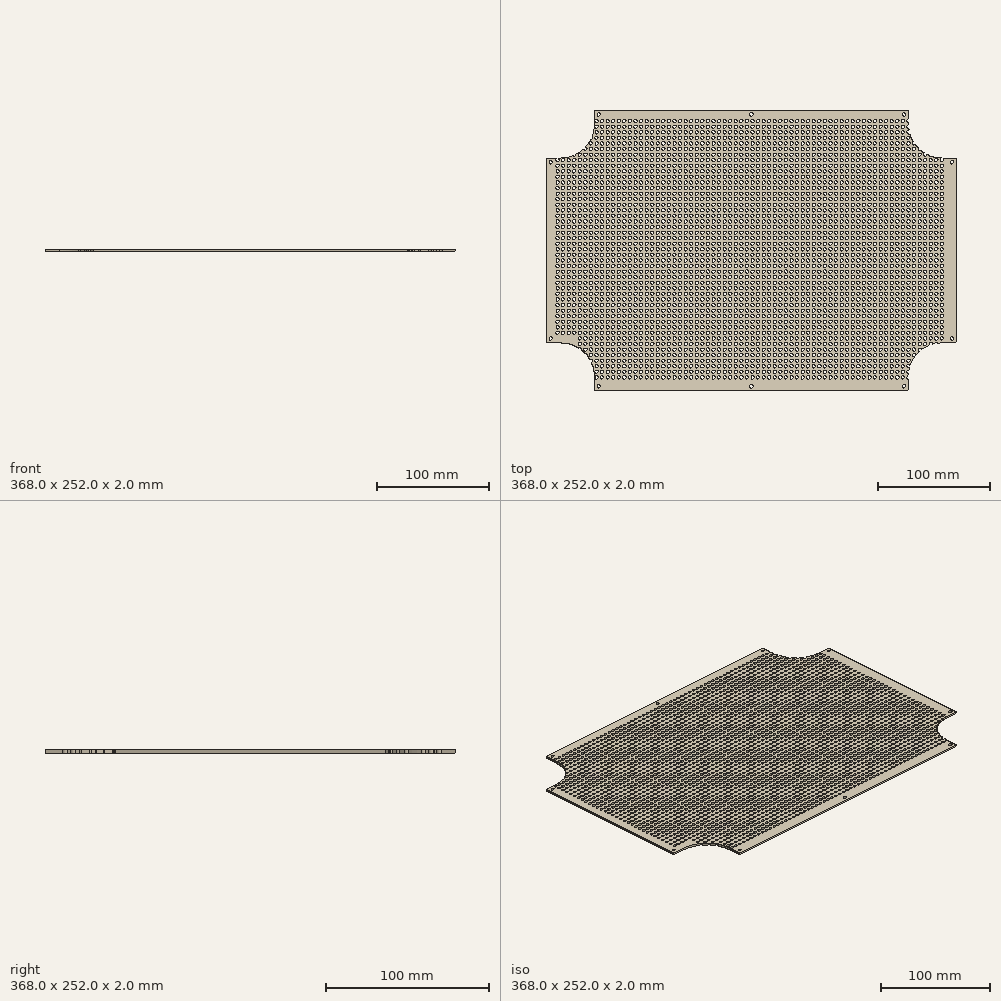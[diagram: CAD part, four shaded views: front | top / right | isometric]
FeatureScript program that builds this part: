
annotation { "Feature Type Name" : "Feature", "Feature Type Description" : "" }
export const myFeature = defineFeature(function(context is Context, id is Id, definition is map)
    precondition{}
    {
        {
            var Q0;
            Q0=qCreatedBy(makeId("Top.planeOp"),FACE);
            var sketch = newSketch(context, id + "F0", { "sketchPlane" : qUnion([Q0])});
            skLineSegment(sketch, "E0", {"start": v(-141, 126) * mm, "end": v(141, 126) * mm});
            skLineSegment(sketch, "E1", {"start": v(141, 126) * mm, "end": v(141, 113) * mm});
            skLineSegment(sketch, "E2", {"start": v(171, 83) * mm, "end": v(184, 83) * mm});
            skLineSegment(sketch, "E3", {"start": v(184, 83) * mm, "end": v(184, -83) * mm});
            skLineSegment(sketch, "E4", {"start": v(184, -83) * mm, "end": v(171, -83) * mm});
            skLineSegment(sketch, "E5", {"start": v(141, -113) * mm, "end": v(141, -126) * mm});
            skLineSegment(sketch, "E6", {"start": v(141, -126) * mm, "end": v(-141, -126) * mm});
            skLineSegment(sketch, "E7", {"start": v(-141, -126) * mm, "end": v(-141, -113) * mm});
            skLineSegment(sketch, "E8", {"start": v(-171, -83) * mm, "end": v(-184, -83) * mm});
            skLineSegment(sketch, "E9", {"start": v(-184, -83) * mm, "end": v(-184, 83) * mm});
            skLineSegment(sketch, "E10", {"start": v(-184, 83) * mm, "end": v(-171, 83) * mm});
            skLineSegment(sketch, "E11", {"start": v(-141, 113) * mm, "end": v(-141, 126) * mm});
            skPoint(sketch, "E12.visualSharp", {"position": v(-141, 83) * mm});
            skArc(sketch, "E12.filletArc", {"start": v(-171, 83) * mm, "mid": v(-149.79, 91.79) * mm, "end": v(-141, 113) * mm});
            skPoint(sketch, "E13.visualSharp", {"position": v(141, 83) * mm});
            skArc(sketch, "E13.filletArc", {"start": v(141, 113) * mm, "mid": v(149.79, 91.79) * mm, "end": v(171, 83) * mm});
            skPoint(sketch, "E14.visualSharp", {"position": v(141, -83) * mm});
            skArc(sketch, "E14.filletArc", {"start": v(171, -83) * mm, "mid": v(149.79, -91.79) * mm, "end": v(141, -113) * mm});
            skPoint(sketch, "E15.visualSharp", {"position": v(-141, -83) * mm});
            skArc(sketch, "E15.filletArc", {"start": v(-141, -113) * mm, "mid": v(-149.79, -91.79) * mm, "end": v(-171, -83) * mm});
            skPoint(sketch, "E16", {"position": v(0, 126) * mm});
            skPoint(sketch, "E17", {"position": v(0, -126) * mm});
            skPoint(sketch, "E18", {"position": v(-184, 0) * mm});
            skPoint(sketch, "E19", {"position": v(184, 0) * mm});
            skLineSegment(sketch, "E20", {"start": v(-137, 139.15) * mm, "end": v(-137, -174.05) * mm, "construction": true});
            skLineSegment(sketch, "E21", {"start": v(-207.28, 122) * mm, "end": v(169.12, 122) * mm, "construction": true});
            skLineSegment(sketch, "E22", {"start": v(-202.37, 79) * mm, "end": v(209.85, 79) * mm, "construction": true});
            skLineSegment(sketch, "E23.MirrorCS", {"start": v(-202.37, -79) * mm, "end": v(209.85, -79) * mm, "construction": true});
            skLineSegment(sketch, "E24.MirrorCS", {"start": v(-207.28, -122) * mm, "end": v(169.12, -122) * mm, "construction": true});
            skLineSegment(sketch, "E25.MirrorCS", {"start": v(137, 139.15) * mm, "end": v(137, -174.05) * mm, "construction": true});
            skLineSegment(sketch, "E26", {"start": v(-180, 93.5) * mm, "end": v(-180, -106.64) * mm, "construction": true});
            skLineSegment(sketch, "E27.MirrorCS", {"start": v(180, 93.5) * mm, "end": v(180, -106.64) * mm, "construction": true});
            skLineSegment(sketch, "E28", {"start": v(0, 134.08) * mm, "end": v(0, -140) * mm, "construction": true});
            skCircle(sketch, "E29", {"center": v(0, 122) * mm, "radius": 1.6 * mm});
            skCircle(sketch, "E30", {"center": v(-137, 122) * mm, "radius": 1.6 * mm});
            skCircle(sketch, "E31", {"center": v(137, 122) * mm, "radius": 1.6 * mm});
            skCircle(sketch, "E32", {"center": v(-180, 79) * mm, "radius": 1.6 * mm});
            skCircle(sketch, "E33", {"center": v(-180, -79) * mm, "radius": 1.6 * mm});
            skCircle(sketch, "E34", {"center": v(-137, -122) * mm, "radius": 1.6 * mm});
            skCircle(sketch, "E35", {"center": v(0, -122) * mm, "radius": 1.6 * mm});
            skCircle(sketch, "E36", {"center": v(137, -122) * mm, "radius": 1.6 * mm});
            skCircle(sketch, "E37", {"center": v(180, -79) * mm, "radius": 1.6 * mm});
            skCircle(sketch, "E38", {"center": v(180, 79) * mm, "radius": 1.6 * mm});
            skLineSegment(sketch, "E39", {"start": v(-174, 129.65) * mm, "end": v(-174, 62.5) * mm, "construction": true});
            skLineSegment(sketch, "E40", {"start": v(-188.78, 116) * mm, "end": v(-116.91, 116) * mm, "construction": true});
            skCircle(sketch, "E41", {"center": v(-174, 116) * mm, "radius": 1.5 * mm});
            skCircle(sketch, "E42.1.0.0", {"center": v(-169, 116) * mm, "radius": 1.5 * mm});
            skCircle(sketch, "E42.2.0.0", {"center": v(-164, 116) * mm, "radius": 1.5 * mm});
            skCircle(sketch, "E42.3.0.0", {"center": v(-159, 116) * mm, "radius": 1.5 * mm});
            skCircle(sketch, "E42.4.0.0", {"center": v(-154, 116) * mm, "radius": 1.5 * mm});
            skCircle(sketch, "E42.5.0.0", {"center": v(-149, 116) * mm, "radius": 1.5 * mm});
            skCircle(sketch, "E42.6.0.0", {"center": v(-144, 116) * mm, "radius": 1.5 * mm});
            skCircle(sketch, "E42.7.0.0", {"center": v(-139, 116) * mm, "radius": 1.5 * mm});
            skCircle(sketch, "E42.8.0.0", {"center": v(-134, 116) * mm, "radius": 1.5 * mm});
            skCircle(sketch, "E42.9.0.0", {"center": v(-129, 116) * mm, "radius": 1.5 * mm});
            skCircle(sketch, "E42.10.0.0", {"center": v(-124, 116) * mm, "radius": 1.5 * mm});
            skCircle(sketch, "E42.11.0.0", {"center": v(-119, 116) * mm, "radius": 1.5 * mm});
            skCircle(sketch, "E42.12.0.0", {"center": v(-114, 116) * mm, "radius": 1.5 * mm});
            skCircle(sketch, "E42.13.0.0", {"center": v(-109, 116) * mm, "radius": 1.5 * mm});
            skCircle(sketch, "E42.14.0.0", {"center": v(-104, 116) * mm, "radius": 1.5 * mm});
            skCircle(sketch, "E42.15.0.0", {"center": v(-99, 116) * mm, "radius": 1.5 * mm});
            skCircle(sketch, "E42.16.0.0", {"center": v(-94, 116) * mm, "radius": 1.5 * mm});
            skCircle(sketch, "E42.17.0.0", {"center": v(-89, 116) * mm, "radius": 1.5 * mm});
            skCircle(sketch, "E42.18.0.0", {"center": v(-84, 116) * mm, "radius": 1.5 * mm});
            skCircle(sketch, "E42.19.0.0", {"center": v(-79, 116) * mm, "radius": 1.5 * mm});
            skCircle(sketch, "E42.20.0.0", {"center": v(-74, 116) * mm, "radius": 1.5 * mm});
            skCircle(sketch, "E42.21.0.0", {"center": v(-69, 116) * mm, "radius": 1.5 * mm});
            skCircle(sketch, "E42.22.0.0", {"center": v(-64, 116) * mm, "radius": 1.5 * mm});
            skCircle(sketch, "E42.23.0.0", {"center": v(-59, 116) * mm, "radius": 1.5 * mm});
            skCircle(sketch, "E42.24.0.0", {"center": v(-54, 116) * mm, "radius": 1.5 * mm});
            skCircle(sketch, "E42.25.0.0", {"center": v(-49, 116) * mm, "radius": 1.5 * mm});
            skCircle(sketch, "E42.26.0.0", {"center": v(-44, 116) * mm, "radius": 1.5 * mm});
            skCircle(sketch, "E42.27.0.0", {"center": v(-39, 116) * mm, "radius": 1.5 * mm});
            skCircle(sketch, "E42.28.0.0", {"center": v(-34, 116) * mm, "radius": 1.5 * mm});
            skCircle(sketch, "E42.29.0.0", {"center": v(-29, 116) * mm, "radius": 1.5 * mm});
            skLineSegment(sketch, "E42.direction1", {"start": v(-174, 116) * mm, "end": v(-169, 116) * mm, "construction": true});
            skCircle(sketch, "E43.0.30.0", {"center": v(-24, 116) * mm, "radius": 1.5 * mm});
            skCircle(sketch, "E43.0.31.0", {"center": v(-19, 116) * mm, "radius": 1.5 * mm});
            skCircle(sketch, "E43.0.32.0", {"center": v(-14, 116) * mm, "radius": 1.5 * mm});
            skCircle(sketch, "E43.0.33.0", {"center": v(-9, 116) * mm, "radius": 1.5 * mm});
            skCircle(sketch, "E43.0.34.0", {"center": v(-4, 116) * mm, "radius": 1.5 * mm});
            skCircle(sketch, "E43.0.35.0", {"center": v(1, 116) * mm, "radius": 1.5 * mm});
            skCircle(sketch, "E43.0.36.0", {"center": v(6, 116) * mm, "radius": 1.5 * mm});
            skCircle(sketch, "E43.0.37.0", {"center": v(11, 116) * mm, "radius": 1.5 * mm});
            skCircle(sketch, "E43.0.38.0", {"center": v(16, 116) * mm, "radius": 1.5 * mm});
            skCircle(sketch, "E43.0.39.0", {"center": v(21, 116) * mm, "radius": 1.5 * mm});
            skCircle(sketch, "E43.0.40.0", {"center": v(26, 116) * mm, "radius": 1.5 * mm});
            skCircle(sketch, "E43.0.41.0", {"center": v(31, 116) * mm, "radius": 1.5 * mm});
            skCircle(sketch, "E43.0.42.0", {"center": v(36, 116) * mm, "radius": 1.5 * mm});
            skCircle(sketch, "E43.0.43.0", {"center": v(41, 116) * mm, "radius": 1.5 * mm});
            skCircle(sketch, "E43.0.44.0", {"center": v(46, 116) * mm, "radius": 1.5 * mm});
            skCircle(sketch, "E43.0.45.0", {"center": v(51, 116) * mm, "radius": 1.5 * mm});
            skCircle(sketch, "E43.0.46.0", {"center": v(56, 116) * mm, "radius": 1.5 * mm});
            skCircle(sketch, "E43.0.47.0", {"center": v(61, 116) * mm, "radius": 1.5 * mm});
            skCircle(sketch, "E43.0.48.0", {"center": v(66, 116) * mm, "radius": 1.5 * mm});
            skCircle(sketch, "E43.0.49.0", {"center": v(71, 116) * mm, "radius": 1.5 * mm});
            skCircle(sketch, "E43.0.50.0", {"center": v(76, 116) * mm, "radius": 1.5 * mm});
            skCircle(sketch, "E43.0.51.0", {"center": v(81, 116) * mm, "radius": 1.5 * mm});
            skCircle(sketch, "E43.0.52.0", {"center": v(86, 116) * mm, "radius": 1.5 * mm});
            skCircle(sketch, "E43.0.53.0", {"center": v(91, 116) * mm, "radius": 1.5 * mm});
            skCircle(sketch, "E43.0.54.0", {"center": v(96, 116) * mm, "radius": 1.5 * mm});
            skCircle(sketch, "E43.0.55.0", {"center": v(101, 116) * mm, "radius": 1.5 * mm});
            skCircle(sketch, "E43.0.56.0", {"center": v(106, 116) * mm, "radius": 1.5 * mm});
            skCircle(sketch, "E43.0.57.0", {"center": v(111, 116) * mm, "radius": 1.5 * mm});
            skCircle(sketch, "E43.0.58.0", {"center": v(116, 116) * mm, "radius": 1.5 * mm});
            skCircle(sketch, "E43.0.59.0", {"center": v(121, 116) * mm, "radius": 1.5 * mm});
            skCircle(sketch, "E43.0.60.0", {"center": v(126, 116) * mm, "radius": 1.5 * mm});
            skCircle(sketch, "E43.0.61.0", {"center": v(131, 116) * mm, "radius": 1.5 * mm});
            skCircle(sketch, "E43.0.62.0", {"center": v(136, 116) * mm, "radius": 1.5 * mm});
            skCircle(sketch, "E43.0.63.0", {"center": v(141, 116) * mm, "radius": 1.5 * mm});
            skCircle(sketch, "E43.0.64.0", {"center": v(146, 116) * mm, "radius": 1.5 * mm});
            skCircle(sketch, "E43.0.65.0", {"center": v(151, 116) * mm, "radius": 1.5 * mm});
            skCircle(sketch, "E43.0.66.0", {"center": v(156, 116) * mm, "radius": 1.5 * mm});
            skCircle(sketch, "E43.0.67.0", {"center": v(161, 116) * mm, "radius": 1.5 * mm});
            skCircle(sketch, "E43.0.68.0", {"center": v(166, 116) * mm, "radius": 1.5 * mm});
            skCircle(sketch, "E43.0.69.0", {"center": v(171, 116) * mm, "radius": 1.5 * mm});
            skCircle(sketch, "E44.1.0.0", {"center": v(166, 111) * mm, "radius": 1.5 * mm});
            skCircle(sketch, "E44.1.0.1", {"center": v(21, 111) * mm, "radius": 1.5 * mm});
            skCircle(sketch, "E44.1.0.2", {"center": v(-99, 111) * mm, "radius": 1.5 * mm});
            skCircle(sketch, "E44.1.0.3", {"center": v(6, 111) * mm, "radius": 1.5 * mm});
            skCircle(sketch, "E44.1.0.4", {"center": v(-54, 111) * mm, "radius": 1.5 * mm});
            skCircle(sketch, "E44.1.0.5", {"center": v(171, 111) * mm, "radius": 1.5 * mm});
            skCircle(sketch, "E44.1.0.6", {"center": v(-104, 111) * mm, "radius": 1.5 * mm});
            skCircle(sketch, "E44.1.0.7", {"center": v(11, 111) * mm, "radius": 1.5 * mm});
            skCircle(sketch, "E44.1.0.8", {"center": v(56, 111) * mm, "radius": 1.5 * mm});
            skCircle(sketch, "E44.1.0.9", {"center": v(-134, 111) * mm, "radius": 1.5 * mm});
            skCircle(sketch, "E44.1.0.10", {"center": v(51, 111) * mm, "radius": 1.5 * mm});
            skCircle(sketch, "E44.1.0.11", {"center": v(131, 111) * mm, "radius": 1.5 * mm});
            skCircle(sketch, "E44.1.0.12", {"center": v(151, 111) * mm, "radius": 1.5 * mm});
            skCircle(sketch, "E44.1.0.13", {"center": v(-24, 111) * mm, "radius": 1.5 * mm});
            skCircle(sketch, "E44.1.0.14", {"center": v(-64, 111) * mm, "radius": 1.5 * mm});
            skCircle(sketch, "E44.1.0.15", {"center": v(-9, 111) * mm, "radius": 1.5 * mm});
            skCircle(sketch, "E44.1.0.16", {"center": v(136, 111) * mm, "radius": 1.5 * mm});
            skCircle(sketch, "E44.1.0.17", {"center": v(91, 111) * mm, "radius": 1.5 * mm});
            skCircle(sketch, "E44.1.0.18", {"center": v(101, 111) * mm, "radius": 1.5 * mm});
            skCircle(sketch, "E44.1.0.19", {"center": v(-144, 111) * mm, "radius": 1.5 * mm});
            skCircle(sketch, "E44.1.0.20", {"center": v(71, 111) * mm, "radius": 1.5 * mm});
            skCircle(sketch, "E44.1.0.21", {"center": v(-69, 111) * mm, "radius": 1.5 * mm});
            skCircle(sketch, "E44.1.0.22", {"center": v(-84, 111) * mm, "radius": 1.5 * mm});
            skCircle(sketch, "E44.1.0.23", {"center": v(116, 111) * mm, "radius": 1.5 * mm});
            skCircle(sketch, "E44.1.0.24", {"center": v(-164, 111) * mm, "radius": 1.5 * mm});
            skCircle(sketch, "E44.1.0.25", {"center": v(86, 111) * mm, "radius": 1.5 * mm});
            skCircle(sketch, "E44.1.0.26", {"center": v(-149, 111) * mm, "radius": 1.5 * mm});
            skCircle(sketch, "E44.1.0.27", {"center": v(106, 111) * mm, "radius": 1.5 * mm});
            skCircle(sketch, "E44.1.0.28", {"center": v(-94, 111) * mm, "radius": 1.5 * mm});
            skCircle(sketch, "E44.1.0.29", {"center": v(-129, 111) * mm, "radius": 1.5 * mm});
            skCircle(sketch, "E44.1.0.30", {"center": v(-19, 111) * mm, "radius": 1.5 * mm});
            skCircle(sketch, "E44.1.0.31", {"center": v(-49, 111) * mm, "radius": 1.5 * mm});
            skCircle(sketch, "E44.1.0.32", {"center": v(26, 111) * mm, "radius": 1.5 * mm});
            skCircle(sketch, "E44.1.0.33", {"center": v(61, 111) * mm, "radius": 1.5 * mm});
            skCircle(sketch, "E44.1.0.34", {"center": v(16, 111) * mm, "radius": 1.5 * mm});
            skCircle(sketch, "E44.1.0.35", {"center": v(96, 111) * mm, "radius": 1.5 * mm});
            skCircle(sketch, "E44.1.0.36", {"center": v(-139, 111) * mm, "radius": 1.5 * mm});
            skCircle(sketch, "E44.1.0.37", {"center": v(-59, 111) * mm, "radius": 1.5 * mm});
            skCircle(sketch, "E44.1.0.38", {"center": v(111, 111) * mm, "radius": 1.5 * mm});
            skCircle(sketch, "E44.1.0.39", {"center": v(146, 111) * mm, "radius": 1.5 * mm});
            skCircle(sketch, "E44.1.0.40", {"center": v(-89, 111) * mm, "radius": 1.5 * mm});
            skCircle(sketch, "E44.1.0.41", {"center": v(-44, 111) * mm, "radius": 1.5 * mm});
            skCircle(sketch, "E44.1.0.42", {"center": v(-124, 111) * mm, "radius": 1.5 * mm});
            skCircle(sketch, "E44.1.0.43", {"center": v(-14, 111) * mm, "radius": 1.5 * mm});
            skCircle(sketch, "E44.1.0.44", {"center": v(31, 111) * mm, "radius": 1.5 * mm});
            skCircle(sketch, "E44.1.0.45", {"center": v(66, 111) * mm, "radius": 1.5 * mm});
            skCircle(sketch, "E44.1.0.46", {"center": v(141, 111) * mm, "radius": 1.5 * mm});
            skCircle(sketch, "E44.1.0.47", {"center": v(36, 111) * mm, "radius": 1.5 * mm});
            skCircle(sketch, "E44.1.0.48", {"center": v(-39, 111) * mm, "radius": 1.5 * mm});
            skCircle(sketch, "E44.1.0.49", {"center": v(-119, 111) * mm, "radius": 1.5 * mm});
            skCircle(sketch, "E44.1.0.50", {"center": v(-79, 111) * mm, "radius": 1.5 * mm});
            skCircle(sketch, "E44.1.0.51", {"center": v(-159, 111) * mm, "radius": 1.5 * mm});
            skCircle(sketch, "E44.1.0.52", {"center": v(156, 111) * mm, "radius": 1.5 * mm});
            skCircle(sketch, "E44.1.0.53", {"center": v(76, 111) * mm, "radius": 1.5 * mm});
            skCircle(sketch, "E44.1.0.54", {"center": v(-4, 111) * mm, "radius": 1.5 * mm});
            skCircle(sketch, "E44.1.0.55", {"center": v(41, 111) * mm, "radius": 1.5 * mm});
            skCircle(sketch, "E44.1.0.56", {"center": v(-34, 111) * mm, "radius": 1.5 * mm});
            skCircle(sketch, "E44.1.0.57", {"center": v(-114, 111) * mm, "radius": 1.5 * mm});
            skCircle(sketch, "E44.1.0.58", {"center": v(121, 111) * mm, "radius": 1.5 * mm});
            skCircle(sketch, "E44.1.0.59", {"center": v(-74, 111) * mm, "radius": 1.5 * mm});
            skCircle(sketch, "E44.1.0.60", {"center": v(-154, 111) * mm, "radius": 1.5 * mm});
            skCircle(sketch, "E44.1.0.61", {"center": v(161, 111) * mm, "radius": 1.5 * mm});
            skCircle(sketch, "E44.1.0.62", {"center": v(81, 111) * mm, "radius": 1.5 * mm});
            skCircle(sketch, "E44.1.0.63", {"center": v(1, 111) * mm, "radius": 1.5 * mm});
            skCircle(sketch, "E44.1.0.64", {"center": v(46, 111) * mm, "radius": 1.5 * mm});
            skCircle(sketch, "E44.1.0.65", {"center": v(-29, 111) * mm, "radius": 1.5 * mm});
            skCircle(sketch, "E44.1.0.66", {"center": v(-109, 111) * mm, "radius": 1.5 * mm});
            skCircle(sketch, "E44.1.0.67", {"center": v(126, 111) * mm, "radius": 1.5 * mm});
            skLineSegment(sketch, "E44.1.0.68", {"start": v(-174, 111) * mm, "end": v(-169, 111) * mm, "construction": true});
            skCircle(sketch, "E44.1.0.69", {"center": v(-174, 111) * mm, "radius": 1.5 * mm});
            skCircle(sketch, "E44.1.0.70", {"center": v(-169, 111) * mm, "radius": 1.5 * mm});
            skCircle(sketch, "E44.2.0.0", {"center": v(166, 106) * mm, "radius": 1.5 * mm});
            skCircle(sketch, "E44.2.0.1", {"center": v(21, 106) * mm, "radius": 1.5 * mm});
            skCircle(sketch, "E44.2.0.2", {"center": v(-99, 106) * mm, "radius": 1.5 * mm});
            skCircle(sketch, "E44.2.0.3", {"center": v(6, 106) * mm, "radius": 1.5 * mm});
            skCircle(sketch, "E44.2.0.4", {"center": v(-54, 106) * mm, "radius": 1.5 * mm});
            skCircle(sketch, "E44.2.0.5", {"center": v(171, 106) * mm, "radius": 1.5 * mm});
            skCircle(sketch, "E44.2.0.6", {"center": v(-104, 106) * mm, "radius": 1.5 * mm});
            skCircle(sketch, "E44.2.0.7", {"center": v(11, 106) * mm, "radius": 1.5 * mm});
            skCircle(sketch, "E44.2.0.8", {"center": v(56, 106) * mm, "radius": 1.5 * mm});
            skCircle(sketch, "E44.2.0.9", {"center": v(-134, 106) * mm, "radius": 1.5 * mm});
            skCircle(sketch, "E44.2.0.10", {"center": v(51, 106) * mm, "radius": 1.5 * mm});
            skCircle(sketch, "E44.2.0.11", {"center": v(131, 106) * mm, "radius": 1.5 * mm});
            skCircle(sketch, "E44.2.0.12", {"center": v(151, 106) * mm, "radius": 1.5 * mm});
            skCircle(sketch, "E44.2.0.13", {"center": v(-24, 106) * mm, "radius": 1.5 * mm});
            skCircle(sketch, "E44.2.0.14", {"center": v(-64, 106) * mm, "radius": 1.5 * mm});
            skCircle(sketch, "E44.2.0.15", {"center": v(-9, 106) * mm, "radius": 1.5 * mm});
            skCircle(sketch, "E44.2.0.16", {"center": v(136, 106) * mm, "radius": 1.5 * mm});
            skCircle(sketch, "E44.2.0.17", {"center": v(91, 106) * mm, "radius": 1.5 * mm});
            skCircle(sketch, "E44.2.0.18", {"center": v(101, 106) * mm, "radius": 1.5 * mm});
            skCircle(sketch, "E44.2.0.19", {"center": v(-144, 106) * mm, "radius": 1.5 * mm});
            skCircle(sketch, "E44.2.0.20", {"center": v(71, 106) * mm, "radius": 1.5 * mm});
            skCircle(sketch, "E44.2.0.21", {"center": v(-69, 106) * mm, "radius": 1.5 * mm});
            skCircle(sketch, "E44.2.0.22", {"center": v(-84, 106) * mm, "radius": 1.5 * mm});
            skCircle(sketch, "E44.2.0.23", {"center": v(116, 106) * mm, "radius": 1.5 * mm});
            skCircle(sketch, "E44.2.0.24", {"center": v(-164, 106) * mm, "radius": 1.5 * mm});
            skCircle(sketch, "E44.2.0.25", {"center": v(86, 106) * mm, "radius": 1.5 * mm});
            skCircle(sketch, "E44.2.0.26", {"center": v(-149, 106) * mm, "radius": 1.5 * mm});
            skCircle(sketch, "E44.2.0.27", {"center": v(106, 106) * mm, "radius": 1.5 * mm});
            skCircle(sketch, "E44.2.0.28", {"center": v(-94, 106) * mm, "radius": 1.5 * mm});
            skCircle(sketch, "E44.2.0.29", {"center": v(-129, 106) * mm, "radius": 1.5 * mm});
            skCircle(sketch, "E44.2.0.30", {"center": v(-19, 106) * mm, "radius": 1.5 * mm});
            skCircle(sketch, "E44.2.0.31", {"center": v(-49, 106) * mm, "radius": 1.5 * mm});
            skCircle(sketch, "E44.2.0.32", {"center": v(26, 106) * mm, "radius": 1.5 * mm});
            skCircle(sketch, "E44.2.0.33", {"center": v(61, 106) * mm, "radius": 1.5 * mm});
            skCircle(sketch, "E44.2.0.34", {"center": v(16, 106) * mm, "radius": 1.5 * mm});
            skCircle(sketch, "E44.2.0.35", {"center": v(96, 106) * mm, "radius": 1.5 * mm});
            skCircle(sketch, "E44.2.0.36", {"center": v(-139, 106) * mm, "radius": 1.5 * mm});
            skCircle(sketch, "E44.2.0.37", {"center": v(-59, 106) * mm, "radius": 1.5 * mm});
            skCircle(sketch, "E44.2.0.38", {"center": v(111, 106) * mm, "radius": 1.5 * mm});
            skCircle(sketch, "E44.2.0.39", {"center": v(146, 106) * mm, "radius": 1.5 * mm});
            skCircle(sketch, "E44.2.0.40", {"center": v(-89, 106) * mm, "radius": 1.5 * mm});
            skCircle(sketch, "E44.2.0.41", {"center": v(-44, 106) * mm, "radius": 1.5 * mm});
            skCircle(sketch, "E44.2.0.42", {"center": v(-124, 106) * mm, "radius": 1.5 * mm});
            skCircle(sketch, "E44.2.0.43", {"center": v(-14, 106) * mm, "radius": 1.5 * mm});
            skCircle(sketch, "E44.2.0.44", {"center": v(31, 106) * mm, "radius": 1.5 * mm});
            skCircle(sketch, "E44.2.0.45", {"center": v(66, 106) * mm, "radius": 1.5 * mm});
            skCircle(sketch, "E44.2.0.46", {"center": v(141, 106) * mm, "radius": 1.5 * mm});
            skCircle(sketch, "E44.2.0.47", {"center": v(36, 106) * mm, "radius": 1.5 * mm});
            skCircle(sketch, "E44.2.0.48", {"center": v(-39, 106) * mm, "radius": 1.5 * mm});
            skCircle(sketch, "E44.2.0.49", {"center": v(-119, 106) * mm, "radius": 1.5 * mm});
            skCircle(sketch, "E44.2.0.50", {"center": v(-79, 106) * mm, "radius": 1.5 * mm});
            skCircle(sketch, "E44.2.0.51", {"center": v(-159, 106) * mm, "radius": 1.5 * mm});
            skCircle(sketch, "E44.2.0.52", {"center": v(156, 106) * mm, "radius": 1.5 * mm});
            skCircle(sketch, "E44.2.0.53", {"center": v(76, 106) * mm, "radius": 1.5 * mm});
            skCircle(sketch, "E44.2.0.54", {"center": v(-4, 106) * mm, "radius": 1.5 * mm});
            skCircle(sketch, "E44.2.0.55", {"center": v(41, 106) * mm, "radius": 1.5 * mm});
            skCircle(sketch, "E44.2.0.56", {"center": v(-34, 106) * mm, "radius": 1.5 * mm});
            skCircle(sketch, "E44.2.0.57", {"center": v(-114, 106) * mm, "radius": 1.5 * mm});
            skCircle(sketch, "E44.2.0.58", {"center": v(121, 106) * mm, "radius": 1.5 * mm});
            skCircle(sketch, "E44.2.0.59", {"center": v(-74, 106) * mm, "radius": 1.5 * mm});
            skCircle(sketch, "E44.2.0.60", {"center": v(-154, 106) * mm, "radius": 1.5 * mm});
            skCircle(sketch, "E44.2.0.61", {"center": v(161, 106) * mm, "radius": 1.5 * mm});
            skCircle(sketch, "E44.2.0.62", {"center": v(81, 106) * mm, "radius": 1.5 * mm});
            skCircle(sketch, "E44.2.0.63", {"center": v(1, 106) * mm, "radius": 1.5 * mm});
            skCircle(sketch, "E44.2.0.64", {"center": v(46, 106) * mm, "radius": 1.5 * mm});
            skCircle(sketch, "E44.2.0.65", {"center": v(-29, 106) * mm, "radius": 1.5 * mm});
            skCircle(sketch, "E44.2.0.66", {"center": v(-109, 106) * mm, "radius": 1.5 * mm});
            skCircle(sketch, "E44.2.0.67", {"center": v(126, 106) * mm, "radius": 1.5 * mm});
            skLineSegment(sketch, "E44.2.0.68", {"start": v(-174, 106) * mm, "end": v(-169, 106) * mm, "construction": true});
            skCircle(sketch, "E44.2.0.69", {"center": v(-174, 106) * mm, "radius": 1.5 * mm});
            skCircle(sketch, "E44.2.0.70", {"center": v(-169, 106) * mm, "radius": 1.5 * mm});
            skCircle(sketch, "E44.3.0.0", {"center": v(166, 101) * mm, "radius": 1.5 * mm});
            skCircle(sketch, "E44.3.0.1", {"center": v(21, 101) * mm, "radius": 1.5 * mm});
            skCircle(sketch, "E44.3.0.2", {"center": v(-99, 101) * mm, "radius": 1.5 * mm});
            skCircle(sketch, "E44.3.0.3", {"center": v(6, 101) * mm, "radius": 1.5 * mm});
            skCircle(sketch, "E44.3.0.4", {"center": v(-54, 101) * mm, "radius": 1.5 * mm});
            skCircle(sketch, "E44.3.0.5", {"center": v(171, 101) * mm, "radius": 1.5 * mm});
            skCircle(sketch, "E44.3.0.6", {"center": v(-104, 101) * mm, "radius": 1.5 * mm});
            skCircle(sketch, "E44.3.0.7", {"center": v(11, 101) * mm, "radius": 1.5 * mm});
            skCircle(sketch, "E44.3.0.8", {"center": v(56, 101) * mm, "radius": 1.5 * mm});
            skCircle(sketch, "E44.3.0.9", {"center": v(-134, 101) * mm, "radius": 1.5 * mm});
            skCircle(sketch, "E44.3.0.10", {"center": v(51, 101) * mm, "radius": 1.5 * mm});
            skCircle(sketch, "E44.3.0.11", {"center": v(131, 101) * mm, "radius": 1.5 * mm});
            skCircle(sketch, "E44.3.0.12", {"center": v(151, 101) * mm, "radius": 1.5 * mm});
            skCircle(sketch, "E44.3.0.13", {"center": v(-24, 101) * mm, "radius": 1.5 * mm});
            skCircle(sketch, "E44.3.0.14", {"center": v(-64, 101) * mm, "radius": 1.5 * mm});
            skCircle(sketch, "E44.3.0.15", {"center": v(-9, 101) * mm, "radius": 1.5 * mm});
            skCircle(sketch, "E44.3.0.16", {"center": v(136, 101) * mm, "radius": 1.5 * mm});
            skCircle(sketch, "E44.3.0.17", {"center": v(91, 101) * mm, "radius": 1.5 * mm});
            skCircle(sketch, "E44.3.0.18", {"center": v(101, 101) * mm, "radius": 1.5 * mm});
            skCircle(sketch, "E44.3.0.19", {"center": v(-144, 101) * mm, "radius": 1.5 * mm});
            skCircle(sketch, "E44.3.0.20", {"center": v(71, 101) * mm, "radius": 1.5 * mm});
            skCircle(sketch, "E44.3.0.21", {"center": v(-69, 101) * mm, "radius": 1.5 * mm});
            skCircle(sketch, "E44.3.0.22", {"center": v(-84, 101) * mm, "radius": 1.5 * mm});
            skCircle(sketch, "E44.3.0.23", {"center": v(116, 101) * mm, "radius": 1.5 * mm});
            skCircle(sketch, "E44.3.0.24", {"center": v(-164, 101) * mm, "radius": 1.5 * mm});
            skCircle(sketch, "E44.3.0.25", {"center": v(86, 101) * mm, "radius": 1.5 * mm});
            skCircle(sketch, "E44.3.0.26", {"center": v(-149, 101) * mm, "radius": 1.5 * mm});
            skCircle(sketch, "E44.3.0.27", {"center": v(106, 101) * mm, "radius": 1.5 * mm});
            skCircle(sketch, "E44.3.0.28", {"center": v(-94, 101) * mm, "radius": 1.5 * mm});
            skCircle(sketch, "E44.3.0.29", {"center": v(-129, 101) * mm, "radius": 1.5 * mm});
            skCircle(sketch, "E44.3.0.30", {"center": v(-19, 101) * mm, "radius": 1.5 * mm});
            skCircle(sketch, "E44.3.0.31", {"center": v(-49, 101) * mm, "radius": 1.5 * mm});
            skCircle(sketch, "E44.3.0.32", {"center": v(26, 101) * mm, "radius": 1.5 * mm});
            skCircle(sketch, "E44.3.0.33", {"center": v(61, 101) * mm, "radius": 1.5 * mm});
            skCircle(sketch, "E44.3.0.34", {"center": v(16, 101) * mm, "radius": 1.5 * mm});
            skCircle(sketch, "E44.3.0.35", {"center": v(96, 101) * mm, "radius": 1.5 * mm});
            skCircle(sketch, "E44.3.0.36", {"center": v(-139, 101) * mm, "radius": 1.5 * mm});
            skCircle(sketch, "E44.3.0.37", {"center": v(-59, 101) * mm, "radius": 1.5 * mm});
            skCircle(sketch, "E44.3.0.38", {"center": v(111, 101) * mm, "radius": 1.5 * mm});
            skCircle(sketch, "E44.3.0.39", {"center": v(146, 101) * mm, "radius": 1.5 * mm});
            skCircle(sketch, "E44.3.0.40", {"center": v(-89, 101) * mm, "radius": 1.5 * mm});
            skCircle(sketch, "E44.3.0.41", {"center": v(-44, 101) * mm, "radius": 1.5 * mm});
            skCircle(sketch, "E44.3.0.42", {"center": v(-124, 101) * mm, "radius": 1.5 * mm});
            skCircle(sketch, "E44.3.0.43", {"center": v(-14, 101) * mm, "radius": 1.5 * mm});
            skCircle(sketch, "E44.3.0.44", {"center": v(31, 101) * mm, "radius": 1.5 * mm});
            skCircle(sketch, "E44.3.0.45", {"center": v(66, 101) * mm, "radius": 1.5 * mm});
            skCircle(sketch, "E44.3.0.46", {"center": v(141, 101) * mm, "radius": 1.5 * mm});
            skCircle(sketch, "E44.3.0.47", {"center": v(36, 101) * mm, "radius": 1.5 * mm});
            skCircle(sketch, "E44.3.0.48", {"center": v(-39, 101) * mm, "radius": 1.5 * mm});
            skCircle(sketch, "E44.3.0.49", {"center": v(-119, 101) * mm, "radius": 1.5 * mm});
            skCircle(sketch, "E44.3.0.50", {"center": v(-79, 101) * mm, "radius": 1.5 * mm});
            skCircle(sketch, "E44.3.0.51", {"center": v(-159, 101) * mm, "radius": 1.5 * mm});
            skCircle(sketch, "E44.3.0.52", {"center": v(156, 101) * mm, "radius": 1.5 * mm});
            skCircle(sketch, "E44.3.0.53", {"center": v(76, 101) * mm, "radius": 1.5 * mm});
            skCircle(sketch, "E44.3.0.54", {"center": v(-4, 101) * mm, "radius": 1.5 * mm});
            skCircle(sketch, "E44.3.0.55", {"center": v(41, 101) * mm, "radius": 1.5 * mm});
            skCircle(sketch, "E44.3.0.56", {"center": v(-34, 101) * mm, "radius": 1.5 * mm});
            skCircle(sketch, "E44.3.0.57", {"center": v(-114, 101) * mm, "radius": 1.5 * mm});
            skCircle(sketch, "E44.3.0.58", {"center": v(121, 101) * mm, "radius": 1.5 * mm});
            skCircle(sketch, "E44.3.0.59", {"center": v(-74, 101) * mm, "radius": 1.5 * mm});
            skCircle(sketch, "E44.3.0.60", {"center": v(-154, 101) * mm, "radius": 1.5 * mm});
            skCircle(sketch, "E44.3.0.61", {"center": v(161, 101) * mm, "radius": 1.5 * mm});
            skCircle(sketch, "E44.3.0.62", {"center": v(81, 101) * mm, "radius": 1.5 * mm});
            skCircle(sketch, "E44.3.0.63", {"center": v(1, 101) * mm, "radius": 1.5 * mm});
            skCircle(sketch, "E44.3.0.64", {"center": v(46, 101) * mm, "radius": 1.5 * mm});
            skCircle(sketch, "E44.3.0.65", {"center": v(-29, 101) * mm, "radius": 1.5 * mm});
            skCircle(sketch, "E44.3.0.66", {"center": v(-109, 101) * mm, "radius": 1.5 * mm});
            skCircle(sketch, "E44.3.0.67", {"center": v(126, 101) * mm, "radius": 1.5 * mm});
            skLineSegment(sketch, "E44.3.0.68", {"start": v(-174, 101) * mm, "end": v(-169, 101) * mm, "construction": true});
            skCircle(sketch, "E44.3.0.69", {"center": v(-174, 101) * mm, "radius": 1.5 * mm});
            skCircle(sketch, "E44.3.0.70", {"center": v(-169, 101) * mm, "radius": 1.5 * mm});
            skCircle(sketch, "E44.4.0.0", {"center": v(166, 96) * mm, "radius": 1.5 * mm});
            skCircle(sketch, "E44.4.0.1", {"center": v(21, 96) * mm, "radius": 1.5 * mm});
            skCircle(sketch, "E44.4.0.2", {"center": v(-99, 96) * mm, "radius": 1.5 * mm});
            skCircle(sketch, "E44.4.0.3", {"center": v(6, 96) * mm, "radius": 1.5 * mm});
            skCircle(sketch, "E44.4.0.4", {"center": v(-54, 96) * mm, "radius": 1.5 * mm});
            skCircle(sketch, "E44.4.0.5", {"center": v(171, 96) * mm, "radius": 1.5 * mm});
            skCircle(sketch, "E44.4.0.6", {"center": v(-104, 96) * mm, "radius": 1.5 * mm});
            skCircle(sketch, "E44.4.0.7", {"center": v(11, 96) * mm, "radius": 1.5 * mm});
            skCircle(sketch, "E44.4.0.8", {"center": v(56, 96) * mm, "radius": 1.5 * mm});
            skCircle(sketch, "E44.4.0.9", {"center": v(-134, 96) * mm, "radius": 1.5 * mm});
            skCircle(sketch, "E44.4.0.10", {"center": v(51, 96) * mm, "radius": 1.5 * mm});
            skCircle(sketch, "E44.4.0.11", {"center": v(131, 96) * mm, "radius": 1.5 * mm});
            skCircle(sketch, "E44.4.0.12", {"center": v(151, 96) * mm, "radius": 1.5 * mm});
            skCircle(sketch, "E44.4.0.13", {"center": v(-24, 96) * mm, "radius": 1.5 * mm});
            skCircle(sketch, "E44.4.0.14", {"center": v(-64, 96) * mm, "radius": 1.5 * mm});
            skCircle(sketch, "E44.4.0.15", {"center": v(-9, 96) * mm, "radius": 1.5 * mm});
            skCircle(sketch, "E44.4.0.16", {"center": v(136, 96) * mm, "radius": 1.5 * mm});
            skCircle(sketch, "E44.4.0.17", {"center": v(91, 96) * mm, "radius": 1.5 * mm});
            skCircle(sketch, "E44.4.0.18", {"center": v(101, 96) * mm, "radius": 1.5 * mm});
            skCircle(sketch, "E44.4.0.19", {"center": v(-144, 96) * mm, "radius": 1.5 * mm});
            skCircle(sketch, "E44.4.0.20", {"center": v(71, 96) * mm, "radius": 1.5 * mm});
            skCircle(sketch, "E44.4.0.21", {"center": v(-69, 96) * mm, "radius": 1.5 * mm});
            skCircle(sketch, "E44.4.0.22", {"center": v(-84, 96) * mm, "radius": 1.5 * mm});
            skCircle(sketch, "E44.4.0.23", {"center": v(116, 96) * mm, "radius": 1.5 * mm});
            skCircle(sketch, "E44.4.0.24", {"center": v(-164, 96) * mm, "radius": 1.5 * mm});
            skCircle(sketch, "E44.4.0.25", {"center": v(86, 96) * mm, "radius": 1.5 * mm});
            skCircle(sketch, "E44.4.0.26", {"center": v(-149, 96) * mm, "radius": 1.5 * mm});
            skCircle(sketch, "E44.4.0.27", {"center": v(106, 96) * mm, "radius": 1.5 * mm});
            skCircle(sketch, "E44.4.0.28", {"center": v(-94, 96) * mm, "radius": 1.5 * mm});
            skCircle(sketch, "E44.4.0.29", {"center": v(-129, 96) * mm, "radius": 1.5 * mm});
            skCircle(sketch, "E44.4.0.30", {"center": v(-19, 96) * mm, "radius": 1.5 * mm});
            skCircle(sketch, "E44.4.0.31", {"center": v(-49, 96) * mm, "radius": 1.5 * mm});
            skCircle(sketch, "E44.4.0.32", {"center": v(26, 96) * mm, "radius": 1.5 * mm});
            skCircle(sketch, "E44.4.0.33", {"center": v(61, 96) * mm, "radius": 1.5 * mm});
            skCircle(sketch, "E44.4.0.34", {"center": v(16, 96) * mm, "radius": 1.5 * mm});
            skCircle(sketch, "E44.4.0.35", {"center": v(96, 96) * mm, "radius": 1.5 * mm});
            skCircle(sketch, "E44.4.0.36", {"center": v(-139, 96) * mm, "radius": 1.5 * mm});
            skCircle(sketch, "E44.4.0.37", {"center": v(-59, 96) * mm, "radius": 1.5 * mm});
            skCircle(sketch, "E44.4.0.38", {"center": v(111, 96) * mm, "radius": 1.5 * mm});
            skCircle(sketch, "E44.4.0.39", {"center": v(146, 96) * mm, "radius": 1.5 * mm});
            skCircle(sketch, "E44.4.0.40", {"center": v(-89, 96) * mm, "radius": 1.5 * mm});
            skCircle(sketch, "E44.4.0.41", {"center": v(-44, 96) * mm, "radius": 1.5 * mm});
            skCircle(sketch, "E44.4.0.42", {"center": v(-124, 96) * mm, "radius": 1.5 * mm});
            skCircle(sketch, "E44.4.0.43", {"center": v(-14, 96) * mm, "radius": 1.5 * mm});
            skCircle(sketch, "E44.4.0.44", {"center": v(31, 96) * mm, "radius": 1.5 * mm});
            skCircle(sketch, "E44.4.0.45", {"center": v(66, 96) * mm, "radius": 1.5 * mm});
            skCircle(sketch, "E44.4.0.46", {"center": v(141, 96) * mm, "radius": 1.5 * mm});
            skCircle(sketch, "E44.4.0.47", {"center": v(36, 96) * mm, "radius": 1.5 * mm});
            skCircle(sketch, "E44.4.0.48", {"center": v(-39, 96) * mm, "radius": 1.5 * mm});
            skCircle(sketch, "E44.4.0.49", {"center": v(-119, 96) * mm, "radius": 1.5 * mm});
            skCircle(sketch, "E44.4.0.50", {"center": v(-79, 96) * mm, "radius": 1.5 * mm});
            skCircle(sketch, "E44.4.0.51", {"center": v(-159, 96) * mm, "radius": 1.5 * mm});
            skCircle(sketch, "E44.4.0.52", {"center": v(156, 96) * mm, "radius": 1.5 * mm});
            skCircle(sketch, "E44.4.0.53", {"center": v(76, 96) * mm, "radius": 1.5 * mm});
            skCircle(sketch, "E44.4.0.54", {"center": v(-4, 96) * mm, "radius": 1.5 * mm});
            skCircle(sketch, "E44.4.0.55", {"center": v(41, 96) * mm, "radius": 1.5 * mm});
            skCircle(sketch, "E44.4.0.56", {"center": v(-34, 96) * mm, "radius": 1.5 * mm});
            skCircle(sketch, "E44.4.0.57", {"center": v(-114, 96) * mm, "radius": 1.5 * mm});
            skCircle(sketch, "E44.4.0.58", {"center": v(121, 96) * mm, "radius": 1.5 * mm});
            skCircle(sketch, "E44.4.0.59", {"center": v(-74, 96) * mm, "radius": 1.5 * mm});
            skCircle(sketch, "E44.4.0.60", {"center": v(-154, 96) * mm, "radius": 1.5 * mm});
            skCircle(sketch, "E44.4.0.61", {"center": v(161, 96) * mm, "radius": 1.5 * mm});
            skCircle(sketch, "E44.4.0.62", {"center": v(81, 96) * mm, "radius": 1.5 * mm});
            skCircle(sketch, "E44.4.0.63", {"center": v(1, 96) * mm, "radius": 1.5 * mm});
            skCircle(sketch, "E44.4.0.64", {"center": v(46, 96) * mm, "radius": 1.5 * mm});
            skCircle(sketch, "E44.4.0.65", {"center": v(-29, 96) * mm, "radius": 1.5 * mm});
            skCircle(sketch, "E44.4.0.66", {"center": v(-109, 96) * mm, "radius": 1.5 * mm});
            skCircle(sketch, "E44.4.0.67", {"center": v(126, 96) * mm, "radius": 1.5 * mm});
            skLineSegment(sketch, "E44.4.0.68", {"start": v(-174, 96) * mm, "end": v(-169, 96) * mm, "construction": true});
            skCircle(sketch, "E44.4.0.69", {"center": v(-174, 96) * mm, "radius": 1.5 * mm});
            skCircle(sketch, "E44.4.0.70", {"center": v(-169, 96) * mm, "radius": 1.5 * mm});
            skCircle(sketch, "E44.5.0.0", {"center": v(166, 91) * mm, "radius": 1.5 * mm});
            skCircle(sketch, "E44.5.0.1", {"center": v(21, 91) * mm, "radius": 1.5 * mm});
            skCircle(sketch, "E44.5.0.2", {"center": v(-99, 91) * mm, "radius": 1.5 * mm});
            skCircle(sketch, "E44.5.0.3", {"center": v(6, 91) * mm, "radius": 1.5 * mm});
            skCircle(sketch, "E44.5.0.4", {"center": v(-54, 91) * mm, "radius": 1.5 * mm});
            skCircle(sketch, "E44.5.0.5", {"center": v(171, 91) * mm, "radius": 1.5 * mm});
            skCircle(sketch, "E44.5.0.6", {"center": v(-104, 91) * mm, "radius": 1.5 * mm});
            skCircle(sketch, "E44.5.0.7", {"center": v(11, 91) * mm, "radius": 1.5 * mm});
            skCircle(sketch, "E44.5.0.8", {"center": v(56, 91) * mm, "radius": 1.5 * mm});
            skCircle(sketch, "E44.5.0.9", {"center": v(-134, 91) * mm, "radius": 1.5 * mm});
            skCircle(sketch, "E44.5.0.10", {"center": v(51, 91) * mm, "radius": 1.5 * mm});
            skCircle(sketch, "E44.5.0.11", {"center": v(131, 91) * mm, "radius": 1.5 * mm});
            skCircle(sketch, "E44.5.0.12", {"center": v(151, 91) * mm, "radius": 1.5 * mm});
            skCircle(sketch, "E44.5.0.13", {"center": v(-24, 91) * mm, "radius": 1.5 * mm});
            skCircle(sketch, "E44.5.0.14", {"center": v(-64, 91) * mm, "radius": 1.5 * mm});
            skCircle(sketch, "E44.5.0.15", {"center": v(-9, 91) * mm, "radius": 1.5 * mm});
            skCircle(sketch, "E44.5.0.16", {"center": v(136, 91) * mm, "radius": 1.5 * mm});
            skCircle(sketch, "E44.5.0.17", {"center": v(91, 91) * mm, "radius": 1.5 * mm});
            skCircle(sketch, "E44.5.0.18", {"center": v(101, 91) * mm, "radius": 1.5 * mm});
            skCircle(sketch, "E44.5.0.19", {"center": v(-144, 91) * mm, "radius": 1.5 * mm});
            skCircle(sketch, "E44.5.0.20", {"center": v(71, 91) * mm, "radius": 1.5 * mm});
            skCircle(sketch, "E44.5.0.21", {"center": v(-69, 91) * mm, "radius": 1.5 * mm});
            skCircle(sketch, "E44.5.0.22", {"center": v(-84, 91) * mm, "radius": 1.5 * mm});
            skCircle(sketch, "E44.5.0.23", {"center": v(116, 91) * mm, "radius": 1.5 * mm});
            skCircle(sketch, "E44.5.0.24", {"center": v(-164, 91) * mm, "radius": 1.5 * mm});
            skCircle(sketch, "E44.5.0.25", {"center": v(86, 91) * mm, "radius": 1.5 * mm});
            skCircle(sketch, "E44.5.0.26", {"center": v(-149, 91) * mm, "radius": 1.5 * mm});
            skCircle(sketch, "E44.5.0.27", {"center": v(106, 91) * mm, "radius": 1.5 * mm});
            skCircle(sketch, "E44.5.0.28", {"center": v(-94, 91) * mm, "radius": 1.5 * mm});
            skCircle(sketch, "E44.5.0.29", {"center": v(-129, 91) * mm, "radius": 1.5 * mm});
            skCircle(sketch, "E44.5.0.30", {"center": v(-19, 91) * mm, "radius": 1.5 * mm});
            skCircle(sketch, "E44.5.0.31", {"center": v(-49, 91) * mm, "radius": 1.5 * mm});
            skCircle(sketch, "E44.5.0.32", {"center": v(26, 91) * mm, "radius": 1.5 * mm});
            skCircle(sketch, "E44.5.0.33", {"center": v(61, 91) * mm, "radius": 1.5 * mm});
            skCircle(sketch, "E44.5.0.34", {"center": v(16, 91) * mm, "radius": 1.5 * mm});
            skCircle(sketch, "E44.5.0.35", {"center": v(96, 91) * mm, "radius": 1.5 * mm});
            skCircle(sketch, "E44.5.0.36", {"center": v(-139, 91) * mm, "radius": 1.5 * mm});
            skCircle(sketch, "E44.5.0.37", {"center": v(-59, 91) * mm, "radius": 1.5 * mm});
            skCircle(sketch, "E44.5.0.38", {"center": v(111, 91) * mm, "radius": 1.5 * mm});
            skCircle(sketch, "E44.5.0.39", {"center": v(146, 91) * mm, "radius": 1.5 * mm});
            skCircle(sketch, "E44.5.0.40", {"center": v(-89, 91) * mm, "radius": 1.5 * mm});
            skCircle(sketch, "E44.5.0.41", {"center": v(-44, 91) * mm, "radius": 1.5 * mm});
            skCircle(sketch, "E44.5.0.42", {"center": v(-124, 91) * mm, "radius": 1.5 * mm});
            skCircle(sketch, "E44.5.0.43", {"center": v(-14, 91) * mm, "radius": 1.5 * mm});
            skCircle(sketch, "E44.5.0.44", {"center": v(31, 91) * mm, "radius": 1.5 * mm});
            skCircle(sketch, "E44.5.0.45", {"center": v(66, 91) * mm, "radius": 1.5 * mm});
            skCircle(sketch, "E44.5.0.46", {"center": v(141, 91) * mm, "radius": 1.5 * mm});
            skCircle(sketch, "E44.5.0.47", {"center": v(36, 91) * mm, "radius": 1.5 * mm});
            skCircle(sketch, "E44.5.0.48", {"center": v(-39, 91) * mm, "radius": 1.5 * mm});
            skCircle(sketch, "E44.5.0.49", {"center": v(-119, 91) * mm, "radius": 1.5 * mm});
            skCircle(sketch, "E44.5.0.50", {"center": v(-79, 91) * mm, "radius": 1.5 * mm});
            skCircle(sketch, "E44.5.0.51", {"center": v(-159, 91) * mm, "radius": 1.5 * mm});
            skCircle(sketch, "E44.5.0.52", {"center": v(156, 91) * mm, "radius": 1.5 * mm});
            skCircle(sketch, "E44.5.0.53", {"center": v(76, 91) * mm, "radius": 1.5 * mm});
            skCircle(sketch, "E44.5.0.54", {"center": v(-4, 91) * mm, "radius": 1.5 * mm});
            skCircle(sketch, "E44.5.0.55", {"center": v(41, 91) * mm, "radius": 1.5 * mm});
            skCircle(sketch, "E44.5.0.56", {"center": v(-34, 91) * mm, "radius": 1.5 * mm});
            skCircle(sketch, "E44.5.0.57", {"center": v(-114, 91) * mm, "radius": 1.5 * mm});
            skCircle(sketch, "E44.5.0.58", {"center": v(121, 91) * mm, "radius": 1.5 * mm});
            skCircle(sketch, "E44.5.0.59", {"center": v(-74, 91) * mm, "radius": 1.5 * mm});
            skCircle(sketch, "E44.5.0.60", {"center": v(-154, 91) * mm, "radius": 1.5 * mm});
            skCircle(sketch, "E44.5.0.61", {"center": v(161, 91) * mm, "radius": 1.5 * mm});
            skCircle(sketch, "E44.5.0.62", {"center": v(81, 91) * mm, "radius": 1.5 * mm});
            skCircle(sketch, "E44.5.0.63", {"center": v(1, 91) * mm, "radius": 1.5 * mm});
            skCircle(sketch, "E44.5.0.64", {"center": v(46, 91) * mm, "radius": 1.5 * mm});
            skCircle(sketch, "E44.5.0.65", {"center": v(-29, 91) * mm, "radius": 1.5 * mm});
            skCircle(sketch, "E44.5.0.66", {"center": v(-109, 91) * mm, "radius": 1.5 * mm});
            skCircle(sketch, "E44.5.0.67", {"center": v(126, 91) * mm, "radius": 1.5 * mm});
            skLineSegment(sketch, "E44.5.0.68", {"start": v(-174, 91) * mm, "end": v(-169, 91) * mm, "construction": true});
            skCircle(sketch, "E44.5.0.69", {"center": v(-174, 91) * mm, "radius": 1.5 * mm});
            skCircle(sketch, "E44.5.0.70", {"center": v(-169, 91) * mm, "radius": 1.5 * mm});
            skCircle(sketch, "E44.6.0.0", {"center": v(166, 86) * mm, "radius": 1.5 * mm});
            skCircle(sketch, "E44.6.0.1", {"center": v(21, 86) * mm, "radius": 1.5 * mm});
            skCircle(sketch, "E44.6.0.2", {"center": v(-99, 86) * mm, "radius": 1.5 * mm});
            skCircle(sketch, "E44.6.0.3", {"center": v(6, 86) * mm, "radius": 1.5 * mm});
            skCircle(sketch, "E44.6.0.4", {"center": v(-54, 86) * mm, "radius": 1.5 * mm});
            skCircle(sketch, "E44.6.0.5", {"center": v(171, 86) * mm, "radius": 1.5 * mm});
            skCircle(sketch, "E44.6.0.6", {"center": v(-104, 86) * mm, "radius": 1.5 * mm});
            skCircle(sketch, "E44.6.0.7", {"center": v(11, 86) * mm, "radius": 1.5 * mm});
            skCircle(sketch, "E44.6.0.8", {"center": v(56, 86) * mm, "radius": 1.5 * mm});
            skCircle(sketch, "E44.6.0.9", {"center": v(-134, 86) * mm, "radius": 1.5 * mm});
            skCircle(sketch, "E44.6.0.10", {"center": v(51, 86) * mm, "radius": 1.5 * mm});
            skCircle(sketch, "E44.6.0.11", {"center": v(131, 86) * mm, "radius": 1.5 * mm});
            skCircle(sketch, "E44.6.0.12", {"center": v(151, 86) * mm, "radius": 1.5 * mm});
            skCircle(sketch, "E44.6.0.13", {"center": v(-24, 86) * mm, "radius": 1.5 * mm});
            skCircle(sketch, "E44.6.0.14", {"center": v(-64, 86) * mm, "radius": 1.5 * mm});
            skCircle(sketch, "E44.6.0.15", {"center": v(-9, 86) * mm, "radius": 1.5 * mm});
            skCircle(sketch, "E44.6.0.16", {"center": v(136, 86) * mm, "radius": 1.5 * mm});
            skCircle(sketch, "E44.6.0.17", {"center": v(91, 86) * mm, "radius": 1.5 * mm});
            skCircle(sketch, "E44.6.0.18", {"center": v(101, 86) * mm, "radius": 1.5 * mm});
            skCircle(sketch, "E44.6.0.19", {"center": v(-144, 86) * mm, "radius": 1.5 * mm});
            skCircle(sketch, "E44.6.0.20", {"center": v(71, 86) * mm, "radius": 1.5 * mm});
            skCircle(sketch, "E44.6.0.21", {"center": v(-69, 86) * mm, "radius": 1.5 * mm});
            skCircle(sketch, "E44.6.0.22", {"center": v(-84, 86) * mm, "radius": 1.5 * mm});
            skCircle(sketch, "E44.6.0.23", {"center": v(116, 86) * mm, "radius": 1.5 * mm});
            skCircle(sketch, "E44.6.0.24", {"center": v(-164, 86) * mm, "radius": 1.5 * mm});
            skCircle(sketch, "E44.6.0.25", {"center": v(86, 86) * mm, "radius": 1.5 * mm});
            skCircle(sketch, "E44.6.0.26", {"center": v(-149, 86) * mm, "radius": 1.5 * mm});
            skCircle(sketch, "E44.6.0.27", {"center": v(106, 86) * mm, "radius": 1.5 * mm});
            skCircle(sketch, "E44.6.0.28", {"center": v(-94, 86) * mm, "radius": 1.5 * mm});
            skCircle(sketch, "E44.6.0.29", {"center": v(-129, 86) * mm, "radius": 1.5 * mm});
            skCircle(sketch, "E44.6.0.30", {"center": v(-19, 86) * mm, "radius": 1.5 * mm});
            skCircle(sketch, "E44.6.0.31", {"center": v(-49, 86) * mm, "radius": 1.5 * mm});
            skCircle(sketch, "E44.6.0.32", {"center": v(26, 86) * mm, "radius": 1.5 * mm});
            skCircle(sketch, "E44.6.0.33", {"center": v(61, 86) * mm, "radius": 1.5 * mm});
            skCircle(sketch, "E44.6.0.34", {"center": v(16, 86) * mm, "radius": 1.5 * mm});
            skCircle(sketch, "E44.6.0.35", {"center": v(96, 86) * mm, "radius": 1.5 * mm});
            skCircle(sketch, "E44.6.0.36", {"center": v(-139, 86) * mm, "radius": 1.5 * mm});
            skCircle(sketch, "E44.6.0.37", {"center": v(-59, 86) * mm, "radius": 1.5 * mm});
            skCircle(sketch, "E44.6.0.38", {"center": v(111, 86) * mm, "radius": 1.5 * mm});
            skCircle(sketch, "E44.6.0.39", {"center": v(146, 86) * mm, "radius": 1.5 * mm});
            skCircle(sketch, "E44.6.0.40", {"center": v(-89, 86) * mm, "radius": 1.5 * mm});
            skCircle(sketch, "E44.6.0.41", {"center": v(-44, 86) * mm, "radius": 1.5 * mm});
            skCircle(sketch, "E44.6.0.42", {"center": v(-124, 86) * mm, "radius": 1.5 * mm});
            skCircle(sketch, "E44.6.0.43", {"center": v(-14, 86) * mm, "radius": 1.5 * mm});
            skCircle(sketch, "E44.6.0.44", {"center": v(31, 86) * mm, "radius": 1.5 * mm});
            skCircle(sketch, "E44.6.0.45", {"center": v(66, 86) * mm, "radius": 1.5 * mm});
            skCircle(sketch, "E44.6.0.46", {"center": v(141, 86) * mm, "radius": 1.5 * mm});
            skCircle(sketch, "E44.6.0.47", {"center": v(36, 86) * mm, "radius": 1.5 * mm});
            skCircle(sketch, "E44.6.0.48", {"center": v(-39, 86) * mm, "radius": 1.5 * mm});
            skCircle(sketch, "E44.6.0.49", {"center": v(-119, 86) * mm, "radius": 1.5 * mm});
            skCircle(sketch, "E44.6.0.50", {"center": v(-79, 86) * mm, "radius": 1.5 * mm});
            skCircle(sketch, "E44.6.0.51", {"center": v(-159, 86) * mm, "radius": 1.5 * mm});
            skCircle(sketch, "E44.6.0.52", {"center": v(156, 86) * mm, "radius": 1.5 * mm});
            skCircle(sketch, "E44.6.0.53", {"center": v(76, 86) * mm, "radius": 1.5 * mm});
            skCircle(sketch, "E44.6.0.54", {"center": v(-4, 86) * mm, "radius": 1.5 * mm});
            skCircle(sketch, "E44.6.0.55", {"center": v(41, 86) * mm, "radius": 1.5 * mm});
            skCircle(sketch, "E44.6.0.56", {"center": v(-34, 86) * mm, "radius": 1.5 * mm});
            skCircle(sketch, "E44.6.0.57", {"center": v(-114, 86) * mm, "radius": 1.5 * mm});
            skCircle(sketch, "E44.6.0.58", {"center": v(121, 86) * mm, "radius": 1.5 * mm});
            skCircle(sketch, "E44.6.0.59", {"center": v(-74, 86) * mm, "radius": 1.5 * mm});
            skCircle(sketch, "E44.6.0.60", {"center": v(-154, 86) * mm, "radius": 1.5 * mm});
            skCircle(sketch, "E44.6.0.61", {"center": v(161, 86) * mm, "radius": 1.5 * mm});
            skCircle(sketch, "E44.6.0.62", {"center": v(81, 86) * mm, "radius": 1.5 * mm});
            skCircle(sketch, "E44.6.0.63", {"center": v(1, 86) * mm, "radius": 1.5 * mm});
            skCircle(sketch, "E44.6.0.64", {"center": v(46, 86) * mm, "radius": 1.5 * mm});
            skCircle(sketch, "E44.6.0.65", {"center": v(-29, 86) * mm, "radius": 1.5 * mm});
            skCircle(sketch, "E44.6.0.66", {"center": v(-109, 86) * mm, "radius": 1.5 * mm});
            skCircle(sketch, "E44.6.0.67", {"center": v(126, 86) * mm, "radius": 1.5 * mm});
            skLineSegment(sketch, "E44.6.0.68", {"start": v(-174, 86) * mm, "end": v(-169, 86) * mm, "construction": true});
            skCircle(sketch, "E44.6.0.69", {"center": v(-174, 86) * mm, "radius": 1.5 * mm});
            skCircle(sketch, "E44.6.0.70", {"center": v(-169, 86) * mm, "radius": 1.5 * mm});
            skCircle(sketch, "E44.7.0.0", {"center": v(166, 81) * mm, "radius": 1.5 * mm});
            skCircle(sketch, "E44.7.0.1", {"center": v(21, 81) * mm, "radius": 1.5 * mm});
            skCircle(sketch, "E44.7.0.2", {"center": v(-99, 81) * mm, "radius": 1.5 * mm});
            skCircle(sketch, "E44.7.0.3", {"center": v(6, 81) * mm, "radius": 1.5 * mm});
            skCircle(sketch, "E44.7.0.4", {"center": v(-54, 81) * mm, "radius": 1.5 * mm});
            skCircle(sketch, "E44.7.0.5", {"center": v(171, 81) * mm, "radius": 1.5 * mm});
            skCircle(sketch, "E44.7.0.6", {"center": v(-104, 81) * mm, "radius": 1.5 * mm});
            skCircle(sketch, "E44.7.0.7", {"center": v(11, 81) * mm, "radius": 1.5 * mm});
            skCircle(sketch, "E44.7.0.8", {"center": v(56, 81) * mm, "radius": 1.5 * mm});
            skCircle(sketch, "E44.7.0.9", {"center": v(-134, 81) * mm, "radius": 1.5 * mm});
            skCircle(sketch, "E44.7.0.10", {"center": v(51, 81) * mm, "radius": 1.5 * mm});
            skCircle(sketch, "E44.7.0.11", {"center": v(131, 81) * mm, "radius": 1.5 * mm});
            skCircle(sketch, "E44.7.0.12", {"center": v(151, 81) * mm, "radius": 1.5 * mm});
            skCircle(sketch, "E44.7.0.13", {"center": v(-24, 81) * mm, "radius": 1.5 * mm});
            skCircle(sketch, "E44.7.0.14", {"center": v(-64, 81) * mm, "radius": 1.5 * mm});
            skCircle(sketch, "E44.7.0.15", {"center": v(-9, 81) * mm, "radius": 1.5 * mm});
            skCircle(sketch, "E44.7.0.16", {"center": v(136, 81) * mm, "radius": 1.5 * mm});
            skCircle(sketch, "E44.7.0.17", {"center": v(91, 81) * mm, "radius": 1.5 * mm});
            skCircle(sketch, "E44.7.0.18", {"center": v(101, 81) * mm, "radius": 1.5 * mm});
            skCircle(sketch, "E44.7.0.19", {"center": v(-144, 81) * mm, "radius": 1.5 * mm});
            skCircle(sketch, "E44.7.0.20", {"center": v(71, 81) * mm, "radius": 1.5 * mm});
            skCircle(sketch, "E44.7.0.21", {"center": v(-69, 81) * mm, "radius": 1.5 * mm});
            skCircle(sketch, "E44.7.0.22", {"center": v(-84, 81) * mm, "radius": 1.5 * mm});
            skCircle(sketch, "E44.7.0.23", {"center": v(116, 81) * mm, "radius": 1.5 * mm});
            skCircle(sketch, "E44.7.0.24", {"center": v(-164, 81) * mm, "radius": 1.5 * mm});
            skCircle(sketch, "E44.7.0.25", {"center": v(86, 81) * mm, "radius": 1.5 * mm});
            skCircle(sketch, "E44.7.0.26", {"center": v(-149, 81) * mm, "radius": 1.5 * mm});
            skCircle(sketch, "E44.7.0.27", {"center": v(106, 81) * mm, "radius": 1.5 * mm});
            skCircle(sketch, "E44.7.0.28", {"center": v(-94, 81) * mm, "radius": 1.5 * mm});
            skCircle(sketch, "E44.7.0.29", {"center": v(-129, 81) * mm, "radius": 1.5 * mm});
            skCircle(sketch, "E44.7.0.30", {"center": v(-19, 81) * mm, "radius": 1.5 * mm});
            skCircle(sketch, "E44.7.0.31", {"center": v(-49, 81) * mm, "radius": 1.5 * mm});
            skCircle(sketch, "E44.7.0.32", {"center": v(26, 81) * mm, "radius": 1.5 * mm});
            skCircle(sketch, "E44.7.0.33", {"center": v(61, 81) * mm, "radius": 1.5 * mm});
            skCircle(sketch, "E44.7.0.34", {"center": v(16, 81) * mm, "radius": 1.5 * mm});
            skCircle(sketch, "E44.7.0.35", {"center": v(96, 81) * mm, "radius": 1.5 * mm});
            skCircle(sketch, "E44.7.0.36", {"center": v(-139, 81) * mm, "radius": 1.5 * mm});
            skCircle(sketch, "E44.7.0.37", {"center": v(-59, 81) * mm, "radius": 1.5 * mm});
            skCircle(sketch, "E44.7.0.38", {"center": v(111, 81) * mm, "radius": 1.5 * mm});
            skCircle(sketch, "E44.7.0.39", {"center": v(146, 81) * mm, "radius": 1.5 * mm});
            skCircle(sketch, "E44.7.0.40", {"center": v(-89, 81) * mm, "radius": 1.5 * mm});
            skCircle(sketch, "E44.7.0.41", {"center": v(-44, 81) * mm, "radius": 1.5 * mm});
            skCircle(sketch, "E44.7.0.42", {"center": v(-124, 81) * mm, "radius": 1.5 * mm});
            skCircle(sketch, "E44.7.0.43", {"center": v(-14, 81) * mm, "radius": 1.5 * mm});
            skCircle(sketch, "E44.7.0.44", {"center": v(31, 81) * mm, "radius": 1.5 * mm});
            skCircle(sketch, "E44.7.0.45", {"center": v(66, 81) * mm, "radius": 1.5 * mm});
            skCircle(sketch, "E44.7.0.46", {"center": v(141, 81) * mm, "radius": 1.5 * mm});
            skCircle(sketch, "E44.7.0.47", {"center": v(36, 81) * mm, "radius": 1.5 * mm});
            skCircle(sketch, "E44.7.0.48", {"center": v(-39, 81) * mm, "radius": 1.5 * mm});
            skCircle(sketch, "E44.7.0.49", {"center": v(-119, 81) * mm, "radius": 1.5 * mm});
            skCircle(sketch, "E44.7.0.50", {"center": v(-79, 81) * mm, "radius": 1.5 * mm});
            skCircle(sketch, "E44.7.0.51", {"center": v(-159, 81) * mm, "radius": 1.5 * mm});
            skCircle(sketch, "E44.7.0.52", {"center": v(156, 81) * mm, "radius": 1.5 * mm});
            skCircle(sketch, "E44.7.0.53", {"center": v(76, 81) * mm, "radius": 1.5 * mm});
            skCircle(sketch, "E44.7.0.54", {"center": v(-4, 81) * mm, "radius": 1.5 * mm});
            skCircle(sketch, "E44.7.0.55", {"center": v(41, 81) * mm, "radius": 1.5 * mm});
            skCircle(sketch, "E44.7.0.56", {"center": v(-34, 81) * mm, "radius": 1.5 * mm});
            skCircle(sketch, "E44.7.0.57", {"center": v(-114, 81) * mm, "radius": 1.5 * mm});
            skCircle(sketch, "E44.7.0.58", {"center": v(121, 81) * mm, "radius": 1.5 * mm});
            skCircle(sketch, "E44.7.0.59", {"center": v(-74, 81) * mm, "radius": 1.5 * mm});
            skCircle(sketch, "E44.7.0.60", {"center": v(-154, 81) * mm, "radius": 1.5 * mm});
            skCircle(sketch, "E44.7.0.61", {"center": v(161, 81) * mm, "radius": 1.5 * mm});
            skCircle(sketch, "E44.7.0.62", {"center": v(81, 81) * mm, "radius": 1.5 * mm});
            skCircle(sketch, "E44.7.0.63", {"center": v(1, 81) * mm, "radius": 1.5 * mm});
            skCircle(sketch, "E44.7.0.64", {"center": v(46, 81) * mm, "radius": 1.5 * mm});
            skCircle(sketch, "E44.7.0.65", {"center": v(-29, 81) * mm, "radius": 1.5 * mm});
            skCircle(sketch, "E44.7.0.66", {"center": v(-109, 81) * mm, "radius": 1.5 * mm});
            skCircle(sketch, "E44.7.0.67", {"center": v(126, 81) * mm, "radius": 1.5 * mm});
            skLineSegment(sketch, "E44.7.0.68", {"start": v(-174, 81) * mm, "end": v(-169, 81) * mm, "construction": true});
            skCircle(sketch, "E44.7.0.69", {"center": v(-174, 81) * mm, "radius": 1.5 * mm});
            skCircle(sketch, "E44.7.0.70", {"center": v(-169, 81) * mm, "radius": 1.5 * mm});
            skCircle(sketch, "E44.8.0.0", {"center": v(166, 76) * mm, "radius": 1.5 * mm});
            skCircle(sketch, "E44.8.0.1", {"center": v(21, 76) * mm, "radius": 1.5 * mm});
            skCircle(sketch, "E44.8.0.2", {"center": v(-99, 76) * mm, "radius": 1.5 * mm});
            skCircle(sketch, "E44.8.0.3", {"center": v(6, 76) * mm, "radius": 1.5 * mm});
            skCircle(sketch, "E44.8.0.4", {"center": v(-54, 76) * mm, "radius": 1.5 * mm});
            skCircle(sketch, "E44.8.0.5", {"center": v(171, 76) * mm, "radius": 1.5 * mm});
            skCircle(sketch, "E44.8.0.6", {"center": v(-104, 76) * mm, "radius": 1.5 * mm});
            skCircle(sketch, "E44.8.0.7", {"center": v(11, 76) * mm, "radius": 1.5 * mm});
            skCircle(sketch, "E44.8.0.8", {"center": v(56, 76) * mm, "radius": 1.5 * mm});
            skCircle(sketch, "E44.8.0.9", {"center": v(-134, 76) * mm, "radius": 1.5 * mm});
            skCircle(sketch, "E44.8.0.10", {"center": v(51, 76) * mm, "radius": 1.5 * mm});
            skCircle(sketch, "E44.8.0.11", {"center": v(131, 76) * mm, "radius": 1.5 * mm});
            skCircle(sketch, "E44.8.0.12", {"center": v(151, 76) * mm, "radius": 1.5 * mm});
            skCircle(sketch, "E44.8.0.13", {"center": v(-24, 76) * mm, "radius": 1.5 * mm});
            skCircle(sketch, "E44.8.0.14", {"center": v(-64, 76) * mm, "radius": 1.5 * mm});
            skCircle(sketch, "E44.8.0.15", {"center": v(-9, 76) * mm, "radius": 1.5 * mm});
            skCircle(sketch, "E44.8.0.16", {"center": v(136, 76) * mm, "radius": 1.5 * mm});
            skCircle(sketch, "E44.8.0.17", {"center": v(91, 76) * mm, "radius": 1.5 * mm});
            skCircle(sketch, "E44.8.0.18", {"center": v(101, 76) * mm, "radius": 1.5 * mm});
            skCircle(sketch, "E44.8.0.19", {"center": v(-144, 76) * mm, "radius": 1.5 * mm});
            skCircle(sketch, "E44.8.0.20", {"center": v(71, 76) * mm, "radius": 1.5 * mm});
            skCircle(sketch, "E44.8.0.21", {"center": v(-69, 76) * mm, "radius": 1.5 * mm});
            skCircle(sketch, "E44.8.0.22", {"center": v(-84, 76) * mm, "radius": 1.5 * mm});
            skCircle(sketch, "E44.8.0.23", {"center": v(116, 76) * mm, "radius": 1.5 * mm});
            skCircle(sketch, "E44.8.0.24", {"center": v(-164, 76) * mm, "radius": 1.5 * mm});
            skCircle(sketch, "E44.8.0.25", {"center": v(86, 76) * mm, "radius": 1.5 * mm});
            skCircle(sketch, "E44.8.0.26", {"center": v(-149, 76) * mm, "radius": 1.5 * mm});
            skCircle(sketch, "E44.8.0.27", {"center": v(106, 76) * mm, "radius": 1.5 * mm});
            skCircle(sketch, "E44.8.0.28", {"center": v(-94, 76) * mm, "radius": 1.5 * mm});
            skCircle(sketch, "E44.8.0.29", {"center": v(-129, 76) * mm, "radius": 1.5 * mm});
            skCircle(sketch, "E44.8.0.30", {"center": v(-19, 76) * mm, "radius": 1.5 * mm});
            skCircle(sketch, "E44.8.0.31", {"center": v(-49, 76) * mm, "radius": 1.5 * mm});
            skCircle(sketch, "E44.8.0.32", {"center": v(26, 76) * mm, "radius": 1.5 * mm});
            skCircle(sketch, "E44.8.0.33", {"center": v(61, 76) * mm, "radius": 1.5 * mm});
            skCircle(sketch, "E44.8.0.34", {"center": v(16, 76) * mm, "radius": 1.5 * mm});
            skCircle(sketch, "E44.8.0.35", {"center": v(96, 76) * mm, "radius": 1.5 * mm});
            skCircle(sketch, "E44.8.0.36", {"center": v(-139, 76) * mm, "radius": 1.5 * mm});
            skCircle(sketch, "E44.8.0.37", {"center": v(-59, 76) * mm, "radius": 1.5 * mm});
            skCircle(sketch, "E44.8.0.38", {"center": v(111, 76) * mm, "radius": 1.5 * mm});
            skCircle(sketch, "E44.8.0.39", {"center": v(146, 76) * mm, "radius": 1.5 * mm});
            skCircle(sketch, "E44.8.0.40", {"center": v(-89, 76) * mm, "radius": 1.5 * mm});
            skCircle(sketch, "E44.8.0.41", {"center": v(-44, 76) * mm, "radius": 1.5 * mm});
            skCircle(sketch, "E44.8.0.42", {"center": v(-124, 76) * mm, "radius": 1.5 * mm});
            skCircle(sketch, "E44.8.0.43", {"center": v(-14, 76) * mm, "radius": 1.5 * mm});
            skCircle(sketch, "E44.8.0.44", {"center": v(31, 76) * mm, "radius": 1.5 * mm});
            skCircle(sketch, "E44.8.0.45", {"center": v(66, 76) * mm, "radius": 1.5 * mm});
            skCircle(sketch, "E44.8.0.46", {"center": v(141, 76) * mm, "radius": 1.5 * mm});
            skCircle(sketch, "E44.8.0.47", {"center": v(36, 76) * mm, "radius": 1.5 * mm});
            skCircle(sketch, "E44.8.0.48", {"center": v(-39, 76) * mm, "radius": 1.5 * mm});
            skCircle(sketch, "E44.8.0.49", {"center": v(-119, 76) * mm, "radius": 1.5 * mm});
            skCircle(sketch, "E44.8.0.50", {"center": v(-79, 76) * mm, "radius": 1.5 * mm});
            skCircle(sketch, "E44.8.0.51", {"center": v(-159, 76) * mm, "radius": 1.5 * mm});
            skCircle(sketch, "E44.8.0.52", {"center": v(156, 76) * mm, "radius": 1.5 * mm});
            skCircle(sketch, "E44.8.0.53", {"center": v(76, 76) * mm, "radius": 1.5 * mm});
            skCircle(sketch, "E44.8.0.54", {"center": v(-4, 76) * mm, "radius": 1.5 * mm});
            skCircle(sketch, "E44.8.0.55", {"center": v(41, 76) * mm, "radius": 1.5 * mm});
            skCircle(sketch, "E44.8.0.56", {"center": v(-34, 76) * mm, "radius": 1.5 * mm});
            skCircle(sketch, "E44.8.0.57", {"center": v(-114, 76) * mm, "radius": 1.5 * mm});
            skCircle(sketch, "E44.8.0.58", {"center": v(121, 76) * mm, "radius": 1.5 * mm});
            skCircle(sketch, "E44.8.0.59", {"center": v(-74, 76) * mm, "radius": 1.5 * mm});
            skCircle(sketch, "E44.8.0.60", {"center": v(-154, 76) * mm, "radius": 1.5 * mm});
            skCircle(sketch, "E44.8.0.61", {"center": v(161, 76) * mm, "radius": 1.5 * mm});
            skCircle(sketch, "E44.8.0.62", {"center": v(81, 76) * mm, "radius": 1.5 * mm});
            skCircle(sketch, "E44.8.0.63", {"center": v(1, 76) * mm, "radius": 1.5 * mm});
            skCircle(sketch, "E44.8.0.64", {"center": v(46, 76) * mm, "radius": 1.5 * mm});
            skCircle(sketch, "E44.8.0.65", {"center": v(-29, 76) * mm, "radius": 1.5 * mm});
            skCircle(sketch, "E44.8.0.66", {"center": v(-109, 76) * mm, "radius": 1.5 * mm});
            skCircle(sketch, "E44.8.0.67", {"center": v(126, 76) * mm, "radius": 1.5 * mm});
            skLineSegment(sketch, "E44.8.0.68", {"start": v(-174, 76) * mm, "end": v(-169, 76) * mm, "construction": true});
            skCircle(sketch, "E44.8.0.69", {"center": v(-174, 76) * mm, "radius": 1.5 * mm});
            skCircle(sketch, "E44.8.0.70", {"center": v(-169, 76) * mm, "radius": 1.5 * mm});
            skCircle(sketch, "E44.9.0.0", {"center": v(166, 71) * mm, "radius": 1.5 * mm});
            skCircle(sketch, "E44.9.0.1", {"center": v(21, 71) * mm, "radius": 1.5 * mm});
            skCircle(sketch, "E44.9.0.2", {"center": v(-99, 71) * mm, "radius": 1.5 * mm});
            skCircle(sketch, "E44.9.0.3", {"center": v(6, 71) * mm, "radius": 1.5 * mm});
            skCircle(sketch, "E44.9.0.4", {"center": v(-54, 71) * mm, "radius": 1.5 * mm});
            skCircle(sketch, "E44.9.0.5", {"center": v(171, 71) * mm, "radius": 1.5 * mm});
            skCircle(sketch, "E44.9.0.6", {"center": v(-104, 71) * mm, "radius": 1.5 * mm});
            skCircle(sketch, "E44.9.0.7", {"center": v(11, 71) * mm, "radius": 1.5 * mm});
            skCircle(sketch, "E44.9.0.8", {"center": v(56, 71) * mm, "radius": 1.5 * mm});
            skCircle(sketch, "E44.9.0.9", {"center": v(-134, 71) * mm, "radius": 1.5 * mm});
            skCircle(sketch, "E44.9.0.10", {"center": v(51, 71) * mm, "radius": 1.5 * mm});
            skCircle(sketch, "E44.9.0.11", {"center": v(131, 71) * mm, "radius": 1.5 * mm});
            skCircle(sketch, "E44.9.0.12", {"center": v(151, 71) * mm, "radius": 1.5 * mm});
            skCircle(sketch, "E44.9.0.13", {"center": v(-24, 71) * mm, "radius": 1.5 * mm});
            skCircle(sketch, "E44.9.0.14", {"center": v(-64, 71) * mm, "radius": 1.5 * mm});
            skCircle(sketch, "E44.9.0.15", {"center": v(-9, 71) * mm, "radius": 1.5 * mm});
            skCircle(sketch, "E44.9.0.16", {"center": v(136, 71) * mm, "radius": 1.5 * mm});
            skCircle(sketch, "E44.9.0.17", {"center": v(91, 71) * mm, "radius": 1.5 * mm});
            skCircle(sketch, "E44.9.0.18", {"center": v(101, 71) * mm, "radius": 1.5 * mm});
            skCircle(sketch, "E44.9.0.19", {"center": v(-144, 71) * mm, "radius": 1.5 * mm});
            skCircle(sketch, "E44.9.0.20", {"center": v(71, 71) * mm, "radius": 1.5 * mm});
            skCircle(sketch, "E44.9.0.21", {"center": v(-69, 71) * mm, "radius": 1.5 * mm});
            skCircle(sketch, "E44.9.0.22", {"center": v(-84, 71) * mm, "radius": 1.5 * mm});
            skCircle(sketch, "E44.9.0.23", {"center": v(116, 71) * mm, "radius": 1.5 * mm});
            skCircle(sketch, "E44.9.0.24", {"center": v(-164, 71) * mm, "radius": 1.5 * mm});
            skCircle(sketch, "E44.9.0.25", {"center": v(86, 71) * mm, "radius": 1.5 * mm});
            skCircle(sketch, "E44.9.0.26", {"center": v(-149, 71) * mm, "radius": 1.5 * mm});
            skCircle(sketch, "E44.9.0.27", {"center": v(106, 71) * mm, "radius": 1.5 * mm});
            skCircle(sketch, "E44.9.0.28", {"center": v(-94, 71) * mm, "radius": 1.5 * mm});
            skCircle(sketch, "E44.9.0.29", {"center": v(-129, 71) * mm, "radius": 1.5 * mm});
            skCircle(sketch, "E44.9.0.30", {"center": v(-19, 71) * mm, "radius": 1.5 * mm});
            skCircle(sketch, "E44.9.0.31", {"center": v(-49, 71) * mm, "radius": 1.5 * mm});
            skCircle(sketch, "E44.9.0.32", {"center": v(26, 71) * mm, "radius": 1.5 * mm});
            skCircle(sketch, "E44.9.0.33", {"center": v(61, 71) * mm, "radius": 1.5 * mm});
            skCircle(sketch, "E44.9.0.34", {"center": v(16, 71) * mm, "radius": 1.5 * mm});
            skCircle(sketch, "E44.9.0.35", {"center": v(96, 71) * mm, "radius": 1.5 * mm});
            skCircle(sketch, "E44.9.0.36", {"center": v(-139, 71) * mm, "radius": 1.5 * mm});
            skCircle(sketch, "E44.9.0.37", {"center": v(-59, 71) * mm, "radius": 1.5 * mm});
            skCircle(sketch, "E44.9.0.38", {"center": v(111, 71) * mm, "radius": 1.5 * mm});
            skCircle(sketch, "E44.9.0.39", {"center": v(146, 71) * mm, "radius": 1.5 * mm});
            skCircle(sketch, "E44.9.0.40", {"center": v(-89, 71) * mm, "radius": 1.5 * mm});
            skCircle(sketch, "E44.9.0.41", {"center": v(-44, 71) * mm, "radius": 1.5 * mm});
            skCircle(sketch, "E44.9.0.42", {"center": v(-124, 71) * mm, "radius": 1.5 * mm});
            skCircle(sketch, "E44.9.0.43", {"center": v(-14, 71) * mm, "radius": 1.5 * mm});
            skCircle(sketch, "E44.9.0.44", {"center": v(31, 71) * mm, "radius": 1.5 * mm});
            skCircle(sketch, "E44.9.0.45", {"center": v(66, 71) * mm, "radius": 1.5 * mm});
            skCircle(sketch, "E44.9.0.46", {"center": v(141, 71) * mm, "radius": 1.5 * mm});
            skCircle(sketch, "E44.9.0.47", {"center": v(36, 71) * mm, "radius": 1.5 * mm});
            skCircle(sketch, "E44.9.0.48", {"center": v(-39, 71) * mm, "radius": 1.5 * mm});
            skCircle(sketch, "E44.9.0.49", {"center": v(-119, 71) * mm, "radius": 1.5 * mm});
            skCircle(sketch, "E44.9.0.50", {"center": v(-79, 71) * mm, "radius": 1.5 * mm});
            skCircle(sketch, "E44.9.0.51", {"center": v(-159, 71) * mm, "radius": 1.5 * mm});
            skCircle(sketch, "E44.9.0.52", {"center": v(156, 71) * mm, "radius": 1.5 * mm});
            skCircle(sketch, "E44.9.0.53", {"center": v(76, 71) * mm, "radius": 1.5 * mm});
            skCircle(sketch, "E44.9.0.54", {"center": v(-4, 71) * mm, "radius": 1.5 * mm});
            skCircle(sketch, "E44.9.0.55", {"center": v(41, 71) * mm, "radius": 1.5 * mm});
            skCircle(sketch, "E44.9.0.56", {"center": v(-34, 71) * mm, "radius": 1.5 * mm});
            skCircle(sketch, "E44.9.0.57", {"center": v(-114, 71) * mm, "radius": 1.5 * mm});
            skCircle(sketch, "E44.9.0.58", {"center": v(121, 71) * mm, "radius": 1.5 * mm});
            skCircle(sketch, "E44.9.0.59", {"center": v(-74, 71) * mm, "radius": 1.5 * mm});
            skCircle(sketch, "E44.9.0.60", {"center": v(-154, 71) * mm, "radius": 1.5 * mm});
            skCircle(sketch, "E44.9.0.61", {"center": v(161, 71) * mm, "radius": 1.5 * mm});
            skCircle(sketch, "E44.9.0.62", {"center": v(81, 71) * mm, "radius": 1.5 * mm});
            skCircle(sketch, "E44.9.0.63", {"center": v(1, 71) * mm, "radius": 1.5 * mm});
            skCircle(sketch, "E44.9.0.64", {"center": v(46, 71) * mm, "radius": 1.5 * mm});
            skCircle(sketch, "E44.9.0.65", {"center": v(-29, 71) * mm, "radius": 1.5 * mm});
            skCircle(sketch, "E44.9.0.66", {"center": v(-109, 71) * mm, "radius": 1.5 * mm});
            skCircle(sketch, "E44.9.0.67", {"center": v(126, 71) * mm, "radius": 1.5 * mm});
            skLineSegment(sketch, "E44.9.0.68", {"start": v(-174, 71) * mm, "end": v(-169, 71) * mm, "construction": true});
            skCircle(sketch, "E44.9.0.69", {"center": v(-174, 71) * mm, "radius": 1.5 * mm});
            skCircle(sketch, "E44.9.0.70", {"center": v(-169, 71) * mm, "radius": 1.5 * mm});
            skCircle(sketch, "E44.10.0.0", {"center": v(166, 66) * mm, "radius": 1.5 * mm});
            skCircle(sketch, "E44.10.0.1", {"center": v(21, 66) * mm, "radius": 1.5 * mm});
            skCircle(sketch, "E44.10.0.2", {"center": v(-99, 66) * mm, "radius": 1.5 * mm});
            skCircle(sketch, "E44.10.0.3", {"center": v(6, 66) * mm, "radius": 1.5 * mm});
            skCircle(sketch, "E44.10.0.4", {"center": v(-54, 66) * mm, "radius": 1.5 * mm});
            skCircle(sketch, "E44.10.0.5", {"center": v(171, 66) * mm, "radius": 1.5 * mm});
            skCircle(sketch, "E44.10.0.6", {"center": v(-104, 66) * mm, "radius": 1.5 * mm});
            skCircle(sketch, "E44.10.0.7", {"center": v(11, 66) * mm, "radius": 1.5 * mm});
            skCircle(sketch, "E44.10.0.8", {"center": v(56, 66) * mm, "radius": 1.5 * mm});
            skCircle(sketch, "E44.10.0.9", {"center": v(-134, 66) * mm, "radius": 1.5 * mm});
            skCircle(sketch, "E44.10.0.10", {"center": v(51, 66) * mm, "radius": 1.5 * mm});
            skCircle(sketch, "E44.10.0.11", {"center": v(131, 66) * mm, "radius": 1.5 * mm});
            skCircle(sketch, "E44.10.0.12", {"center": v(151, 66) * mm, "radius": 1.5 * mm});
            skCircle(sketch, "E44.10.0.13", {"center": v(-24, 66) * mm, "radius": 1.5 * mm});
            skCircle(sketch, "E44.10.0.14", {"center": v(-64, 66) * mm, "radius": 1.5 * mm});
            skCircle(sketch, "E44.10.0.15", {"center": v(-9, 66) * mm, "radius": 1.5 * mm});
            skCircle(sketch, "E44.10.0.16", {"center": v(136, 66) * mm, "radius": 1.5 * mm});
            skCircle(sketch, "E44.10.0.17", {"center": v(91, 66) * mm, "radius": 1.5 * mm});
            skCircle(sketch, "E44.10.0.18", {"center": v(101, 66) * mm, "radius": 1.5 * mm});
            skCircle(sketch, "E44.10.0.19", {"center": v(-144, 66) * mm, "radius": 1.5 * mm});
            skCircle(sketch, "E44.10.0.20", {"center": v(71, 66) * mm, "radius": 1.5 * mm});
            skCircle(sketch, "E44.10.0.21", {"center": v(-69, 66) * mm, "radius": 1.5 * mm});
            skCircle(sketch, "E44.10.0.22", {"center": v(-84, 66) * mm, "radius": 1.5 * mm});
            skCircle(sketch, "E44.10.0.23", {"center": v(116, 66) * mm, "radius": 1.5 * mm});
            skCircle(sketch, "E44.10.0.24", {"center": v(-164, 66) * mm, "radius": 1.5 * mm});
            skCircle(sketch, "E44.10.0.25", {"center": v(86, 66) * mm, "radius": 1.5 * mm});
            skCircle(sketch, "E44.10.0.26", {"center": v(-149, 66) * mm, "radius": 1.5 * mm});
            skCircle(sketch, "E44.10.0.27", {"center": v(106, 66) * mm, "radius": 1.5 * mm});
            skCircle(sketch, "E44.10.0.28", {"center": v(-94, 66) * mm, "radius": 1.5 * mm});
            skCircle(sketch, "E44.10.0.29", {"center": v(-129, 66) * mm, "radius": 1.5 * mm});
            skCircle(sketch, "E44.10.0.30", {"center": v(-19, 66) * mm, "radius": 1.5 * mm});
            skCircle(sketch, "E44.10.0.31", {"center": v(-49, 66) * mm, "radius": 1.5 * mm});
            skCircle(sketch, "E44.10.0.32", {"center": v(26, 66) * mm, "radius": 1.5 * mm});
            skCircle(sketch, "E44.10.0.33", {"center": v(61, 66) * mm, "radius": 1.5 * mm});
            skCircle(sketch, "E44.10.0.34", {"center": v(16, 66) * mm, "radius": 1.5 * mm});
            skCircle(sketch, "E44.10.0.35", {"center": v(96, 66) * mm, "radius": 1.5 * mm});
            skCircle(sketch, "E44.10.0.36", {"center": v(-139, 66) * mm, "radius": 1.5 * mm});
            skCircle(sketch, "E44.10.0.37", {"center": v(-59, 66) * mm, "radius": 1.5 * mm});
            skCircle(sketch, "E44.10.0.38", {"center": v(111, 66) * mm, "radius": 1.5 * mm});
            skCircle(sketch, "E44.10.0.39", {"center": v(146, 66) * mm, "radius": 1.5 * mm});
            skCircle(sketch, "E44.10.0.40", {"center": v(-89, 66) * mm, "radius": 1.5 * mm});
            skCircle(sketch, "E44.10.0.41", {"center": v(-44, 66) * mm, "radius": 1.5 * mm});
            skCircle(sketch, "E44.10.0.42", {"center": v(-124, 66) * mm, "radius": 1.5 * mm});
            skCircle(sketch, "E44.10.0.43", {"center": v(-14, 66) * mm, "radius": 1.5 * mm});
            skCircle(sketch, "E44.10.0.44", {"center": v(31, 66) * mm, "radius": 1.5 * mm});
            skCircle(sketch, "E44.10.0.45", {"center": v(66, 66) * mm, "radius": 1.5 * mm});
            skCircle(sketch, "E44.10.0.46", {"center": v(141, 66) * mm, "radius": 1.5 * mm});
            skCircle(sketch, "E44.10.0.47", {"center": v(36, 66) * mm, "radius": 1.5 * mm});
            skCircle(sketch, "E44.10.0.48", {"center": v(-39, 66) * mm, "radius": 1.5 * mm});
            skCircle(sketch, "E44.10.0.49", {"center": v(-119, 66) * mm, "radius": 1.5 * mm});
            skCircle(sketch, "E44.10.0.50", {"center": v(-79, 66) * mm, "radius": 1.5 * mm});
            skCircle(sketch, "E44.10.0.51", {"center": v(-159, 66) * mm, "radius": 1.5 * mm});
            skCircle(sketch, "E44.10.0.52", {"center": v(156, 66) * mm, "radius": 1.5 * mm});
            skCircle(sketch, "E44.10.0.53", {"center": v(76, 66) * mm, "radius": 1.5 * mm});
            skCircle(sketch, "E44.10.0.54", {"center": v(-4, 66) * mm, "radius": 1.5 * mm});
            skCircle(sketch, "E44.10.0.55", {"center": v(41, 66) * mm, "radius": 1.5 * mm});
            skCircle(sketch, "E44.10.0.56", {"center": v(-34, 66) * mm, "radius": 1.5 * mm});
            skCircle(sketch, "E44.10.0.57", {"center": v(-114, 66) * mm, "radius": 1.5 * mm});
            skCircle(sketch, "E44.10.0.58", {"center": v(121, 66) * mm, "radius": 1.5 * mm});
            skCircle(sketch, "E44.10.0.59", {"center": v(-74, 66) * mm, "radius": 1.5 * mm});
            skCircle(sketch, "E44.10.0.60", {"center": v(-154, 66) * mm, "radius": 1.5 * mm});
            skCircle(sketch, "E44.10.0.61", {"center": v(161, 66) * mm, "radius": 1.5 * mm});
            skCircle(sketch, "E44.10.0.62", {"center": v(81, 66) * mm, "radius": 1.5 * mm});
            skCircle(sketch, "E44.10.0.63", {"center": v(1, 66) * mm, "radius": 1.5 * mm});
            skCircle(sketch, "E44.10.0.64", {"center": v(46, 66) * mm, "radius": 1.5 * mm});
            skCircle(sketch, "E44.10.0.65", {"center": v(-29, 66) * mm, "radius": 1.5 * mm});
            skCircle(sketch, "E44.10.0.66", {"center": v(-109, 66) * mm, "radius": 1.5 * mm});
            skCircle(sketch, "E44.10.0.67", {"center": v(126, 66) * mm, "radius": 1.5 * mm});
            skLineSegment(sketch, "E44.10.0.68", {"start": v(-174, 66) * mm, "end": v(-169, 66) * mm, "construction": true});
            skCircle(sketch, "E44.10.0.69", {"center": v(-174, 66) * mm, "radius": 1.5 * mm});
            skCircle(sketch, "E44.10.0.70", {"center": v(-169, 66) * mm, "radius": 1.5 * mm});
            skCircle(sketch, "E44.11.0.0", {"center": v(166, 61) * mm, "radius": 1.5 * mm});
            skCircle(sketch, "E44.11.0.1", {"center": v(21, 61) * mm, "radius": 1.5 * mm});
            skCircle(sketch, "E44.11.0.2", {"center": v(-99, 61) * mm, "radius": 1.5 * mm});
            skCircle(sketch, "E44.11.0.3", {"center": v(6, 61) * mm, "radius": 1.5 * mm});
            skCircle(sketch, "E44.11.0.4", {"center": v(-54, 61) * mm, "radius": 1.5 * mm});
            skCircle(sketch, "E44.11.0.5", {"center": v(171, 61) * mm, "radius": 1.5 * mm});
            skCircle(sketch, "E44.11.0.6", {"center": v(-104, 61) * mm, "radius": 1.5 * mm});
            skCircle(sketch, "E44.11.0.7", {"center": v(11, 61) * mm, "radius": 1.5 * mm});
            skCircle(sketch, "E44.11.0.8", {"center": v(56, 61) * mm, "radius": 1.5 * mm});
            skCircle(sketch, "E44.11.0.9", {"center": v(-134, 61) * mm, "radius": 1.5 * mm});
            skCircle(sketch, "E44.11.0.10", {"center": v(51, 61) * mm, "radius": 1.5 * mm});
            skCircle(sketch, "E44.11.0.11", {"center": v(131, 61) * mm, "radius": 1.5 * mm});
            skCircle(sketch, "E44.11.0.12", {"center": v(151, 61) * mm, "radius": 1.5 * mm});
            skCircle(sketch, "E44.11.0.13", {"center": v(-24, 61) * mm, "radius": 1.5 * mm});
            skCircle(sketch, "E44.11.0.14", {"center": v(-64, 61) * mm, "radius": 1.5 * mm});
            skCircle(sketch, "E44.11.0.15", {"center": v(-9, 61) * mm, "radius": 1.5 * mm});
            skCircle(sketch, "E44.11.0.16", {"center": v(136, 61) * mm, "radius": 1.5 * mm});
            skCircle(sketch, "E44.11.0.17", {"center": v(91, 61) * mm, "radius": 1.5 * mm});
            skCircle(sketch, "E44.11.0.18", {"center": v(101, 61) * mm, "radius": 1.5 * mm});
            skCircle(sketch, "E44.11.0.19", {"center": v(-144, 61) * mm, "radius": 1.5 * mm});
            skCircle(sketch, "E44.11.0.20", {"center": v(71, 61) * mm, "radius": 1.5 * mm});
            skCircle(sketch, "E44.11.0.21", {"center": v(-69, 61) * mm, "radius": 1.5 * mm});
            skCircle(sketch, "E44.11.0.22", {"center": v(-84, 61) * mm, "radius": 1.5 * mm});
            skCircle(sketch, "E44.11.0.23", {"center": v(116, 61) * mm, "radius": 1.5 * mm});
            skCircle(sketch, "E44.11.0.24", {"center": v(-164, 61) * mm, "radius": 1.5 * mm});
            skCircle(sketch, "E44.11.0.25", {"center": v(86, 61) * mm, "radius": 1.5 * mm});
            skCircle(sketch, "E44.11.0.26", {"center": v(-149, 61) * mm, "radius": 1.5 * mm});
            skCircle(sketch, "E44.11.0.27", {"center": v(106, 61) * mm, "radius": 1.5 * mm});
            skCircle(sketch, "E44.11.0.28", {"center": v(-94, 61) * mm, "radius": 1.5 * mm});
            skCircle(sketch, "E44.11.0.29", {"center": v(-129, 61) * mm, "radius": 1.5 * mm});
            skCircle(sketch, "E44.11.0.30", {"center": v(-19, 61) * mm, "radius": 1.5 * mm});
            skCircle(sketch, "E44.11.0.31", {"center": v(-49, 61) * mm, "radius": 1.5 * mm});
            skCircle(sketch, "E44.11.0.32", {"center": v(26, 61) * mm, "radius": 1.5 * mm});
            skCircle(sketch, "E44.11.0.33", {"center": v(61, 61) * mm, "radius": 1.5 * mm});
            skCircle(sketch, "E44.11.0.34", {"center": v(16, 61) * mm, "radius": 1.5 * mm});
            skCircle(sketch, "E44.11.0.35", {"center": v(96, 61) * mm, "radius": 1.5 * mm});
            skCircle(sketch, "E44.11.0.36", {"center": v(-139, 61) * mm, "radius": 1.5 * mm});
            skCircle(sketch, "E44.11.0.37", {"center": v(-59, 61) * mm, "radius": 1.5 * mm});
            skCircle(sketch, "E44.11.0.38", {"center": v(111, 61) * mm, "radius": 1.5 * mm});
            skCircle(sketch, "E44.11.0.39", {"center": v(146, 61) * mm, "radius": 1.5 * mm});
            skCircle(sketch, "E44.11.0.40", {"center": v(-89, 61) * mm, "radius": 1.5 * mm});
            skCircle(sketch, "E44.11.0.41", {"center": v(-44, 61) * mm, "radius": 1.5 * mm});
            skCircle(sketch, "E44.11.0.42", {"center": v(-124, 61) * mm, "radius": 1.5 * mm});
            skCircle(sketch, "E44.11.0.43", {"center": v(-14, 61) * mm, "radius": 1.5 * mm});
            skCircle(sketch, "E44.11.0.44", {"center": v(31, 61) * mm, "radius": 1.5 * mm});
            skCircle(sketch, "E44.11.0.45", {"center": v(66, 61) * mm, "radius": 1.5 * mm});
            skCircle(sketch, "E44.11.0.46", {"center": v(141, 61) * mm, "radius": 1.5 * mm});
            skCircle(sketch, "E44.11.0.47", {"center": v(36, 61) * mm, "radius": 1.5 * mm});
            skCircle(sketch, "E44.11.0.48", {"center": v(-39, 61) * mm, "radius": 1.5 * mm});
            skCircle(sketch, "E44.11.0.49", {"center": v(-119, 61) * mm, "radius": 1.5 * mm});
            skCircle(sketch, "E44.11.0.50", {"center": v(-79, 61) * mm, "radius": 1.5 * mm});
            skCircle(sketch, "E44.11.0.51", {"center": v(-159, 61) * mm, "radius": 1.5 * mm});
            skCircle(sketch, "E44.11.0.52", {"center": v(156, 61) * mm, "radius": 1.5 * mm});
            skCircle(sketch, "E44.11.0.53", {"center": v(76, 61) * mm, "radius": 1.5 * mm});
            skCircle(sketch, "E44.11.0.54", {"center": v(-4, 61) * mm, "radius": 1.5 * mm});
            skCircle(sketch, "E44.11.0.55", {"center": v(41, 61) * mm, "radius": 1.5 * mm});
            skCircle(sketch, "E44.11.0.56", {"center": v(-34, 61) * mm, "radius": 1.5 * mm});
            skCircle(sketch, "E44.11.0.57", {"center": v(-114, 61) * mm, "radius": 1.5 * mm});
            skCircle(sketch, "E44.11.0.58", {"center": v(121, 61) * mm, "radius": 1.5 * mm});
            skCircle(sketch, "E44.11.0.59", {"center": v(-74, 61) * mm, "radius": 1.5 * mm});
            skCircle(sketch, "E44.11.0.60", {"center": v(-154, 61) * mm, "radius": 1.5 * mm});
            skCircle(sketch, "E44.11.0.61", {"center": v(161, 61) * mm, "radius": 1.5 * mm});
            skCircle(sketch, "E44.11.0.62", {"center": v(81, 61) * mm, "radius": 1.5 * mm});
            skCircle(sketch, "E44.11.0.63", {"center": v(1, 61) * mm, "radius": 1.5 * mm});
            skCircle(sketch, "E44.11.0.64", {"center": v(46, 61) * mm, "radius": 1.5 * mm});
            skCircle(sketch, "E44.11.0.65", {"center": v(-29, 61) * mm, "radius": 1.5 * mm});
            skCircle(sketch, "E44.11.0.66", {"center": v(-109, 61) * mm, "radius": 1.5 * mm});
            skCircle(sketch, "E44.11.0.67", {"center": v(126, 61) * mm, "radius": 1.5 * mm});
            skLineSegment(sketch, "E44.11.0.68", {"start": v(-174, 61) * mm, "end": v(-169, 61) * mm, "construction": true});
            skCircle(sketch, "E44.11.0.69", {"center": v(-174, 61) * mm, "radius": 1.5 * mm});
            skCircle(sketch, "E44.11.0.70", {"center": v(-169, 61) * mm, "radius": 1.5 * mm});
            skCircle(sketch, "E44.12.0.0", {"center": v(166, 56) * mm, "radius": 1.5 * mm});
            skCircle(sketch, "E44.12.0.1", {"center": v(21, 56) * mm, "radius": 1.5 * mm});
            skCircle(sketch, "E44.12.0.2", {"center": v(-99, 56) * mm, "radius": 1.5 * mm});
            skCircle(sketch, "E44.12.0.3", {"center": v(6, 56) * mm, "radius": 1.5 * mm});
            skCircle(sketch, "E44.12.0.4", {"center": v(-54, 56) * mm, "radius": 1.5 * mm});
            skCircle(sketch, "E44.12.0.5", {"center": v(171, 56) * mm, "radius": 1.5 * mm});
            skCircle(sketch, "E44.12.0.6", {"center": v(-104, 56) * mm, "radius": 1.5 * mm});
            skCircle(sketch, "E44.12.0.7", {"center": v(11, 56) * mm, "radius": 1.5 * mm});
            skCircle(sketch, "E44.12.0.8", {"center": v(56, 56) * mm, "radius": 1.5 * mm});
            skCircle(sketch, "E44.12.0.9", {"center": v(-134, 56) * mm, "radius": 1.5 * mm});
            skCircle(sketch, "E44.12.0.10", {"center": v(51, 56) * mm, "radius": 1.5 * mm});
            skCircle(sketch, "E44.12.0.11", {"center": v(131, 56) * mm, "radius": 1.5 * mm});
            skCircle(sketch, "E44.12.0.12", {"center": v(151, 56) * mm, "radius": 1.5 * mm});
            skCircle(sketch, "E44.12.0.13", {"center": v(-24, 56) * mm, "radius": 1.5 * mm});
            skCircle(sketch, "E44.12.0.14", {"center": v(-64, 56) * mm, "radius": 1.5 * mm});
            skCircle(sketch, "E44.12.0.15", {"center": v(-9, 56) * mm, "radius": 1.5 * mm});
            skCircle(sketch, "E44.12.0.16", {"center": v(136, 56) * mm, "radius": 1.5 * mm});
            skCircle(sketch, "E44.12.0.17", {"center": v(91, 56) * mm, "radius": 1.5 * mm});
            skCircle(sketch, "E44.12.0.18", {"center": v(101, 56) * mm, "radius": 1.5 * mm});
            skCircle(sketch, "E44.12.0.19", {"center": v(-144, 56) * mm, "radius": 1.5 * mm});
            skCircle(sketch, "E44.12.0.20", {"center": v(71, 56) * mm, "radius": 1.5 * mm});
            skCircle(sketch, "E44.12.0.21", {"center": v(-69, 56) * mm, "radius": 1.5 * mm});
            skCircle(sketch, "E44.12.0.22", {"center": v(-84, 56) * mm, "radius": 1.5 * mm});
            skCircle(sketch, "E44.12.0.23", {"center": v(116, 56) * mm, "radius": 1.5 * mm});
            skCircle(sketch, "E44.12.0.24", {"center": v(-164, 56) * mm, "radius": 1.5 * mm});
            skCircle(sketch, "E44.12.0.25", {"center": v(86, 56) * mm, "radius": 1.5 * mm});
            skCircle(sketch, "E44.12.0.26", {"center": v(-149, 56) * mm, "radius": 1.5 * mm});
            skCircle(sketch, "E44.12.0.27", {"center": v(106, 56) * mm, "radius": 1.5 * mm});
            skCircle(sketch, "E44.12.0.28", {"center": v(-94, 56) * mm, "radius": 1.5 * mm});
            skCircle(sketch, "E44.12.0.29", {"center": v(-129, 56) * mm, "radius": 1.5 * mm});
            skCircle(sketch, "E44.12.0.30", {"center": v(-19, 56) * mm, "radius": 1.5 * mm});
            skCircle(sketch, "E44.12.0.31", {"center": v(-49, 56) * mm, "radius": 1.5 * mm});
            skCircle(sketch, "E44.12.0.32", {"center": v(26, 56) * mm, "radius": 1.5 * mm});
            skCircle(sketch, "E44.12.0.33", {"center": v(61, 56) * mm, "radius": 1.5 * mm});
            skCircle(sketch, "E44.12.0.34", {"center": v(16, 56) * mm, "radius": 1.5 * mm});
            skCircle(sketch, "E44.12.0.35", {"center": v(96, 56) * mm, "radius": 1.5 * mm});
            skCircle(sketch, "E44.12.0.36", {"center": v(-139, 56) * mm, "radius": 1.5 * mm});
            skCircle(sketch, "E44.12.0.37", {"center": v(-59, 56) * mm, "radius": 1.5 * mm});
            skCircle(sketch, "E44.12.0.38", {"center": v(111, 56) * mm, "radius": 1.5 * mm});
            skCircle(sketch, "E44.12.0.39", {"center": v(146, 56) * mm, "radius": 1.5 * mm});
            skCircle(sketch, "E44.12.0.40", {"center": v(-89, 56) * mm, "radius": 1.5 * mm});
            skCircle(sketch, "E44.12.0.41", {"center": v(-44, 56) * mm, "radius": 1.5 * mm});
            skCircle(sketch, "E44.12.0.42", {"center": v(-124, 56) * mm, "radius": 1.5 * mm});
            skCircle(sketch, "E44.12.0.43", {"center": v(-14, 56) * mm, "radius": 1.5 * mm});
            skCircle(sketch, "E44.12.0.44", {"center": v(31, 56) * mm, "radius": 1.5 * mm});
            skCircle(sketch, "E44.12.0.45", {"center": v(66, 56) * mm, "radius": 1.5 * mm});
            skCircle(sketch, "E44.12.0.46", {"center": v(141, 56) * mm, "radius": 1.5 * mm});
            skCircle(sketch, "E44.12.0.47", {"center": v(36, 56) * mm, "radius": 1.5 * mm});
            skCircle(sketch, "E44.12.0.48", {"center": v(-39, 56) * mm, "radius": 1.5 * mm});
            skCircle(sketch, "E44.12.0.49", {"center": v(-119, 56) * mm, "radius": 1.5 * mm});
            skCircle(sketch, "E44.12.0.50", {"center": v(-79, 56) * mm, "radius": 1.5 * mm});
            skCircle(sketch, "E44.12.0.51", {"center": v(-159, 56) * mm, "radius": 1.5 * mm});
            skCircle(sketch, "E44.12.0.52", {"center": v(156, 56) * mm, "radius": 1.5 * mm});
            skCircle(sketch, "E44.12.0.53", {"center": v(76, 56) * mm, "radius": 1.5 * mm});
            skCircle(sketch, "E44.12.0.54", {"center": v(-4, 56) * mm, "radius": 1.5 * mm});
            skCircle(sketch, "E44.12.0.55", {"center": v(41, 56) * mm, "radius": 1.5 * mm});
            skCircle(sketch, "E44.12.0.56", {"center": v(-34, 56) * mm, "radius": 1.5 * mm});
            skCircle(sketch, "E44.12.0.57", {"center": v(-114, 56) * mm, "radius": 1.5 * mm});
            skCircle(sketch, "E44.12.0.58", {"center": v(121, 56) * mm, "radius": 1.5 * mm});
            skCircle(sketch, "E44.12.0.59", {"center": v(-74, 56) * mm, "radius": 1.5 * mm});
            skCircle(sketch, "E44.12.0.60", {"center": v(-154, 56) * mm, "radius": 1.5 * mm});
            skCircle(sketch, "E44.12.0.61", {"center": v(161, 56) * mm, "radius": 1.5 * mm});
            skCircle(sketch, "E44.12.0.62", {"center": v(81, 56) * mm, "radius": 1.5 * mm});
            skCircle(sketch, "E44.12.0.63", {"center": v(1, 56) * mm, "radius": 1.5 * mm});
            skCircle(sketch, "E44.12.0.64", {"center": v(46, 56) * mm, "radius": 1.5 * mm});
            skCircle(sketch, "E44.12.0.65", {"center": v(-29, 56) * mm, "radius": 1.5 * mm});
            skCircle(sketch, "E44.12.0.66", {"center": v(-109, 56) * mm, "radius": 1.5 * mm});
            skCircle(sketch, "E44.12.0.67", {"center": v(126, 56) * mm, "radius": 1.5 * mm});
            skLineSegment(sketch, "E44.12.0.68", {"start": v(-174, 56) * mm, "end": v(-169, 56) * mm, "construction": true});
            skCircle(sketch, "E44.12.0.69", {"center": v(-174, 56) * mm, "radius": 1.5 * mm});
            skCircle(sketch, "E44.12.0.70", {"center": v(-169, 56) * mm, "radius": 1.5 * mm});
            skCircle(sketch, "E44.13.0.0", {"center": v(166, 51) * mm, "radius": 1.5 * mm});
            skCircle(sketch, "E44.13.0.1", {"center": v(21, 51) * mm, "radius": 1.5 * mm});
            skCircle(sketch, "E44.13.0.2", {"center": v(-99, 51) * mm, "radius": 1.5 * mm});
            skCircle(sketch, "E44.13.0.3", {"center": v(6, 51) * mm, "radius": 1.5 * mm});
            skCircle(sketch, "E44.13.0.4", {"center": v(-54, 51) * mm, "radius": 1.5 * mm});
            skCircle(sketch, "E44.13.0.5", {"center": v(171, 51) * mm, "radius": 1.5 * mm});
            skCircle(sketch, "E44.13.0.6", {"center": v(-104, 51) * mm, "radius": 1.5 * mm});
            skCircle(sketch, "E44.13.0.7", {"center": v(11, 51) * mm, "radius": 1.5 * mm});
            skCircle(sketch, "E44.13.0.8", {"center": v(56, 51) * mm, "radius": 1.5 * mm});
            skCircle(sketch, "E44.13.0.9", {"center": v(-134, 51) * mm, "radius": 1.5 * mm});
            skCircle(sketch, "E44.13.0.10", {"center": v(51, 51) * mm, "radius": 1.5 * mm});
            skCircle(sketch, "E44.13.0.11", {"center": v(131, 51) * mm, "radius": 1.5 * mm});
            skCircle(sketch, "E44.13.0.12", {"center": v(151, 51) * mm, "radius": 1.5 * mm});
            skCircle(sketch, "E44.13.0.13", {"center": v(-24, 51) * mm, "radius": 1.5 * mm});
            skCircle(sketch, "E44.13.0.14", {"center": v(-64, 51) * mm, "radius": 1.5 * mm});
            skCircle(sketch, "E44.13.0.15", {"center": v(-9, 51) * mm, "radius": 1.5 * mm});
            skCircle(sketch, "E44.13.0.16", {"center": v(136, 51) * mm, "radius": 1.5 * mm});
            skCircle(sketch, "E44.13.0.17", {"center": v(91, 51) * mm, "radius": 1.5 * mm});
            skCircle(sketch, "E44.13.0.18", {"center": v(101, 51) * mm, "radius": 1.5 * mm});
            skCircle(sketch, "E44.13.0.19", {"center": v(-144, 51) * mm, "radius": 1.5 * mm});
            skCircle(sketch, "E44.13.0.20", {"center": v(71, 51) * mm, "radius": 1.5 * mm});
            skCircle(sketch, "E44.13.0.21", {"center": v(-69, 51) * mm, "radius": 1.5 * mm});
            skCircle(sketch, "E44.13.0.22", {"center": v(-84, 51) * mm, "radius": 1.5 * mm});
            skCircle(sketch, "E44.13.0.23", {"center": v(116, 51) * mm, "radius": 1.5 * mm});
            skCircle(sketch, "E44.13.0.24", {"center": v(-164, 51) * mm, "radius": 1.5 * mm});
            skCircle(sketch, "E44.13.0.25", {"center": v(86, 51) * mm, "radius": 1.5 * mm});
            skCircle(sketch, "E44.13.0.26", {"center": v(-149, 51) * mm, "radius": 1.5 * mm});
            skCircle(sketch, "E44.13.0.27", {"center": v(106, 51) * mm, "radius": 1.5 * mm});
            skCircle(sketch, "E44.13.0.28", {"center": v(-94, 51) * mm, "radius": 1.5 * mm});
            skCircle(sketch, "E44.13.0.29", {"center": v(-129, 51) * mm, "radius": 1.5 * mm});
            skCircle(sketch, "E44.13.0.30", {"center": v(-19, 51) * mm, "radius": 1.5 * mm});
            skCircle(sketch, "E44.13.0.31", {"center": v(-49, 51) * mm, "radius": 1.5 * mm});
            skCircle(sketch, "E44.13.0.32", {"center": v(26, 51) * mm, "radius": 1.5 * mm});
            skCircle(sketch, "E44.13.0.33", {"center": v(61, 51) * mm, "radius": 1.5 * mm});
            skCircle(sketch, "E44.13.0.34", {"center": v(16, 51) * mm, "radius": 1.5 * mm});
            skCircle(sketch, "E44.13.0.35", {"center": v(96, 51) * mm, "radius": 1.5 * mm});
            skCircle(sketch, "E44.13.0.36", {"center": v(-139, 51) * mm, "radius": 1.5 * mm});
            skCircle(sketch, "E44.13.0.37", {"center": v(-59, 51) * mm, "radius": 1.5 * mm});
            skCircle(sketch, "E44.13.0.38", {"center": v(111, 51) * mm, "radius": 1.5 * mm});
            skCircle(sketch, "E44.13.0.39", {"center": v(146, 51) * mm, "radius": 1.5 * mm});
            skCircle(sketch, "E44.13.0.40", {"center": v(-89, 51) * mm, "radius": 1.5 * mm});
            skCircle(sketch, "E44.13.0.41", {"center": v(-44, 51) * mm, "radius": 1.5 * mm});
            skCircle(sketch, "E44.13.0.42", {"center": v(-124, 51) * mm, "radius": 1.5 * mm});
            skCircle(sketch, "E44.13.0.43", {"center": v(-14, 51) * mm, "radius": 1.5 * mm});
            skCircle(sketch, "E44.13.0.44", {"center": v(31, 51) * mm, "radius": 1.5 * mm});
            skCircle(sketch, "E44.13.0.45", {"center": v(66, 51) * mm, "radius": 1.5 * mm});
            skCircle(sketch, "E44.13.0.46", {"center": v(141, 51) * mm, "radius": 1.5 * mm});
            skCircle(sketch, "E44.13.0.47", {"center": v(36, 51) * mm, "radius": 1.5 * mm});
            skCircle(sketch, "E44.13.0.48", {"center": v(-39, 51) * mm, "radius": 1.5 * mm});
            skCircle(sketch, "E44.13.0.49", {"center": v(-119, 51) * mm, "radius": 1.5 * mm});
            skCircle(sketch, "E44.13.0.50", {"center": v(-79, 51) * mm, "radius": 1.5 * mm});
            skCircle(sketch, "E44.13.0.51", {"center": v(-159, 51) * mm, "radius": 1.5 * mm});
            skCircle(sketch, "E44.13.0.52", {"center": v(156, 51) * mm, "radius": 1.5 * mm});
            skCircle(sketch, "E44.13.0.53", {"center": v(76, 51) * mm, "radius": 1.5 * mm});
            skCircle(sketch, "E44.13.0.54", {"center": v(-4, 51) * mm, "radius": 1.5 * mm});
            skCircle(sketch, "E44.13.0.55", {"center": v(41, 51) * mm, "radius": 1.5 * mm});
            skCircle(sketch, "E44.13.0.56", {"center": v(-34, 51) * mm, "radius": 1.5 * mm});
            skCircle(sketch, "E44.13.0.57", {"center": v(-114, 51) * mm, "radius": 1.5 * mm});
            skCircle(sketch, "E44.13.0.58", {"center": v(121, 51) * mm, "radius": 1.5 * mm});
            skCircle(sketch, "E44.13.0.59", {"center": v(-74, 51) * mm, "radius": 1.5 * mm});
            skCircle(sketch, "E44.13.0.60", {"center": v(-154, 51) * mm, "radius": 1.5 * mm});
            skCircle(sketch, "E44.13.0.61", {"center": v(161, 51) * mm, "radius": 1.5 * mm});
            skCircle(sketch, "E44.13.0.62", {"center": v(81, 51) * mm, "radius": 1.5 * mm});
            skCircle(sketch, "E44.13.0.63", {"center": v(1, 51) * mm, "radius": 1.5 * mm});
            skCircle(sketch, "E44.13.0.64", {"center": v(46, 51) * mm, "radius": 1.5 * mm});
            skCircle(sketch, "E44.13.0.65", {"center": v(-29, 51) * mm, "radius": 1.5 * mm});
            skCircle(sketch, "E44.13.0.66", {"center": v(-109, 51) * mm, "radius": 1.5 * mm});
            skCircle(sketch, "E44.13.0.67", {"center": v(126, 51) * mm, "radius": 1.5 * mm});
            skLineSegment(sketch, "E44.13.0.68", {"start": v(-174, 51) * mm, "end": v(-169, 51) * mm, "construction": true});
            skCircle(sketch, "E44.13.0.69", {"center": v(-174, 51) * mm, "radius": 1.5 * mm});
            skCircle(sketch, "E44.13.0.70", {"center": v(-169, 51) * mm, "radius": 1.5 * mm});
            skCircle(sketch, "E44.14.0.0", {"center": v(166, 46) * mm, "radius": 1.5 * mm});
            skCircle(sketch, "E44.14.0.1", {"center": v(21, 46) * mm, "radius": 1.5 * mm});
            skCircle(sketch, "E44.14.0.2", {"center": v(-99, 46) * mm, "radius": 1.5 * mm});
            skCircle(sketch, "E44.14.0.3", {"center": v(6, 46) * mm, "radius": 1.5 * mm});
            skCircle(sketch, "E44.14.0.4", {"center": v(-54, 46) * mm, "radius": 1.5 * mm});
            skCircle(sketch, "E44.14.0.5", {"center": v(171, 46) * mm, "radius": 1.5 * mm});
            skCircle(sketch, "E44.14.0.6", {"center": v(-104, 46) * mm, "radius": 1.5 * mm});
            skCircle(sketch, "E44.14.0.7", {"center": v(11, 46) * mm, "radius": 1.5 * mm});
            skCircle(sketch, "E44.14.0.8", {"center": v(56, 46) * mm, "radius": 1.5 * mm});
            skCircle(sketch, "E44.14.0.9", {"center": v(-134, 46) * mm, "radius": 1.5 * mm});
            skCircle(sketch, "E44.14.0.10", {"center": v(51, 46) * mm, "radius": 1.5 * mm});
            skCircle(sketch, "E44.14.0.11", {"center": v(131, 46) * mm, "radius": 1.5 * mm});
            skCircle(sketch, "E44.14.0.12", {"center": v(151, 46) * mm, "radius": 1.5 * mm});
            skCircle(sketch, "E44.14.0.13", {"center": v(-24, 46) * mm, "radius": 1.5 * mm});
            skCircle(sketch, "E44.14.0.14", {"center": v(-64, 46) * mm, "radius": 1.5 * mm});
            skCircle(sketch, "E44.14.0.15", {"center": v(-9, 46) * mm, "radius": 1.5 * mm});
            skCircle(sketch, "E44.14.0.16", {"center": v(136, 46) * mm, "radius": 1.5 * mm});
            skCircle(sketch, "E44.14.0.17", {"center": v(91, 46) * mm, "radius": 1.5 * mm});
            skCircle(sketch, "E44.14.0.18", {"center": v(101, 46) * mm, "radius": 1.5 * mm});
            skCircle(sketch, "E44.14.0.19", {"center": v(-144, 46) * mm, "radius": 1.5 * mm});
            skCircle(sketch, "E44.14.0.20", {"center": v(71, 46) * mm, "radius": 1.5 * mm});
            skCircle(sketch, "E44.14.0.21", {"center": v(-69, 46) * mm, "radius": 1.5 * mm});
            skCircle(sketch, "E44.14.0.22", {"center": v(-84, 46) * mm, "radius": 1.5 * mm});
            skCircle(sketch, "E44.14.0.23", {"center": v(116, 46) * mm, "radius": 1.5 * mm});
            skCircle(sketch, "E44.14.0.24", {"center": v(-164, 46) * mm, "radius": 1.5 * mm});
            skCircle(sketch, "E44.14.0.25", {"center": v(86, 46) * mm, "radius": 1.5 * mm});
            skCircle(sketch, "E44.14.0.26", {"center": v(-149, 46) * mm, "radius": 1.5 * mm});
            skCircle(sketch, "E44.14.0.27", {"center": v(106, 46) * mm, "radius": 1.5 * mm});
            skCircle(sketch, "E44.14.0.28", {"center": v(-94, 46) * mm, "radius": 1.5 * mm});
            skCircle(sketch, "E44.14.0.29", {"center": v(-129, 46) * mm, "radius": 1.5 * mm});
            skCircle(sketch, "E44.14.0.30", {"center": v(-19, 46) * mm, "radius": 1.5 * mm});
            skCircle(sketch, "E44.14.0.31", {"center": v(-49, 46) * mm, "radius": 1.5 * mm});
            skCircle(sketch, "E44.14.0.32", {"center": v(26, 46) * mm, "radius": 1.5 * mm});
            skCircle(sketch, "E44.14.0.33", {"center": v(61, 46) * mm, "radius": 1.5 * mm});
            skCircle(sketch, "E44.14.0.34", {"center": v(16, 46) * mm, "radius": 1.5 * mm});
            skCircle(sketch, "E44.14.0.35", {"center": v(96, 46) * mm, "radius": 1.5 * mm});
            skCircle(sketch, "E44.14.0.36", {"center": v(-139, 46) * mm, "radius": 1.5 * mm});
            skCircle(sketch, "E44.14.0.37", {"center": v(-59, 46) * mm, "radius": 1.5 * mm});
            skCircle(sketch, "E44.14.0.38", {"center": v(111, 46) * mm, "radius": 1.5 * mm});
            skCircle(sketch, "E44.14.0.39", {"center": v(146, 46) * mm, "radius": 1.5 * mm});
            skCircle(sketch, "E44.14.0.40", {"center": v(-89, 46) * mm, "radius": 1.5 * mm});
            skCircle(sketch, "E44.14.0.41", {"center": v(-44, 46) * mm, "radius": 1.5 * mm});
            skCircle(sketch, "E44.14.0.42", {"center": v(-124, 46) * mm, "radius": 1.5 * mm});
            skCircle(sketch, "E44.14.0.43", {"center": v(-14, 46) * mm, "radius": 1.5 * mm});
            skCircle(sketch, "E44.14.0.44", {"center": v(31, 46) * mm, "radius": 1.5 * mm});
            skCircle(sketch, "E44.14.0.45", {"center": v(66, 46) * mm, "radius": 1.5 * mm});
            skCircle(sketch, "E44.14.0.46", {"center": v(141, 46) * mm, "radius": 1.5 * mm});
            skCircle(sketch, "E44.14.0.47", {"center": v(36, 46) * mm, "radius": 1.5 * mm});
            skCircle(sketch, "E44.14.0.48", {"center": v(-39, 46) * mm, "radius": 1.5 * mm});
            skCircle(sketch, "E44.14.0.49", {"center": v(-119, 46) * mm, "radius": 1.5 * mm});
            skCircle(sketch, "E44.14.0.50", {"center": v(-79, 46) * mm, "radius": 1.5 * mm});
            skCircle(sketch, "E44.14.0.51", {"center": v(-159, 46) * mm, "radius": 1.5 * mm});
            skCircle(sketch, "E44.14.0.52", {"center": v(156, 46) * mm, "radius": 1.5 * mm});
            skCircle(sketch, "E44.14.0.53", {"center": v(76, 46) * mm, "radius": 1.5 * mm});
            skCircle(sketch, "E44.14.0.54", {"center": v(-4, 46) * mm, "radius": 1.5 * mm});
            skCircle(sketch, "E44.14.0.55", {"center": v(41, 46) * mm, "radius": 1.5 * mm});
            skCircle(sketch, "E44.14.0.56", {"center": v(-34, 46) * mm, "radius": 1.5 * mm});
            skCircle(sketch, "E44.14.0.57", {"center": v(-114, 46) * mm, "radius": 1.5 * mm});
            skCircle(sketch, "E44.14.0.58", {"center": v(121, 46) * mm, "radius": 1.5 * mm});
            skCircle(sketch, "E44.14.0.59", {"center": v(-74, 46) * mm, "radius": 1.5 * mm});
            skCircle(sketch, "E44.14.0.60", {"center": v(-154, 46) * mm, "radius": 1.5 * mm});
            skCircle(sketch, "E44.14.0.61", {"center": v(161, 46) * mm, "radius": 1.5 * mm});
            skCircle(sketch, "E44.14.0.62", {"center": v(81, 46) * mm, "radius": 1.5 * mm});
            skCircle(sketch, "E44.14.0.63", {"center": v(1, 46) * mm, "radius": 1.5 * mm});
            skCircle(sketch, "E44.14.0.64", {"center": v(46, 46) * mm, "radius": 1.5 * mm});
            skCircle(sketch, "E44.14.0.65", {"center": v(-29, 46) * mm, "radius": 1.5 * mm});
            skCircle(sketch, "E44.14.0.66", {"center": v(-109, 46) * mm, "radius": 1.5 * mm});
            skCircle(sketch, "E44.14.0.67", {"center": v(126, 46) * mm, "radius": 1.5 * mm});
            skLineSegment(sketch, "E44.14.0.68", {"start": v(-174, 46) * mm, "end": v(-169, 46) * mm, "construction": true});
            skCircle(sketch, "E44.14.0.69", {"center": v(-174, 46) * mm, "radius": 1.5 * mm});
            skCircle(sketch, "E44.14.0.70", {"center": v(-169, 46) * mm, "radius": 1.5 * mm});
            skCircle(sketch, "E44.15.0.0", {"center": v(166, 41) * mm, "radius": 1.5 * mm});
            skCircle(sketch, "E44.15.0.1", {"center": v(21, 41) * mm, "radius": 1.5 * mm});
            skCircle(sketch, "E44.15.0.2", {"center": v(-99, 41) * mm, "radius": 1.5 * mm});
            skCircle(sketch, "E44.15.0.3", {"center": v(6, 41) * mm, "radius": 1.5 * mm});
            skCircle(sketch, "E44.15.0.4", {"center": v(-54, 41) * mm, "radius": 1.5 * mm});
            skCircle(sketch, "E44.15.0.5", {"center": v(171, 41) * mm, "radius": 1.5 * mm});
            skCircle(sketch, "E44.15.0.6", {"center": v(-104, 41) * mm, "radius": 1.5 * mm});
            skCircle(sketch, "E44.15.0.7", {"center": v(11, 41) * mm, "radius": 1.5 * mm});
            skCircle(sketch, "E44.15.0.8", {"center": v(56, 41) * mm, "radius": 1.5 * mm});
            skCircle(sketch, "E44.15.0.9", {"center": v(-134, 41) * mm, "radius": 1.5 * mm});
            skCircle(sketch, "E44.15.0.10", {"center": v(51, 41) * mm, "radius": 1.5 * mm});
            skCircle(sketch, "E44.15.0.11", {"center": v(131, 41) * mm, "radius": 1.5 * mm});
            skCircle(sketch, "E44.15.0.12", {"center": v(151, 41) * mm, "radius": 1.5 * mm});
            skCircle(sketch, "E44.15.0.13", {"center": v(-24, 41) * mm, "radius": 1.5 * mm});
            skCircle(sketch, "E44.15.0.14", {"center": v(-64, 41) * mm, "radius": 1.5 * mm});
            skCircle(sketch, "E44.15.0.15", {"center": v(-9, 41) * mm, "radius": 1.5 * mm});
            skCircle(sketch, "E44.15.0.16", {"center": v(136, 41) * mm, "radius": 1.5 * mm});
            skCircle(sketch, "E44.15.0.17", {"center": v(91, 41) * mm, "radius": 1.5 * mm});
            skCircle(sketch, "E44.15.0.18", {"center": v(101, 41) * mm, "radius": 1.5 * mm});
            skCircle(sketch, "E44.15.0.19", {"center": v(-144, 41) * mm, "radius": 1.5 * mm});
            skCircle(sketch, "E44.15.0.20", {"center": v(71, 41) * mm, "radius": 1.5 * mm});
            skCircle(sketch, "E44.15.0.21", {"center": v(-69, 41) * mm, "radius": 1.5 * mm});
            skCircle(sketch, "E44.15.0.22", {"center": v(-84, 41) * mm, "radius": 1.5 * mm});
            skCircle(sketch, "E44.15.0.23", {"center": v(116, 41) * mm, "radius": 1.5 * mm});
            skCircle(sketch, "E44.15.0.24", {"center": v(-164, 41) * mm, "radius": 1.5 * mm});
            skCircle(sketch, "E44.15.0.25", {"center": v(86, 41) * mm, "radius": 1.5 * mm});
            skCircle(sketch, "E44.15.0.26", {"center": v(-149, 41) * mm, "radius": 1.5 * mm});
            skCircle(sketch, "E44.15.0.27", {"center": v(106, 41) * mm, "radius": 1.5 * mm});
            skCircle(sketch, "E44.15.0.28", {"center": v(-94, 41) * mm, "radius": 1.5 * mm});
            skCircle(sketch, "E44.15.0.29", {"center": v(-129, 41) * mm, "radius": 1.5 * mm});
            skCircle(sketch, "E44.15.0.30", {"center": v(-19, 41) * mm, "radius": 1.5 * mm});
            skCircle(sketch, "E44.15.0.31", {"center": v(-49, 41) * mm, "radius": 1.5 * mm});
            skCircle(sketch, "E44.15.0.32", {"center": v(26, 41) * mm, "radius": 1.5 * mm});
            skCircle(sketch, "E44.15.0.33", {"center": v(61, 41) * mm, "radius": 1.5 * mm});
            skCircle(sketch, "E44.15.0.34", {"center": v(16, 41) * mm, "radius": 1.5 * mm});
            skCircle(sketch, "E44.15.0.35", {"center": v(96, 41) * mm, "radius": 1.5 * mm});
            skCircle(sketch, "E44.15.0.36", {"center": v(-139, 41) * mm, "radius": 1.5 * mm});
            skCircle(sketch, "E44.15.0.37", {"center": v(-59, 41) * mm, "radius": 1.5 * mm});
            skCircle(sketch, "E44.15.0.38", {"center": v(111, 41) * mm, "radius": 1.5 * mm});
            skCircle(sketch, "E44.15.0.39", {"center": v(146, 41) * mm, "radius": 1.5 * mm});
            skCircle(sketch, "E44.15.0.40", {"center": v(-89, 41) * mm, "radius": 1.5 * mm});
            skCircle(sketch, "E44.15.0.41", {"center": v(-44, 41) * mm, "radius": 1.5 * mm});
            skCircle(sketch, "E44.15.0.42", {"center": v(-124, 41) * mm, "radius": 1.5 * mm});
            skCircle(sketch, "E44.15.0.43", {"center": v(-14, 41) * mm, "radius": 1.5 * mm});
            skCircle(sketch, "E44.15.0.44", {"center": v(31, 41) * mm, "radius": 1.5 * mm});
            skCircle(sketch, "E44.15.0.45", {"center": v(66, 41) * mm, "radius": 1.5 * mm});
            skCircle(sketch, "E44.15.0.46", {"center": v(141, 41) * mm, "radius": 1.5 * mm});
            skCircle(sketch, "E44.15.0.47", {"center": v(36, 41) * mm, "radius": 1.5 * mm});
            skCircle(sketch, "E44.15.0.48", {"center": v(-39, 41) * mm, "radius": 1.5 * mm});
            skCircle(sketch, "E44.15.0.49", {"center": v(-119, 41) * mm, "radius": 1.5 * mm});
            skCircle(sketch, "E44.15.0.50", {"center": v(-79, 41) * mm, "radius": 1.5 * mm});
            skCircle(sketch, "E44.15.0.51", {"center": v(-159, 41) * mm, "radius": 1.5 * mm});
            skCircle(sketch, "E44.15.0.52", {"center": v(156, 41) * mm, "radius": 1.5 * mm});
            skCircle(sketch, "E44.15.0.53", {"center": v(76, 41) * mm, "radius": 1.5 * mm});
            skCircle(sketch, "E44.15.0.54", {"center": v(-4, 41) * mm, "radius": 1.5 * mm});
            skCircle(sketch, "E44.15.0.55", {"center": v(41, 41) * mm, "radius": 1.5 * mm});
            skCircle(sketch, "E44.15.0.56", {"center": v(-34, 41) * mm, "radius": 1.5 * mm});
            skCircle(sketch, "E44.15.0.57", {"center": v(-114, 41) * mm, "radius": 1.5 * mm});
            skCircle(sketch, "E44.15.0.58", {"center": v(121, 41) * mm, "radius": 1.5 * mm});
            skCircle(sketch, "E44.15.0.59", {"center": v(-74, 41) * mm, "radius": 1.5 * mm});
            skCircle(sketch, "E44.15.0.60", {"center": v(-154, 41) * mm, "radius": 1.5 * mm});
            skCircle(sketch, "E44.15.0.61", {"center": v(161, 41) * mm, "radius": 1.5 * mm});
            skCircle(sketch, "E44.15.0.62", {"center": v(81, 41) * mm, "radius": 1.5 * mm});
            skCircle(sketch, "E44.15.0.63", {"center": v(1, 41) * mm, "radius": 1.5 * mm});
            skCircle(sketch, "E44.15.0.64", {"center": v(46, 41) * mm, "radius": 1.5 * mm});
            skCircle(sketch, "E44.15.0.65", {"center": v(-29, 41) * mm, "radius": 1.5 * mm});
            skCircle(sketch, "E44.15.0.66", {"center": v(-109, 41) * mm, "radius": 1.5 * mm});
            skCircle(sketch, "E44.15.0.67", {"center": v(126, 41) * mm, "radius": 1.5 * mm});
            skLineSegment(sketch, "E44.15.0.68", {"start": v(-174, 41) * mm, "end": v(-169, 41) * mm, "construction": true});
            skCircle(sketch, "E44.15.0.69", {"center": v(-174, 41) * mm, "radius": 1.5 * mm});
            skCircle(sketch, "E44.15.0.70", {"center": v(-169, 41) * mm, "radius": 1.5 * mm});
            skCircle(sketch, "E44.16.0.0", {"center": v(166, 36) * mm, "radius": 1.5 * mm});
            skCircle(sketch, "E44.16.0.1", {"center": v(21, 36) * mm, "radius": 1.5 * mm});
            skCircle(sketch, "E44.16.0.2", {"center": v(-99, 36) * mm, "radius": 1.5 * mm});
            skCircle(sketch, "E44.16.0.3", {"center": v(6, 36) * mm, "radius": 1.5 * mm});
            skCircle(sketch, "E44.16.0.4", {"center": v(-54, 36) * mm, "radius": 1.5 * mm});
            skCircle(sketch, "E44.16.0.5", {"center": v(171, 36) * mm, "radius": 1.5 * mm});
            skCircle(sketch, "E44.16.0.6", {"center": v(-104, 36) * mm, "radius": 1.5 * mm});
            skCircle(sketch, "E44.16.0.7", {"center": v(11, 36) * mm, "radius": 1.5 * mm});
            skCircle(sketch, "E44.16.0.8", {"center": v(56, 36) * mm, "radius": 1.5 * mm});
            skCircle(sketch, "E44.16.0.9", {"center": v(-134, 36) * mm, "radius": 1.5 * mm});
            skCircle(sketch, "E44.16.0.10", {"center": v(51, 36) * mm, "radius": 1.5 * mm});
            skCircle(sketch, "E44.16.0.11", {"center": v(131, 36) * mm, "radius": 1.5 * mm});
            skCircle(sketch, "E44.16.0.12", {"center": v(151, 36) * mm, "radius": 1.5 * mm});
            skCircle(sketch, "E44.16.0.13", {"center": v(-24, 36) * mm, "radius": 1.5 * mm});
            skCircle(sketch, "E44.16.0.14", {"center": v(-64, 36) * mm, "radius": 1.5 * mm});
            skCircle(sketch, "E44.16.0.15", {"center": v(-9, 36) * mm, "radius": 1.5 * mm});
            skCircle(sketch, "E44.16.0.16", {"center": v(136, 36) * mm, "radius": 1.5 * mm});
            skCircle(sketch, "E44.16.0.17", {"center": v(91, 36) * mm, "radius": 1.5 * mm});
            skCircle(sketch, "E44.16.0.18", {"center": v(101, 36) * mm, "radius": 1.5 * mm});
            skCircle(sketch, "E44.16.0.19", {"center": v(-144, 36) * mm, "radius": 1.5 * mm});
            skCircle(sketch, "E44.16.0.20", {"center": v(71, 36) * mm, "radius": 1.5 * mm});
            skCircle(sketch, "E44.16.0.21", {"center": v(-69, 36) * mm, "radius": 1.5 * mm});
            skCircle(sketch, "E44.16.0.22", {"center": v(-84, 36) * mm, "radius": 1.5 * mm});
            skCircle(sketch, "E44.16.0.23", {"center": v(116, 36) * mm, "radius": 1.5 * mm});
            skCircle(sketch, "E44.16.0.24", {"center": v(-164, 36) * mm, "radius": 1.5 * mm});
            skCircle(sketch, "E44.16.0.25", {"center": v(86, 36) * mm, "radius": 1.5 * mm});
            skCircle(sketch, "E44.16.0.26", {"center": v(-149, 36) * mm, "radius": 1.5 * mm});
            skCircle(sketch, "E44.16.0.27", {"center": v(106, 36) * mm, "radius": 1.5 * mm});
            skCircle(sketch, "E44.16.0.28", {"center": v(-94, 36) * mm, "radius": 1.5 * mm});
            skCircle(sketch, "E44.16.0.29", {"center": v(-129, 36) * mm, "radius": 1.5 * mm});
            skCircle(sketch, "E44.16.0.30", {"center": v(-19, 36) * mm, "radius": 1.5 * mm});
            skCircle(sketch, "E44.16.0.31", {"center": v(-49, 36) * mm, "radius": 1.5 * mm});
            skCircle(sketch, "E44.16.0.32", {"center": v(26, 36) * mm, "radius": 1.5 * mm});
            skCircle(sketch, "E44.16.0.33", {"center": v(61, 36) * mm, "radius": 1.5 * mm});
            skCircle(sketch, "E44.16.0.34", {"center": v(16, 36) * mm, "radius": 1.5 * mm});
            skCircle(sketch, "E44.16.0.35", {"center": v(96, 36) * mm, "radius": 1.5 * mm});
            skCircle(sketch, "E44.16.0.36", {"center": v(-139, 36) * mm, "radius": 1.5 * mm});
            skCircle(sketch, "E44.16.0.37", {"center": v(-59, 36) * mm, "radius": 1.5 * mm});
            skCircle(sketch, "E44.16.0.38", {"center": v(111, 36) * mm, "radius": 1.5 * mm});
            skCircle(sketch, "E44.16.0.39", {"center": v(146, 36) * mm, "radius": 1.5 * mm});
            skCircle(sketch, "E44.16.0.40", {"center": v(-89, 36) * mm, "radius": 1.5 * mm});
            skCircle(sketch, "E44.16.0.41", {"center": v(-44, 36) * mm, "radius": 1.5 * mm});
            skCircle(sketch, "E44.16.0.42", {"center": v(-124, 36) * mm, "radius": 1.5 * mm});
            skCircle(sketch, "E44.16.0.43", {"center": v(-14, 36) * mm, "radius": 1.5 * mm});
            skCircle(sketch, "E44.16.0.44", {"center": v(31, 36) * mm, "radius": 1.5 * mm});
            skCircle(sketch, "E44.16.0.45", {"center": v(66, 36) * mm, "radius": 1.5 * mm});
            skCircle(sketch, "E44.16.0.46", {"center": v(141, 36) * mm, "radius": 1.5 * mm});
            skCircle(sketch, "E44.16.0.47", {"center": v(36, 36) * mm, "radius": 1.5 * mm});
            skCircle(sketch, "E44.16.0.48", {"center": v(-39, 36) * mm, "radius": 1.5 * mm});
            skCircle(sketch, "E44.16.0.49", {"center": v(-119, 36) * mm, "radius": 1.5 * mm});
            skCircle(sketch, "E44.16.0.50", {"center": v(-79, 36) * mm, "radius": 1.5 * mm});
            skCircle(sketch, "E44.16.0.51", {"center": v(-159, 36) * mm, "radius": 1.5 * mm});
            skCircle(sketch, "E44.16.0.52", {"center": v(156, 36) * mm, "radius": 1.5 * mm});
            skCircle(sketch, "E44.16.0.53", {"center": v(76, 36) * mm, "radius": 1.5 * mm});
            skCircle(sketch, "E44.16.0.54", {"center": v(-4, 36) * mm, "radius": 1.5 * mm});
            skCircle(sketch, "E44.16.0.55", {"center": v(41, 36) * mm, "radius": 1.5 * mm});
            skCircle(sketch, "E44.16.0.56", {"center": v(-34, 36) * mm, "radius": 1.5 * mm});
            skCircle(sketch, "E44.16.0.57", {"center": v(-114, 36) * mm, "radius": 1.5 * mm});
            skCircle(sketch, "E44.16.0.58", {"center": v(121, 36) * mm, "radius": 1.5 * mm});
            skCircle(sketch, "E44.16.0.59", {"center": v(-74, 36) * mm, "radius": 1.5 * mm});
            skCircle(sketch, "E44.16.0.60", {"center": v(-154, 36) * mm, "radius": 1.5 * mm});
            skCircle(sketch, "E44.16.0.61", {"center": v(161, 36) * mm, "radius": 1.5 * mm});
            skCircle(sketch, "E44.16.0.62", {"center": v(81, 36) * mm, "radius": 1.5 * mm});
            skCircle(sketch, "E44.16.0.63", {"center": v(1, 36) * mm, "radius": 1.5 * mm});
            skCircle(sketch, "E44.16.0.64", {"center": v(46, 36) * mm, "radius": 1.5 * mm});
            skCircle(sketch, "E44.16.0.65", {"center": v(-29, 36) * mm, "radius": 1.5 * mm});
            skCircle(sketch, "E44.16.0.66", {"center": v(-109, 36) * mm, "radius": 1.5 * mm});
            skCircle(sketch, "E44.16.0.67", {"center": v(126, 36) * mm, "radius": 1.5 * mm});
            skLineSegment(sketch, "E44.16.0.68", {"start": v(-174, 36) * mm, "end": v(-169, 36) * mm, "construction": true});
            skCircle(sketch, "E44.16.0.69", {"center": v(-174, 36) * mm, "radius": 1.5 * mm});
            skCircle(sketch, "E44.16.0.70", {"center": v(-169, 36) * mm, "radius": 1.5 * mm});
            skCircle(sketch, "E44.17.0.0", {"center": v(166, 31) * mm, "radius": 1.5 * mm});
            skCircle(sketch, "E44.17.0.1", {"center": v(21, 31) * mm, "radius": 1.5 * mm});
            skCircle(sketch, "E44.17.0.2", {"center": v(-99, 31) * mm, "radius": 1.5 * mm});
            skCircle(sketch, "E44.17.0.3", {"center": v(6, 31) * mm, "radius": 1.5 * mm});
            skCircle(sketch, "E44.17.0.4", {"center": v(-54, 31) * mm, "radius": 1.5 * mm});
            skCircle(sketch, "E44.17.0.5", {"center": v(171, 31) * mm, "radius": 1.5 * mm});
            skCircle(sketch, "E44.17.0.6", {"center": v(-104, 31) * mm, "radius": 1.5 * mm});
            skCircle(sketch, "E44.17.0.7", {"center": v(11, 31) * mm, "radius": 1.5 * mm});
            skCircle(sketch, "E44.17.0.8", {"center": v(56, 31) * mm, "radius": 1.5 * mm});
            skCircle(sketch, "E44.17.0.9", {"center": v(-134, 31) * mm, "radius": 1.5 * mm});
            skCircle(sketch, "E44.17.0.10", {"center": v(51, 31) * mm, "radius": 1.5 * mm});
            skCircle(sketch, "E44.17.0.11", {"center": v(131, 31) * mm, "radius": 1.5 * mm});
            skCircle(sketch, "E44.17.0.12", {"center": v(151, 31) * mm, "radius": 1.5 * mm});
            skCircle(sketch, "E44.17.0.13", {"center": v(-24, 31) * mm, "radius": 1.5 * mm});
            skCircle(sketch, "E44.17.0.14", {"center": v(-64, 31) * mm, "radius": 1.5 * mm});
            skCircle(sketch, "E44.17.0.15", {"center": v(-9, 31) * mm, "radius": 1.5 * mm});
            skCircle(sketch, "E44.17.0.16", {"center": v(136, 31) * mm, "radius": 1.5 * mm});
            skCircle(sketch, "E44.17.0.17", {"center": v(91, 31) * mm, "radius": 1.5 * mm});
            skCircle(sketch, "E44.17.0.18", {"center": v(101, 31) * mm, "radius": 1.5 * mm});
            skCircle(sketch, "E44.17.0.19", {"center": v(-144, 31) * mm, "radius": 1.5 * mm});
            skCircle(sketch, "E44.17.0.20", {"center": v(71, 31) * mm, "radius": 1.5 * mm});
            skCircle(sketch, "E44.17.0.21", {"center": v(-69, 31) * mm, "radius": 1.5 * mm});
            skCircle(sketch, "E44.17.0.22", {"center": v(-84, 31) * mm, "radius": 1.5 * mm});
            skCircle(sketch, "E44.17.0.23", {"center": v(116, 31) * mm, "radius": 1.5 * mm});
            skCircle(sketch, "E44.17.0.24", {"center": v(-164, 31) * mm, "radius": 1.5 * mm});
            skCircle(sketch, "E44.17.0.25", {"center": v(86, 31) * mm, "radius": 1.5 * mm});
            skCircle(sketch, "E44.17.0.26", {"center": v(-149, 31) * mm, "radius": 1.5 * mm});
            skCircle(sketch, "E44.17.0.27", {"center": v(106, 31) * mm, "radius": 1.5 * mm});
            skCircle(sketch, "E44.17.0.28", {"center": v(-94, 31) * mm, "radius": 1.5 * mm});
            skCircle(sketch, "E44.17.0.29", {"center": v(-129, 31) * mm, "radius": 1.5 * mm});
            skCircle(sketch, "E44.17.0.30", {"center": v(-19, 31) * mm, "radius": 1.5 * mm});
            skCircle(sketch, "E44.17.0.31", {"center": v(-49, 31) * mm, "radius": 1.5 * mm});
            skCircle(sketch, "E44.17.0.32", {"center": v(26, 31) * mm, "radius": 1.5 * mm});
            skCircle(sketch, "E44.17.0.33", {"center": v(61, 31) * mm, "radius": 1.5 * mm});
            skCircle(sketch, "E44.17.0.34", {"center": v(16, 31) * mm, "radius": 1.5 * mm});
            skCircle(sketch, "E44.17.0.35", {"center": v(96, 31) * mm, "radius": 1.5 * mm});
            skCircle(sketch, "E44.17.0.36", {"center": v(-139, 31) * mm, "radius": 1.5 * mm});
            skCircle(sketch, "E44.17.0.37", {"center": v(-59, 31) * mm, "radius": 1.5 * mm});
            skCircle(sketch, "E44.17.0.38", {"center": v(111, 31) * mm, "radius": 1.5 * mm});
            skCircle(sketch, "E44.17.0.39", {"center": v(146, 31) * mm, "radius": 1.5 * mm});
            skCircle(sketch, "E44.17.0.40", {"center": v(-89, 31) * mm, "radius": 1.5 * mm});
            skCircle(sketch, "E44.17.0.41", {"center": v(-44, 31) * mm, "radius": 1.5 * mm});
            skCircle(sketch, "E44.17.0.42", {"center": v(-124, 31) * mm, "radius": 1.5 * mm});
            skCircle(sketch, "E44.17.0.43", {"center": v(-14, 31) * mm, "radius": 1.5 * mm});
            skCircle(sketch, "E44.17.0.44", {"center": v(31, 31) * mm, "radius": 1.5 * mm});
            skCircle(sketch, "E44.17.0.45", {"center": v(66, 31) * mm, "radius": 1.5 * mm});
            skCircle(sketch, "E44.17.0.46", {"center": v(141, 31) * mm, "radius": 1.5 * mm});
            skCircle(sketch, "E44.17.0.47", {"center": v(36, 31) * mm, "radius": 1.5 * mm});
            skCircle(sketch, "E44.17.0.48", {"center": v(-39, 31) * mm, "radius": 1.5 * mm});
            skCircle(sketch, "E44.17.0.49", {"center": v(-119, 31) * mm, "radius": 1.5 * mm});
            skCircle(sketch, "E44.17.0.50", {"center": v(-79, 31) * mm, "radius": 1.5 * mm});
            skCircle(sketch, "E44.17.0.51", {"center": v(-159, 31) * mm, "radius": 1.5 * mm});
            skCircle(sketch, "E44.17.0.52", {"center": v(156, 31) * mm, "radius": 1.5 * mm});
            skCircle(sketch, "E44.17.0.53", {"center": v(76, 31) * mm, "radius": 1.5 * mm});
            skCircle(sketch, "E44.17.0.54", {"center": v(-4, 31) * mm, "radius": 1.5 * mm});
            skCircle(sketch, "E44.17.0.55", {"center": v(41, 31) * mm, "radius": 1.5 * mm});
            skCircle(sketch, "E44.17.0.56", {"center": v(-34, 31) * mm, "radius": 1.5 * mm});
            skCircle(sketch, "E44.17.0.57", {"center": v(-114, 31) * mm, "radius": 1.5 * mm});
            skCircle(sketch, "E44.17.0.58", {"center": v(121, 31) * mm, "radius": 1.5 * mm});
            skCircle(sketch, "E44.17.0.59", {"center": v(-74, 31) * mm, "radius": 1.5 * mm});
            skCircle(sketch, "E44.17.0.60", {"center": v(-154, 31) * mm, "radius": 1.5 * mm});
            skCircle(sketch, "E44.17.0.61", {"center": v(161, 31) * mm, "radius": 1.5 * mm});
            skCircle(sketch, "E44.17.0.62", {"center": v(81, 31) * mm, "radius": 1.5 * mm});
            skCircle(sketch, "E44.17.0.63", {"center": v(1, 31) * mm, "radius": 1.5 * mm});
            skCircle(sketch, "E44.17.0.64", {"center": v(46, 31) * mm, "radius": 1.5 * mm});
            skCircle(sketch, "E44.17.0.65", {"center": v(-29, 31) * mm, "radius": 1.5 * mm});
            skCircle(sketch, "E44.17.0.66", {"center": v(-109, 31) * mm, "radius": 1.5 * mm});
            skCircle(sketch, "E44.17.0.67", {"center": v(126, 31) * mm, "radius": 1.5 * mm});
            skLineSegment(sketch, "E44.17.0.68", {"start": v(-174, 31) * mm, "end": v(-169, 31) * mm, "construction": true});
            skCircle(sketch, "E44.17.0.69", {"center": v(-174, 31) * mm, "radius": 1.5 * mm});
            skCircle(sketch, "E44.17.0.70", {"center": v(-169, 31) * mm, "radius": 1.5 * mm});
            skCircle(sketch, "E44.18.0.0", {"center": v(166, 26) * mm, "radius": 1.5 * mm});
            skCircle(sketch, "E44.18.0.1", {"center": v(21, 26) * mm, "radius": 1.5 * mm});
            skCircle(sketch, "E44.18.0.2", {"center": v(-99, 26) * mm, "radius": 1.5 * mm});
            skCircle(sketch, "E44.18.0.3", {"center": v(6, 26) * mm, "radius": 1.5 * mm});
            skCircle(sketch, "E44.18.0.4", {"center": v(-54, 26) * mm, "radius": 1.5 * mm});
            skCircle(sketch, "E44.18.0.5", {"center": v(171, 26) * mm, "radius": 1.5 * mm});
            skCircle(sketch, "E44.18.0.6", {"center": v(-104, 26) * mm, "radius": 1.5 * mm});
            skCircle(sketch, "E44.18.0.7", {"center": v(11, 26) * mm, "radius": 1.5 * mm});
            skCircle(sketch, "E44.18.0.8", {"center": v(56, 26) * mm, "radius": 1.5 * mm});
            skCircle(sketch, "E44.18.0.9", {"center": v(-134, 26) * mm, "radius": 1.5 * mm});
            skCircle(sketch, "E44.18.0.10", {"center": v(51, 26) * mm, "radius": 1.5 * mm});
            skCircle(sketch, "E44.18.0.11", {"center": v(131, 26) * mm, "radius": 1.5 * mm});
            skCircle(sketch, "E44.18.0.12", {"center": v(151, 26) * mm, "radius": 1.5 * mm});
            skCircle(sketch, "E44.18.0.13", {"center": v(-24, 26) * mm, "radius": 1.5 * mm});
            skCircle(sketch, "E44.18.0.14", {"center": v(-64, 26) * mm, "radius": 1.5 * mm});
            skCircle(sketch, "E44.18.0.15", {"center": v(-9, 26) * mm, "radius": 1.5 * mm});
            skCircle(sketch, "E44.18.0.16", {"center": v(136, 26) * mm, "radius": 1.5 * mm});
            skCircle(sketch, "E44.18.0.17", {"center": v(91, 26) * mm, "radius": 1.5 * mm});
            skCircle(sketch, "E44.18.0.18", {"center": v(101, 26) * mm, "radius": 1.5 * mm});
            skCircle(sketch, "E44.18.0.19", {"center": v(-144, 26) * mm, "radius": 1.5 * mm});
            skCircle(sketch, "E44.18.0.20", {"center": v(71, 26) * mm, "radius": 1.5 * mm});
            skCircle(sketch, "E44.18.0.21", {"center": v(-69, 26) * mm, "radius": 1.5 * mm});
            skCircle(sketch, "E44.18.0.22", {"center": v(-84, 26) * mm, "radius": 1.5 * mm});
            skCircle(sketch, "E44.18.0.23", {"center": v(116, 26) * mm, "radius": 1.5 * mm});
            skCircle(sketch, "E44.18.0.24", {"center": v(-164, 26) * mm, "radius": 1.5 * mm});
            skCircle(sketch, "E44.18.0.25", {"center": v(86, 26) * mm, "radius": 1.5 * mm});
            skCircle(sketch, "E44.18.0.26", {"center": v(-149, 26) * mm, "radius": 1.5 * mm});
            skCircle(sketch, "E44.18.0.27", {"center": v(106, 26) * mm, "radius": 1.5 * mm});
            skCircle(sketch, "E44.18.0.28", {"center": v(-94, 26) * mm, "radius": 1.5 * mm});
            skCircle(sketch, "E44.18.0.29", {"center": v(-129, 26) * mm, "radius": 1.5 * mm});
            skCircle(sketch, "E44.18.0.30", {"center": v(-19, 26) * mm, "radius": 1.5 * mm});
            skCircle(sketch, "E44.18.0.31", {"center": v(-49, 26) * mm, "radius": 1.5 * mm});
            skCircle(sketch, "E44.18.0.32", {"center": v(26, 26) * mm, "radius": 1.5 * mm});
            skCircle(sketch, "E44.18.0.33", {"center": v(61, 26) * mm, "radius": 1.5 * mm});
            skCircle(sketch, "E44.18.0.34", {"center": v(16, 26) * mm, "radius": 1.5 * mm});
            skCircle(sketch, "E44.18.0.35", {"center": v(96, 26) * mm, "radius": 1.5 * mm});
            skCircle(sketch, "E44.18.0.36", {"center": v(-139, 26) * mm, "radius": 1.5 * mm});
            skCircle(sketch, "E44.18.0.37", {"center": v(-59, 26) * mm, "radius": 1.5 * mm});
            skCircle(sketch, "E44.18.0.38", {"center": v(111, 26) * mm, "radius": 1.5 * mm});
            skCircle(sketch, "E44.18.0.39", {"center": v(146, 26) * mm, "radius": 1.5 * mm});
            skCircle(sketch, "E44.18.0.40", {"center": v(-89, 26) * mm, "radius": 1.5 * mm});
            skCircle(sketch, "E44.18.0.41", {"center": v(-44, 26) * mm, "radius": 1.5 * mm});
            skCircle(sketch, "E44.18.0.42", {"center": v(-124, 26) * mm, "radius": 1.5 * mm});
            skCircle(sketch, "E44.18.0.43", {"center": v(-14, 26) * mm, "radius": 1.5 * mm});
            skCircle(sketch, "E44.18.0.44", {"center": v(31, 26) * mm, "radius": 1.5 * mm});
            skCircle(sketch, "E44.18.0.45", {"center": v(66, 26) * mm, "radius": 1.5 * mm});
            skCircle(sketch, "E44.18.0.46", {"center": v(141, 26) * mm, "radius": 1.5 * mm});
            skCircle(sketch, "E44.18.0.47", {"center": v(36, 26) * mm, "radius": 1.5 * mm});
            skCircle(sketch, "E44.18.0.48", {"center": v(-39, 26) * mm, "radius": 1.5 * mm});
            skCircle(sketch, "E44.18.0.49", {"center": v(-119, 26) * mm, "radius": 1.5 * mm});
            skCircle(sketch, "E44.18.0.50", {"center": v(-79, 26) * mm, "radius": 1.5 * mm});
            skCircle(sketch, "E44.18.0.51", {"center": v(-159, 26) * mm, "radius": 1.5 * mm});
            skCircle(sketch, "E44.18.0.52", {"center": v(156, 26) * mm, "radius": 1.5 * mm});
            skCircle(sketch, "E44.18.0.53", {"center": v(76, 26) * mm, "radius": 1.5 * mm});
            skCircle(sketch, "E44.18.0.54", {"center": v(-4, 26) * mm, "radius": 1.5 * mm});
            skCircle(sketch, "E44.18.0.55", {"center": v(41, 26) * mm, "radius": 1.5 * mm});
            skCircle(sketch, "E44.18.0.56", {"center": v(-34, 26) * mm, "radius": 1.5 * mm});
            skCircle(sketch, "E44.18.0.57", {"center": v(-114, 26) * mm, "radius": 1.5 * mm});
            skCircle(sketch, "E44.18.0.58", {"center": v(121, 26) * mm, "radius": 1.5 * mm});
            skCircle(sketch, "E44.18.0.59", {"center": v(-74, 26) * mm, "radius": 1.5 * mm});
            skCircle(sketch, "E44.18.0.60", {"center": v(-154, 26) * mm, "radius": 1.5 * mm});
            skCircle(sketch, "E44.18.0.61", {"center": v(161, 26) * mm, "radius": 1.5 * mm});
            skCircle(sketch, "E44.18.0.62", {"center": v(81, 26) * mm, "radius": 1.5 * mm});
            skCircle(sketch, "E44.18.0.63", {"center": v(1, 26) * mm, "radius": 1.5 * mm});
            skCircle(sketch, "E44.18.0.64", {"center": v(46, 26) * mm, "radius": 1.5 * mm});
            skCircle(sketch, "E44.18.0.65", {"center": v(-29, 26) * mm, "radius": 1.5 * mm});
            skCircle(sketch, "E44.18.0.66", {"center": v(-109, 26) * mm, "radius": 1.5 * mm});
            skCircle(sketch, "E44.18.0.67", {"center": v(126, 26) * mm, "radius": 1.5 * mm});
            skLineSegment(sketch, "E44.18.0.68", {"start": v(-174, 26) * mm, "end": v(-169, 26) * mm, "construction": true});
            skCircle(sketch, "E44.18.0.69", {"center": v(-174, 26) * mm, "radius": 1.5 * mm});
            skCircle(sketch, "E44.18.0.70", {"center": v(-169, 26) * mm, "radius": 1.5 * mm});
            skCircle(sketch, "E44.19.0.0", {"center": v(166, 21) * mm, "radius": 1.5 * mm});
            skCircle(sketch, "E44.19.0.1", {"center": v(21, 21) * mm, "radius": 1.5 * mm});
            skCircle(sketch, "E44.19.0.2", {"center": v(-99, 21) * mm, "radius": 1.5 * mm});
            skCircle(sketch, "E44.19.0.3", {"center": v(6, 21) * mm, "radius": 1.5 * mm});
            skCircle(sketch, "E44.19.0.4", {"center": v(-54, 21) * mm, "radius": 1.5 * mm});
            skCircle(sketch, "E44.19.0.5", {"center": v(171, 21) * mm, "radius": 1.5 * mm});
            skCircle(sketch, "E44.19.0.6", {"center": v(-104, 21) * mm, "radius": 1.5 * mm});
            skCircle(sketch, "E44.19.0.7", {"center": v(11, 21) * mm, "radius": 1.5 * mm});
            skCircle(sketch, "E44.19.0.8", {"center": v(56, 21) * mm, "radius": 1.5 * mm});
            skCircle(sketch, "E44.19.0.9", {"center": v(-134, 21) * mm, "radius": 1.5 * mm});
            skCircle(sketch, "E44.19.0.10", {"center": v(51, 21) * mm, "radius": 1.5 * mm});
            skCircle(sketch, "E44.19.0.11", {"center": v(131, 21) * mm, "radius": 1.5 * mm});
            skCircle(sketch, "E44.19.0.12", {"center": v(151, 21) * mm, "radius": 1.5 * mm});
            skCircle(sketch, "E44.19.0.13", {"center": v(-24, 21) * mm, "radius": 1.5 * mm});
            skCircle(sketch, "E44.19.0.14", {"center": v(-64, 21) * mm, "radius": 1.5 * mm});
            skCircle(sketch, "E44.19.0.15", {"center": v(-9, 21) * mm, "radius": 1.5 * mm});
            skCircle(sketch, "E44.19.0.16", {"center": v(136, 21) * mm, "radius": 1.5 * mm});
            skCircle(sketch, "E44.19.0.17", {"center": v(91, 21) * mm, "radius": 1.5 * mm});
            skCircle(sketch, "E44.19.0.18", {"center": v(101, 21) * mm, "radius": 1.5 * mm});
            skCircle(sketch, "E44.19.0.19", {"center": v(-144, 21) * mm, "radius": 1.5 * mm});
            skCircle(sketch, "E44.19.0.20", {"center": v(71, 21) * mm, "radius": 1.5 * mm});
            skCircle(sketch, "E44.19.0.21", {"center": v(-69, 21) * mm, "radius": 1.5 * mm});
            skCircle(sketch, "E44.19.0.22", {"center": v(-84, 21) * mm, "radius": 1.5 * mm});
            skCircle(sketch, "E44.19.0.23", {"center": v(116, 21) * mm, "radius": 1.5 * mm});
            skCircle(sketch, "E44.19.0.24", {"center": v(-164, 21) * mm, "radius": 1.5 * mm});
            skCircle(sketch, "E44.19.0.25", {"center": v(86, 21) * mm, "radius": 1.5 * mm});
            skCircle(sketch, "E44.19.0.26", {"center": v(-149, 21) * mm, "radius": 1.5 * mm});
            skCircle(sketch, "E44.19.0.27", {"center": v(106, 21) * mm, "radius": 1.5 * mm});
            skCircle(sketch, "E44.19.0.28", {"center": v(-94, 21) * mm, "radius": 1.5 * mm});
            skCircle(sketch, "E44.19.0.29", {"center": v(-129, 21) * mm, "radius": 1.5 * mm});
            skCircle(sketch, "E44.19.0.30", {"center": v(-19, 21) * mm, "radius": 1.5 * mm});
            skCircle(sketch, "E44.19.0.31", {"center": v(-49, 21) * mm, "radius": 1.5 * mm});
            skCircle(sketch, "E44.19.0.32", {"center": v(26, 21) * mm, "radius": 1.5 * mm});
            skCircle(sketch, "E44.19.0.33", {"center": v(61, 21) * mm, "radius": 1.5 * mm});
            skCircle(sketch, "E44.19.0.34", {"center": v(16, 21) * mm, "radius": 1.5 * mm});
            skCircle(sketch, "E44.19.0.35", {"center": v(96, 21) * mm, "radius": 1.5 * mm});
            skCircle(sketch, "E44.19.0.36", {"center": v(-139, 21) * mm, "radius": 1.5 * mm});
            skCircle(sketch, "E44.19.0.37", {"center": v(-59, 21) * mm, "radius": 1.5 * mm});
            skCircle(sketch, "E44.19.0.38", {"center": v(111, 21) * mm, "radius": 1.5 * mm});
            skCircle(sketch, "E44.19.0.39", {"center": v(146, 21) * mm, "radius": 1.5 * mm});
            skCircle(sketch, "E44.19.0.40", {"center": v(-89, 21) * mm, "radius": 1.5 * mm});
            skCircle(sketch, "E44.19.0.41", {"center": v(-44, 21) * mm, "radius": 1.5 * mm});
            skCircle(sketch, "E44.19.0.42", {"center": v(-124, 21) * mm, "radius": 1.5 * mm});
            skCircle(sketch, "E44.19.0.43", {"center": v(-14, 21) * mm, "radius": 1.5 * mm});
            skCircle(sketch, "E44.19.0.44", {"center": v(31, 21) * mm, "radius": 1.5 * mm});
            skCircle(sketch, "E44.19.0.45", {"center": v(66, 21) * mm, "radius": 1.5 * mm});
            skCircle(sketch, "E44.19.0.46", {"center": v(141, 21) * mm, "radius": 1.5 * mm});
            skCircle(sketch, "E44.19.0.47", {"center": v(36, 21) * mm, "radius": 1.5 * mm});
            skCircle(sketch, "E44.19.0.48", {"center": v(-39, 21) * mm, "radius": 1.5 * mm});
            skCircle(sketch, "E44.19.0.49", {"center": v(-119, 21) * mm, "radius": 1.5 * mm});
            skCircle(sketch, "E44.19.0.50", {"center": v(-79, 21) * mm, "radius": 1.5 * mm});
            skCircle(sketch, "E44.19.0.51", {"center": v(-159, 21) * mm, "radius": 1.5 * mm});
            skCircle(sketch, "E44.19.0.52", {"center": v(156, 21) * mm, "radius": 1.5 * mm});
            skCircle(sketch, "E44.19.0.53", {"center": v(76, 21) * mm, "radius": 1.5 * mm});
            skCircle(sketch, "E44.19.0.54", {"center": v(-4, 21) * mm, "radius": 1.5 * mm});
            skCircle(sketch, "E44.19.0.55", {"center": v(41, 21) * mm, "radius": 1.5 * mm});
            skCircle(sketch, "E44.19.0.56", {"center": v(-34, 21) * mm, "radius": 1.5 * mm});
            skCircle(sketch, "E44.19.0.57", {"center": v(-114, 21) * mm, "radius": 1.5 * mm});
            skCircle(sketch, "E44.19.0.58", {"center": v(121, 21) * mm, "radius": 1.5 * mm});
            skCircle(sketch, "E44.19.0.59", {"center": v(-74, 21) * mm, "radius": 1.5 * mm});
            skCircle(sketch, "E44.19.0.60", {"center": v(-154, 21) * mm, "radius": 1.5 * mm});
            skCircle(sketch, "E44.19.0.61", {"center": v(161, 21) * mm, "radius": 1.5 * mm});
            skCircle(sketch, "E44.19.0.62", {"center": v(81, 21) * mm, "radius": 1.5 * mm});
            skCircle(sketch, "E44.19.0.63", {"center": v(1, 21) * mm, "radius": 1.5 * mm});
            skCircle(sketch, "E44.19.0.64", {"center": v(46, 21) * mm, "radius": 1.5 * mm});
            skCircle(sketch, "E44.19.0.65", {"center": v(-29, 21) * mm, "radius": 1.5 * mm});
            skCircle(sketch, "E44.19.0.66", {"center": v(-109, 21) * mm, "radius": 1.5 * mm});
            skCircle(sketch, "E44.19.0.67", {"center": v(126, 21) * mm, "radius": 1.5 * mm});
            skLineSegment(sketch, "E44.19.0.68", {"start": v(-174, 21) * mm, "end": v(-169, 21) * mm, "construction": true});
            skCircle(sketch, "E44.19.0.69", {"center": v(-174, 21) * mm, "radius": 1.5 * mm});
            skCircle(sketch, "E44.19.0.70", {"center": v(-169, 21) * mm, "radius": 1.5 * mm});
            skCircle(sketch, "E44.20.0.0", {"center": v(166, 16) * mm, "radius": 1.5 * mm});
            skCircle(sketch, "E44.20.0.1", {"center": v(21, 16) * mm, "radius": 1.5 * mm});
            skCircle(sketch, "E44.20.0.2", {"center": v(-99, 16) * mm, "radius": 1.5 * mm});
            skCircle(sketch, "E44.20.0.3", {"center": v(6, 16) * mm, "radius": 1.5 * mm});
            skCircle(sketch, "E44.20.0.4", {"center": v(-54, 16) * mm, "radius": 1.5 * mm});
            skCircle(sketch, "E44.20.0.5", {"center": v(171, 16) * mm, "radius": 1.5 * mm});
            skCircle(sketch, "E44.20.0.6", {"center": v(-104, 16) * mm, "radius": 1.5 * mm});
            skCircle(sketch, "E44.20.0.7", {"center": v(11, 16) * mm, "radius": 1.5 * mm});
            skCircle(sketch, "E44.20.0.8", {"center": v(56, 16) * mm, "radius": 1.5 * mm});
            skCircle(sketch, "E44.20.0.9", {"center": v(-134, 16) * mm, "radius": 1.5 * mm});
            skCircle(sketch, "E44.20.0.10", {"center": v(51, 16) * mm, "radius": 1.5 * mm});
            skCircle(sketch, "E44.20.0.11", {"center": v(131, 16) * mm, "radius": 1.5 * mm});
            skCircle(sketch, "E44.20.0.12", {"center": v(151, 16) * mm, "radius": 1.5 * mm});
            skCircle(sketch, "E44.20.0.13", {"center": v(-24, 16) * mm, "radius": 1.5 * mm});
            skCircle(sketch, "E44.20.0.14", {"center": v(-64, 16) * mm, "radius": 1.5 * mm});
            skCircle(sketch, "E44.20.0.15", {"center": v(-9, 16) * mm, "radius": 1.5 * mm});
            skCircle(sketch, "E44.20.0.16", {"center": v(136, 16) * mm, "radius": 1.5 * mm});
            skCircle(sketch, "E44.20.0.17", {"center": v(91, 16) * mm, "radius": 1.5 * mm});
            skCircle(sketch, "E44.20.0.18", {"center": v(101, 16) * mm, "radius": 1.5 * mm});
            skCircle(sketch, "E44.20.0.19", {"center": v(-144, 16) * mm, "radius": 1.5 * mm});
            skCircle(sketch, "E44.20.0.20", {"center": v(71, 16) * mm, "radius": 1.5 * mm});
            skCircle(sketch, "E44.20.0.21", {"center": v(-69, 16) * mm, "radius": 1.5 * mm});
            skCircle(sketch, "E44.20.0.22", {"center": v(-84, 16) * mm, "radius": 1.5 * mm});
            skCircle(sketch, "E44.20.0.23", {"center": v(116, 16) * mm, "radius": 1.5 * mm});
            skCircle(sketch, "E44.20.0.24", {"center": v(-164, 16) * mm, "radius": 1.5 * mm});
            skCircle(sketch, "E44.20.0.25", {"center": v(86, 16) * mm, "radius": 1.5 * mm});
            skCircle(sketch, "E44.20.0.26", {"center": v(-149, 16) * mm, "radius": 1.5 * mm});
            skCircle(sketch, "E44.20.0.27", {"center": v(106, 16) * mm, "radius": 1.5 * mm});
            skCircle(sketch, "E44.20.0.28", {"center": v(-94, 16) * mm, "radius": 1.5 * mm});
            skCircle(sketch, "E44.20.0.29", {"center": v(-129, 16) * mm, "radius": 1.5 * mm});
            skCircle(sketch, "E44.20.0.30", {"center": v(-19, 16) * mm, "radius": 1.5 * mm});
            skCircle(sketch, "E44.20.0.31", {"center": v(-49, 16) * mm, "radius": 1.5 * mm});
            skCircle(sketch, "E44.20.0.32", {"center": v(26, 16) * mm, "radius": 1.5 * mm});
            skCircle(sketch, "E44.20.0.33", {"center": v(61, 16) * mm, "radius": 1.5 * mm});
            skCircle(sketch, "E44.20.0.34", {"center": v(16, 16) * mm, "radius": 1.5 * mm});
            skCircle(sketch, "E44.20.0.35", {"center": v(96, 16) * mm, "radius": 1.5 * mm});
            skCircle(sketch, "E44.20.0.36", {"center": v(-139, 16) * mm, "radius": 1.5 * mm});
            skCircle(sketch, "E44.20.0.37", {"center": v(-59, 16) * mm, "radius": 1.5 * mm});
            skCircle(sketch, "E44.20.0.38", {"center": v(111, 16) * mm, "radius": 1.5 * mm});
            skCircle(sketch, "E44.20.0.39", {"center": v(146, 16) * mm, "radius": 1.5 * mm});
            skCircle(sketch, "E44.20.0.40", {"center": v(-89, 16) * mm, "radius": 1.5 * mm});
            skCircle(sketch, "E44.20.0.41", {"center": v(-44, 16) * mm, "radius": 1.5 * mm});
            skCircle(sketch, "E44.20.0.42", {"center": v(-124, 16) * mm, "radius": 1.5 * mm});
            skCircle(sketch, "E44.20.0.43", {"center": v(-14, 16) * mm, "radius": 1.5 * mm});
            skCircle(sketch, "E44.20.0.44", {"center": v(31, 16) * mm, "radius": 1.5 * mm});
            skCircle(sketch, "E44.20.0.45", {"center": v(66, 16) * mm, "radius": 1.5 * mm});
            skCircle(sketch, "E44.20.0.46", {"center": v(141, 16) * mm, "radius": 1.5 * mm});
            skCircle(sketch, "E44.20.0.47", {"center": v(36, 16) * mm, "radius": 1.5 * mm});
            skCircle(sketch, "E44.20.0.48", {"center": v(-39, 16) * mm, "radius": 1.5 * mm});
            skCircle(sketch, "E44.20.0.49", {"center": v(-119, 16) * mm, "radius": 1.5 * mm});
            skCircle(sketch, "E44.20.0.50", {"center": v(-79, 16) * mm, "radius": 1.5 * mm});
            skCircle(sketch, "E44.20.0.51", {"center": v(-159, 16) * mm, "radius": 1.5 * mm});
            skCircle(sketch, "E44.20.0.52", {"center": v(156, 16) * mm, "radius": 1.5 * mm});
            skCircle(sketch, "E44.20.0.53", {"center": v(76, 16) * mm, "radius": 1.5 * mm});
            skCircle(sketch, "E44.20.0.54", {"center": v(-4, 16) * mm, "radius": 1.5 * mm});
            skCircle(sketch, "E44.20.0.55", {"center": v(41, 16) * mm, "radius": 1.5 * mm});
            skCircle(sketch, "E44.20.0.56", {"center": v(-34, 16) * mm, "radius": 1.5 * mm});
            skCircle(sketch, "E44.20.0.57", {"center": v(-114, 16) * mm, "radius": 1.5 * mm});
            skCircle(sketch, "E44.20.0.58", {"center": v(121, 16) * mm, "radius": 1.5 * mm});
            skCircle(sketch, "E44.20.0.59", {"center": v(-74, 16) * mm, "radius": 1.5 * mm});
            skCircle(sketch, "E44.20.0.60", {"center": v(-154, 16) * mm, "radius": 1.5 * mm});
            skCircle(sketch, "E44.20.0.61", {"center": v(161, 16) * mm, "radius": 1.5 * mm});
            skCircle(sketch, "E44.20.0.62", {"center": v(81, 16) * mm, "radius": 1.5 * mm});
            skCircle(sketch, "E44.20.0.63", {"center": v(1, 16) * mm, "radius": 1.5 * mm});
            skCircle(sketch, "E44.20.0.64", {"center": v(46, 16) * mm, "radius": 1.5 * mm});
            skCircle(sketch, "E44.20.0.65", {"center": v(-29, 16) * mm, "radius": 1.5 * mm});
            skCircle(sketch, "E44.20.0.66", {"center": v(-109, 16) * mm, "radius": 1.5 * mm});
            skCircle(sketch, "E44.20.0.67", {"center": v(126, 16) * mm, "radius": 1.5 * mm});
            skLineSegment(sketch, "E44.20.0.68", {"start": v(-174, 16) * mm, "end": v(-169, 16) * mm, "construction": true});
            skCircle(sketch, "E44.20.0.69", {"center": v(-174, 16) * mm, "radius": 1.5 * mm});
            skCircle(sketch, "E44.20.0.70", {"center": v(-169, 16) * mm, "radius": 1.5 * mm});
            skCircle(sketch, "E44.21.0.0", {"center": v(166, 11) * mm, "radius": 1.5 * mm});
            skCircle(sketch, "E44.21.0.1", {"center": v(21, 11) * mm, "radius": 1.5 * mm});
            skCircle(sketch, "E44.21.0.2", {"center": v(-99, 11) * mm, "radius": 1.5 * mm});
            skCircle(sketch, "E44.21.0.3", {"center": v(6, 11) * mm, "radius": 1.5 * mm});
            skCircle(sketch, "E44.21.0.4", {"center": v(-54, 11) * mm, "radius": 1.5 * mm});
            skCircle(sketch, "E44.21.0.5", {"center": v(171, 11) * mm, "radius": 1.5 * mm});
            skCircle(sketch, "E44.21.0.6", {"center": v(-104, 11) * mm, "radius": 1.5 * mm});
            skCircle(sketch, "E44.21.0.7", {"center": v(11, 11) * mm, "radius": 1.5 * mm});
            skCircle(sketch, "E44.21.0.8", {"center": v(56, 11) * mm, "radius": 1.5 * mm});
            skCircle(sketch, "E44.21.0.9", {"center": v(-134, 11) * mm, "radius": 1.5 * mm});
            skCircle(sketch, "E44.21.0.10", {"center": v(51, 11) * mm, "radius": 1.5 * mm});
            skCircle(sketch, "E44.21.0.11", {"center": v(131, 11) * mm, "radius": 1.5 * mm});
            skCircle(sketch, "E44.21.0.12", {"center": v(151, 11) * mm, "radius": 1.5 * mm});
            skCircle(sketch, "E44.21.0.13", {"center": v(-24, 11) * mm, "radius": 1.5 * mm});
            skCircle(sketch, "E44.21.0.14", {"center": v(-64, 11) * mm, "radius": 1.5 * mm});
            skCircle(sketch, "E44.21.0.15", {"center": v(-9, 11) * mm, "radius": 1.5 * mm});
            skCircle(sketch, "E44.21.0.16", {"center": v(136, 11) * mm, "radius": 1.5 * mm});
            skCircle(sketch, "E44.21.0.17", {"center": v(91, 11) * mm, "radius": 1.5 * mm});
            skCircle(sketch, "E44.21.0.18", {"center": v(101, 11) * mm, "radius": 1.5 * mm});
            skCircle(sketch, "E44.21.0.19", {"center": v(-144, 11) * mm, "radius": 1.5 * mm});
            skCircle(sketch, "E44.21.0.20", {"center": v(71, 11) * mm, "radius": 1.5 * mm});
            skCircle(sketch, "E44.21.0.21", {"center": v(-69, 11) * mm, "radius": 1.5 * mm});
            skCircle(sketch, "E44.21.0.22", {"center": v(-84, 11) * mm, "radius": 1.5 * mm});
            skCircle(sketch, "E44.21.0.23", {"center": v(116, 11) * mm, "radius": 1.5 * mm});
            skCircle(sketch, "E44.21.0.24", {"center": v(-164, 11) * mm, "radius": 1.5 * mm});
            skCircle(sketch, "E44.21.0.25", {"center": v(86, 11) * mm, "radius": 1.5 * mm});
            skCircle(sketch, "E44.21.0.26", {"center": v(-149, 11) * mm, "radius": 1.5 * mm});
            skCircle(sketch, "E44.21.0.27", {"center": v(106, 11) * mm, "radius": 1.5 * mm});
            skCircle(sketch, "E44.21.0.28", {"center": v(-94, 11) * mm, "radius": 1.5 * mm});
            skCircle(sketch, "E44.21.0.29", {"center": v(-129, 11) * mm, "radius": 1.5 * mm});
            skCircle(sketch, "E44.21.0.30", {"center": v(-19, 11) * mm, "radius": 1.5 * mm});
            skCircle(sketch, "E44.21.0.31", {"center": v(-49, 11) * mm, "radius": 1.5 * mm});
            skCircle(sketch, "E44.21.0.32", {"center": v(26, 11) * mm, "radius": 1.5 * mm});
            skCircle(sketch, "E44.21.0.33", {"center": v(61, 11) * mm, "radius": 1.5 * mm});
            skCircle(sketch, "E44.21.0.34", {"center": v(16, 11) * mm, "radius": 1.5 * mm});
            skCircle(sketch, "E44.21.0.35", {"center": v(96, 11) * mm, "radius": 1.5 * mm});
            skCircle(sketch, "E44.21.0.36", {"center": v(-139, 11) * mm, "radius": 1.5 * mm});
            skCircle(sketch, "E44.21.0.37", {"center": v(-59, 11) * mm, "radius": 1.5 * mm});
            skCircle(sketch, "E44.21.0.38", {"center": v(111, 11) * mm, "radius": 1.5 * mm});
            skCircle(sketch, "E44.21.0.39", {"center": v(146, 11) * mm, "radius": 1.5 * mm});
            skCircle(sketch, "E44.21.0.40", {"center": v(-89, 11) * mm, "radius": 1.5 * mm});
            skCircle(sketch, "E44.21.0.41", {"center": v(-44, 11) * mm, "radius": 1.5 * mm});
            skCircle(sketch, "E44.21.0.42", {"center": v(-124, 11) * mm, "radius": 1.5 * mm});
            skCircle(sketch, "E44.21.0.43", {"center": v(-14, 11) * mm, "radius": 1.5 * mm});
            skCircle(sketch, "E44.21.0.44", {"center": v(31, 11) * mm, "radius": 1.5 * mm});
            skCircle(sketch, "E44.21.0.45", {"center": v(66, 11) * mm, "radius": 1.5 * mm});
            skCircle(sketch, "E44.21.0.46", {"center": v(141, 11) * mm, "radius": 1.5 * mm});
            skCircle(sketch, "E44.21.0.47", {"center": v(36, 11) * mm, "radius": 1.5 * mm});
            skCircle(sketch, "E44.21.0.48", {"center": v(-39, 11) * mm, "radius": 1.5 * mm});
            skCircle(sketch, "E44.21.0.49", {"center": v(-119, 11) * mm, "radius": 1.5 * mm});
            skCircle(sketch, "E44.21.0.50", {"center": v(-79, 11) * mm, "radius": 1.5 * mm});
            skCircle(sketch, "E44.21.0.51", {"center": v(-159, 11) * mm, "radius": 1.5 * mm});
            skCircle(sketch, "E44.21.0.52", {"center": v(156, 11) * mm, "radius": 1.5 * mm});
            skCircle(sketch, "E44.21.0.53", {"center": v(76, 11) * mm, "radius": 1.5 * mm});
            skCircle(sketch, "E44.21.0.54", {"center": v(-4, 11) * mm, "radius": 1.5 * mm});
            skCircle(sketch, "E44.21.0.55", {"center": v(41, 11) * mm, "radius": 1.5 * mm});
            skCircle(sketch, "E44.21.0.56", {"center": v(-34, 11) * mm, "radius": 1.5 * mm});
            skCircle(sketch, "E44.21.0.57", {"center": v(-114, 11) * mm, "radius": 1.5 * mm});
            skCircle(sketch, "E44.21.0.58", {"center": v(121, 11) * mm, "radius": 1.5 * mm});
            skCircle(sketch, "E44.21.0.59", {"center": v(-74, 11) * mm, "radius": 1.5 * mm});
            skCircle(sketch, "E44.21.0.60", {"center": v(-154, 11) * mm, "radius": 1.5 * mm});
            skCircle(sketch, "E44.21.0.61", {"center": v(161, 11) * mm, "radius": 1.5 * mm});
            skCircle(sketch, "E44.21.0.62", {"center": v(81, 11) * mm, "radius": 1.5 * mm});
            skCircle(sketch, "E44.21.0.63", {"center": v(1, 11) * mm, "radius": 1.5 * mm});
            skCircle(sketch, "E44.21.0.64", {"center": v(46, 11) * mm, "radius": 1.5 * mm});
            skCircle(sketch, "E44.21.0.65", {"center": v(-29, 11) * mm, "radius": 1.5 * mm});
            skCircle(sketch, "E44.21.0.66", {"center": v(-109, 11) * mm, "radius": 1.5 * mm});
            skCircle(sketch, "E44.21.0.67", {"center": v(126, 11) * mm, "radius": 1.5 * mm});
            skLineSegment(sketch, "E44.21.0.68", {"start": v(-174, 11) * mm, "end": v(-169, 11) * mm, "construction": true});
            skCircle(sketch, "E44.21.0.69", {"center": v(-174, 11) * mm, "radius": 1.5 * mm});
            skCircle(sketch, "E44.21.0.70", {"center": v(-169, 11) * mm, "radius": 1.5 * mm});
            skCircle(sketch, "E44.22.0.0", {"center": v(166, 6) * mm, "radius": 1.5 * mm});
            skCircle(sketch, "E44.22.0.1", {"center": v(21, 6) * mm, "radius": 1.5 * mm});
            skCircle(sketch, "E44.22.0.2", {"center": v(-99, 6) * mm, "radius": 1.5 * mm});
            skCircle(sketch, "E44.22.0.3", {"center": v(6, 6) * mm, "radius": 1.5 * mm});
            skCircle(sketch, "E44.22.0.4", {"center": v(-54, 6) * mm, "radius": 1.5 * mm});
            skCircle(sketch, "E44.22.0.5", {"center": v(171, 6) * mm, "radius": 1.5 * mm});
            skCircle(sketch, "E44.22.0.6", {"center": v(-104, 6) * mm, "radius": 1.5 * mm});
            skCircle(sketch, "E44.22.0.7", {"center": v(11, 6) * mm, "radius": 1.5 * mm});
            skCircle(sketch, "E44.22.0.8", {"center": v(56, 6) * mm, "radius": 1.5 * mm});
            skCircle(sketch, "E44.22.0.9", {"center": v(-134, 6) * mm, "radius": 1.5 * mm});
            skCircle(sketch, "E44.22.0.10", {"center": v(51, 6) * mm, "radius": 1.5 * mm});
            skCircle(sketch, "E44.22.0.11", {"center": v(131, 6) * mm, "radius": 1.5 * mm});
            skCircle(sketch, "E44.22.0.12", {"center": v(151, 6) * mm, "radius": 1.5 * mm});
            skCircle(sketch, "E44.22.0.13", {"center": v(-24, 6) * mm, "radius": 1.5 * mm});
            skCircle(sketch, "E44.22.0.14", {"center": v(-64, 6) * mm, "radius": 1.5 * mm});
            skCircle(sketch, "E44.22.0.15", {"center": v(-9, 6) * mm, "radius": 1.5 * mm});
            skCircle(sketch, "E44.22.0.16", {"center": v(136, 6) * mm, "radius": 1.5 * mm});
            skCircle(sketch, "E44.22.0.17", {"center": v(91, 6) * mm, "radius": 1.5 * mm});
            skCircle(sketch, "E44.22.0.18", {"center": v(101, 6) * mm, "radius": 1.5 * mm});
            skCircle(sketch, "E44.22.0.19", {"center": v(-144, 6) * mm, "radius": 1.5 * mm});
            skCircle(sketch, "E44.22.0.20", {"center": v(71, 6) * mm, "radius": 1.5 * mm});
            skCircle(sketch, "E44.22.0.21", {"center": v(-69, 6) * mm, "radius": 1.5 * mm});
            skCircle(sketch, "E44.22.0.22", {"center": v(-84, 6) * mm, "radius": 1.5 * mm});
            skCircle(sketch, "E44.22.0.23", {"center": v(116, 6) * mm, "radius": 1.5 * mm});
            skCircle(sketch, "E44.22.0.24", {"center": v(-164, 6) * mm, "radius": 1.5 * mm});
            skCircle(sketch, "E44.22.0.25", {"center": v(86, 6) * mm, "radius": 1.5 * mm});
            skCircle(sketch, "E44.22.0.26", {"center": v(-149, 6) * mm, "radius": 1.5 * mm});
            skCircle(sketch, "E44.22.0.27", {"center": v(106, 6) * mm, "radius": 1.5 * mm});
            skCircle(sketch, "E44.22.0.28", {"center": v(-94, 6) * mm, "radius": 1.5 * mm});
            skCircle(sketch, "E44.22.0.29", {"center": v(-129, 6) * mm, "radius": 1.5 * mm});
            skCircle(sketch, "E44.22.0.30", {"center": v(-19, 6) * mm, "radius": 1.5 * mm});
            skCircle(sketch, "E44.22.0.31", {"center": v(-49, 6) * mm, "radius": 1.5 * mm});
            skCircle(sketch, "E44.22.0.32", {"center": v(26, 6) * mm, "radius": 1.5 * mm});
            skCircle(sketch, "E44.22.0.33", {"center": v(61, 6) * mm, "radius": 1.5 * mm});
            skCircle(sketch, "E44.22.0.34", {"center": v(16, 6) * mm, "radius": 1.5 * mm});
            skCircle(sketch, "E44.22.0.35", {"center": v(96, 6) * mm, "radius": 1.5 * mm});
            skCircle(sketch, "E44.22.0.36", {"center": v(-139, 6) * mm, "radius": 1.5 * mm});
            skCircle(sketch, "E44.22.0.37", {"center": v(-59, 6) * mm, "radius": 1.5 * mm});
            skCircle(sketch, "E44.22.0.38", {"center": v(111, 6) * mm, "radius": 1.5 * mm});
            skCircle(sketch, "E44.22.0.39", {"center": v(146, 6) * mm, "radius": 1.5 * mm});
            skCircle(sketch, "E44.22.0.40", {"center": v(-89, 6) * mm, "radius": 1.5 * mm});
            skCircle(sketch, "E44.22.0.41", {"center": v(-44, 6) * mm, "radius": 1.5 * mm});
            skCircle(sketch, "E44.22.0.42", {"center": v(-124, 6) * mm, "radius": 1.5 * mm});
            skCircle(sketch, "E44.22.0.43", {"center": v(-14, 6) * mm, "radius": 1.5 * mm});
            skCircle(sketch, "E44.22.0.44", {"center": v(31, 6) * mm, "radius": 1.5 * mm});
            skCircle(sketch, "E44.22.0.45", {"center": v(66, 6) * mm, "radius": 1.5 * mm});
            skCircle(sketch, "E44.22.0.46", {"center": v(141, 6) * mm, "radius": 1.5 * mm});
            skCircle(sketch, "E44.22.0.47", {"center": v(36, 6) * mm, "radius": 1.5 * mm});
            skCircle(sketch, "E44.22.0.48", {"center": v(-39, 6) * mm, "radius": 1.5 * mm});
            skCircle(sketch, "E44.22.0.49", {"center": v(-119, 6) * mm, "radius": 1.5 * mm});
            skCircle(sketch, "E44.22.0.50", {"center": v(-79, 6) * mm, "radius": 1.5 * mm});
            skCircle(sketch, "E44.22.0.51", {"center": v(-159, 6) * mm, "radius": 1.5 * mm});
            skCircle(sketch, "E44.22.0.52", {"center": v(156, 6) * mm, "radius": 1.5 * mm});
            skCircle(sketch, "E44.22.0.53", {"center": v(76, 6) * mm, "radius": 1.5 * mm});
            skCircle(sketch, "E44.22.0.54", {"center": v(-4, 6) * mm, "radius": 1.5 * mm});
            skCircle(sketch, "E44.22.0.55", {"center": v(41, 6) * mm, "radius": 1.5 * mm});
            skCircle(sketch, "E44.22.0.56", {"center": v(-34, 6) * mm, "radius": 1.5 * mm});
            skCircle(sketch, "E44.22.0.57", {"center": v(-114, 6) * mm, "radius": 1.5 * mm});
            skCircle(sketch, "E44.22.0.58", {"center": v(121, 6) * mm, "radius": 1.5 * mm});
            skCircle(sketch, "E44.22.0.59", {"center": v(-74, 6) * mm, "radius": 1.5 * mm});
            skCircle(sketch, "E44.22.0.60", {"center": v(-154, 6) * mm, "radius": 1.5 * mm});
            skCircle(sketch, "E44.22.0.61", {"center": v(161, 6) * mm, "radius": 1.5 * mm});
            skCircle(sketch, "E44.22.0.62", {"center": v(81, 6) * mm, "radius": 1.5 * mm});
            skCircle(sketch, "E44.22.0.63", {"center": v(1, 6) * mm, "radius": 1.5 * mm});
            skCircle(sketch, "E44.22.0.64", {"center": v(46, 6) * mm, "radius": 1.5 * mm});
            skCircle(sketch, "E44.22.0.65", {"center": v(-29, 6) * mm, "radius": 1.5 * mm});
            skCircle(sketch, "E44.22.0.66", {"center": v(-109, 6) * mm, "radius": 1.5 * mm});
            skCircle(sketch, "E44.22.0.67", {"center": v(126, 6) * mm, "radius": 1.5 * mm});
            skLineSegment(sketch, "E44.22.0.68", {"start": v(-174, 6) * mm, "end": v(-169, 6) * mm, "construction": true});
            skCircle(sketch, "E44.22.0.69", {"center": v(-174, 6) * mm, "radius": 1.5 * mm});
            skCircle(sketch, "E44.22.0.70", {"center": v(-169, 6) * mm, "radius": 1.5 * mm});
            skCircle(sketch, "E44.23.0.0", {"center": v(166, 1) * mm, "radius": 1.5 * mm});
            skCircle(sketch, "E44.23.0.1", {"center": v(21, 1) * mm, "radius": 1.5 * mm});
            skCircle(sketch, "E44.23.0.2", {"center": v(-99, 1) * mm, "radius": 1.5 * mm});
            skCircle(sketch, "E44.23.0.3", {"center": v(6, 1) * mm, "radius": 1.5 * mm});
            skCircle(sketch, "E44.23.0.4", {"center": v(-54, 1) * mm, "radius": 1.5 * mm});
            skCircle(sketch, "E44.23.0.5", {"center": v(171, 1) * mm, "radius": 1.5 * mm});
            skCircle(sketch, "E44.23.0.6", {"center": v(-104, 1) * mm, "radius": 1.5 * mm});
            skCircle(sketch, "E44.23.0.7", {"center": v(11, 1) * mm, "radius": 1.5 * mm});
            skCircle(sketch, "E44.23.0.8", {"center": v(56, 1) * mm, "radius": 1.5 * mm});
            skCircle(sketch, "E44.23.0.9", {"center": v(-134, 1) * mm, "radius": 1.5 * mm});
            skCircle(sketch, "E44.23.0.10", {"center": v(51, 1) * mm, "radius": 1.5 * mm});
            skCircle(sketch, "E44.23.0.11", {"center": v(131, 1) * mm, "radius": 1.5 * mm});
            skCircle(sketch, "E44.23.0.12", {"center": v(151, 1) * mm, "radius": 1.5 * mm});
            skCircle(sketch, "E44.23.0.13", {"center": v(-24, 1) * mm, "radius": 1.5 * mm});
            skCircle(sketch, "E44.23.0.14", {"center": v(-64, 1) * mm, "radius": 1.5 * mm});
            skCircle(sketch, "E44.23.0.15", {"center": v(-9, 1) * mm, "radius": 1.5 * mm});
            skCircle(sketch, "E44.23.0.16", {"center": v(136, 1) * mm, "radius": 1.5 * mm});
            skCircle(sketch, "E44.23.0.17", {"center": v(91, 1) * mm, "radius": 1.5 * mm});
            skCircle(sketch, "E44.23.0.18", {"center": v(101, 1) * mm, "radius": 1.5 * mm});
            skCircle(sketch, "E44.23.0.19", {"center": v(-144, 1) * mm, "radius": 1.5 * mm});
            skCircle(sketch, "E44.23.0.20", {"center": v(71, 1) * mm, "radius": 1.5 * mm});
            skCircle(sketch, "E44.23.0.21", {"center": v(-69, 1) * mm, "radius": 1.5 * mm});
            skCircle(sketch, "E44.23.0.22", {"center": v(-84, 1) * mm, "radius": 1.5 * mm});
            skCircle(sketch, "E44.23.0.23", {"center": v(116, 1) * mm, "radius": 1.5 * mm});
            skCircle(sketch, "E44.23.0.24", {"center": v(-164, 1) * mm, "radius": 1.5 * mm});
            skCircle(sketch, "E44.23.0.25", {"center": v(86, 1) * mm, "radius": 1.5 * mm});
            skCircle(sketch, "E44.23.0.26", {"center": v(-149, 1) * mm, "radius": 1.5 * mm});
            skCircle(sketch, "E44.23.0.27", {"center": v(106, 1) * mm, "radius": 1.5 * mm});
            skCircle(sketch, "E44.23.0.28", {"center": v(-94, 1) * mm, "radius": 1.5 * mm});
            skCircle(sketch, "E44.23.0.29", {"center": v(-129, 1) * mm, "radius": 1.5 * mm});
            skCircle(sketch, "E44.23.0.30", {"center": v(-19, 1) * mm, "radius": 1.5 * mm});
            skCircle(sketch, "E44.23.0.31", {"center": v(-49, 1) * mm, "radius": 1.5 * mm});
            skCircle(sketch, "E44.23.0.32", {"center": v(26, 1) * mm, "radius": 1.5 * mm});
            skCircle(sketch, "E44.23.0.33", {"center": v(61, 1) * mm, "radius": 1.5 * mm});
            skCircle(sketch, "E44.23.0.34", {"center": v(16, 1) * mm, "radius": 1.5 * mm});
            skCircle(sketch, "E44.23.0.35", {"center": v(96, 1) * mm, "radius": 1.5 * mm});
            skCircle(sketch, "E44.23.0.36", {"center": v(-139, 1) * mm, "radius": 1.5 * mm});
            skCircle(sketch, "E44.23.0.37", {"center": v(-59, 1) * mm, "radius": 1.5 * mm});
            skCircle(sketch, "E44.23.0.38", {"center": v(111, 1) * mm, "radius": 1.5 * mm});
            skCircle(sketch, "E44.23.0.39", {"center": v(146, 1) * mm, "radius": 1.5 * mm});
            skCircle(sketch, "E44.23.0.40", {"center": v(-89, 1) * mm, "radius": 1.5 * mm});
            skCircle(sketch, "E44.23.0.41", {"center": v(-44, 1) * mm, "radius": 1.5 * mm});
            skCircle(sketch, "E44.23.0.42", {"center": v(-124, 1) * mm, "radius": 1.5 * mm});
            skCircle(sketch, "E44.23.0.43", {"center": v(-14, 1) * mm, "radius": 1.5 * mm});
            skCircle(sketch, "E44.23.0.44", {"center": v(31, 1) * mm, "radius": 1.5 * mm});
            skCircle(sketch, "E44.23.0.45", {"center": v(66, 1) * mm, "radius": 1.5 * mm});
            skCircle(sketch, "E44.23.0.46", {"center": v(141, 1) * mm, "radius": 1.5 * mm});
            skCircle(sketch, "E44.23.0.47", {"center": v(36, 1) * mm, "radius": 1.5 * mm});
            skCircle(sketch, "E44.23.0.48", {"center": v(-39, 1) * mm, "radius": 1.5 * mm});
            skCircle(sketch, "E44.23.0.49", {"center": v(-119, 1) * mm, "radius": 1.5 * mm});
            skCircle(sketch, "E44.23.0.50", {"center": v(-79, 1) * mm, "radius": 1.5 * mm});
            skCircle(sketch, "E44.23.0.51", {"center": v(-159, 1) * mm, "radius": 1.5 * mm});
            skCircle(sketch, "E44.23.0.52", {"center": v(156, 1) * mm, "radius": 1.5 * mm});
            skCircle(sketch, "E44.23.0.53", {"center": v(76, 1) * mm, "radius": 1.5 * mm});
            skCircle(sketch, "E44.23.0.54", {"center": v(-4, 1) * mm, "radius": 1.5 * mm});
            skCircle(sketch, "E44.23.0.55", {"center": v(41, 1) * mm, "radius": 1.5 * mm});
            skCircle(sketch, "E44.23.0.56", {"center": v(-34, 1) * mm, "radius": 1.5 * mm});
            skCircle(sketch, "E44.23.0.57", {"center": v(-114, 1) * mm, "radius": 1.5 * mm});
            skCircle(sketch, "E44.23.0.58", {"center": v(121, 1) * mm, "radius": 1.5 * mm});
            skCircle(sketch, "E44.23.0.59", {"center": v(-74, 1) * mm, "radius": 1.5 * mm});
            skCircle(sketch, "E44.23.0.60", {"center": v(-154, 1) * mm, "radius": 1.5 * mm});
            skCircle(sketch, "E44.23.0.61", {"center": v(161, 1) * mm, "radius": 1.5 * mm});
            skCircle(sketch, "E44.23.0.62", {"center": v(81, 1) * mm, "radius": 1.5 * mm});
            skCircle(sketch, "E44.23.0.63", {"center": v(1, 1) * mm, "radius": 1.5 * mm});
            skCircle(sketch, "E44.23.0.64", {"center": v(46, 1) * mm, "radius": 1.5 * mm});
            skCircle(sketch, "E44.23.0.65", {"center": v(-29, 1) * mm, "radius": 1.5 * mm});
            skCircle(sketch, "E44.23.0.66", {"center": v(-109, 1) * mm, "radius": 1.5 * mm});
            skCircle(sketch, "E44.23.0.67", {"center": v(126, 1) * mm, "radius": 1.5 * mm});
            skLineSegment(sketch, "E44.23.0.68", {"start": v(-174, 1) * mm, "end": v(-169, 1) * mm, "construction": true});
            skCircle(sketch, "E44.23.0.69", {"center": v(-174, 1) * mm, "radius": 1.5 * mm});
            skCircle(sketch, "E44.23.0.70", {"center": v(-169, 1) * mm, "radius": 1.5 * mm});
            skCircle(sketch, "E44.24.0.0", {"center": v(166, -4) * mm, "radius": 1.5 * mm});
            skCircle(sketch, "E44.24.0.1", {"center": v(21, -4) * mm, "radius": 1.5 * mm});
            skCircle(sketch, "E44.24.0.2", {"center": v(-99, -4) * mm, "radius": 1.5 * mm});
            skCircle(sketch, "E44.24.0.3", {"center": v(6, -4) * mm, "radius": 1.5 * mm});
            skCircle(sketch, "E44.24.0.4", {"center": v(-54, -4) * mm, "radius": 1.5 * mm});
            skCircle(sketch, "E44.24.0.5", {"center": v(171, -4) * mm, "radius": 1.5 * mm});
            skCircle(sketch, "E44.24.0.6", {"center": v(-104, -4) * mm, "radius": 1.5 * mm});
            skCircle(sketch, "E44.24.0.7", {"center": v(11, -4) * mm, "radius": 1.5 * mm});
            skCircle(sketch, "E44.24.0.8", {"center": v(56, -4) * mm, "radius": 1.5 * mm});
            skCircle(sketch, "E44.24.0.9", {"center": v(-134, -4) * mm, "radius": 1.5 * mm});
            skCircle(sketch, "E44.24.0.10", {"center": v(51, -4) * mm, "radius": 1.5 * mm});
            skCircle(sketch, "E44.24.0.11", {"center": v(131, -4) * mm, "radius": 1.5 * mm});
            skCircle(sketch, "E44.24.0.12", {"center": v(151, -4) * mm, "radius": 1.5 * mm});
            skCircle(sketch, "E44.24.0.13", {"center": v(-24, -4) * mm, "radius": 1.5 * mm});
            skCircle(sketch, "E44.24.0.14", {"center": v(-64, -4) * mm, "radius": 1.5 * mm});
            skCircle(sketch, "E44.24.0.15", {"center": v(-9, -4) * mm, "radius": 1.5 * mm});
            skCircle(sketch, "E44.24.0.16", {"center": v(136, -4) * mm, "radius": 1.5 * mm});
            skCircle(sketch, "E44.24.0.17", {"center": v(91, -4) * mm, "radius": 1.5 * mm});
            skCircle(sketch, "E44.24.0.18", {"center": v(101, -4) * mm, "radius": 1.5 * mm});
            skCircle(sketch, "E44.24.0.19", {"center": v(-144, -4) * mm, "radius": 1.5 * mm});
            skCircle(sketch, "E44.24.0.20", {"center": v(71, -4) * mm, "radius": 1.5 * mm});
            skCircle(sketch, "E44.24.0.21", {"center": v(-69, -4) * mm, "radius": 1.5 * mm});
            skCircle(sketch, "E44.24.0.22", {"center": v(-84, -4) * mm, "radius": 1.5 * mm});
            skCircle(sketch, "E44.24.0.23", {"center": v(116, -4) * mm, "radius": 1.5 * mm});
            skCircle(sketch, "E44.24.0.24", {"center": v(-164, -4) * mm, "radius": 1.5 * mm});
            skCircle(sketch, "E44.24.0.25", {"center": v(86, -4) * mm, "radius": 1.5 * mm});
            skCircle(sketch, "E44.24.0.26", {"center": v(-149, -4) * mm, "radius": 1.5 * mm});
            skCircle(sketch, "E44.24.0.27", {"center": v(106, -4) * mm, "radius": 1.5 * mm});
            skCircle(sketch, "E44.24.0.28", {"center": v(-94, -4) * mm, "radius": 1.5 * mm});
            skCircle(sketch, "E44.24.0.29", {"center": v(-129, -4) * mm, "radius": 1.5 * mm});
            skCircle(sketch, "E44.24.0.30", {"center": v(-19, -4) * mm, "radius": 1.5 * mm});
            skCircle(sketch, "E44.24.0.31", {"center": v(-49, -4) * mm, "radius": 1.5 * mm});
            skCircle(sketch, "E44.24.0.32", {"center": v(26, -4) * mm, "radius": 1.5 * mm});
            skCircle(sketch, "E44.24.0.33", {"center": v(61, -4) * mm, "radius": 1.5 * mm});
            skCircle(sketch, "E44.24.0.34", {"center": v(16, -4) * mm, "radius": 1.5 * mm});
            skCircle(sketch, "E44.24.0.35", {"center": v(96, -4) * mm, "radius": 1.5 * mm});
            skCircle(sketch, "E44.24.0.36", {"center": v(-139, -4) * mm, "radius": 1.5 * mm});
            skCircle(sketch, "E44.24.0.37", {"center": v(-59, -4) * mm, "radius": 1.5 * mm});
            skCircle(sketch, "E44.24.0.38", {"center": v(111, -4) * mm, "radius": 1.5 * mm});
            skCircle(sketch, "E44.24.0.39", {"center": v(146, -4) * mm, "radius": 1.5 * mm});
            skCircle(sketch, "E44.24.0.40", {"center": v(-89, -4) * mm, "radius": 1.5 * mm});
            skCircle(sketch, "E44.24.0.41", {"center": v(-44, -4) * mm, "radius": 1.5 * mm});
            skCircle(sketch, "E44.24.0.42", {"center": v(-124, -4) * mm, "radius": 1.5 * mm});
            skCircle(sketch, "E44.24.0.43", {"center": v(-14, -4) * mm, "radius": 1.5 * mm});
            skCircle(sketch, "E44.24.0.44", {"center": v(31, -4) * mm, "radius": 1.5 * mm});
            skCircle(sketch, "E44.24.0.45", {"center": v(66, -4) * mm, "radius": 1.5 * mm});
            skCircle(sketch, "E44.24.0.46", {"center": v(141, -4) * mm, "radius": 1.5 * mm});
            skCircle(sketch, "E44.24.0.47", {"center": v(36, -4) * mm, "radius": 1.5 * mm});
            skCircle(sketch, "E44.24.0.48", {"center": v(-39, -4) * mm, "radius": 1.5 * mm});
            skCircle(sketch, "E44.24.0.49", {"center": v(-119, -4) * mm, "radius": 1.5 * mm});
            skCircle(sketch, "E44.24.0.50", {"center": v(-79, -4) * mm, "radius": 1.5 * mm});
            skCircle(sketch, "E44.24.0.51", {"center": v(-159, -4) * mm, "radius": 1.5 * mm});
            skCircle(sketch, "E44.24.0.52", {"center": v(156, -4) * mm, "radius": 1.5 * mm});
            skCircle(sketch, "E44.24.0.53", {"center": v(76, -4) * mm, "radius": 1.5 * mm});
            skCircle(sketch, "E44.24.0.54", {"center": v(-4, -4) * mm, "radius": 1.5 * mm});
            skCircle(sketch, "E44.24.0.55", {"center": v(41, -4) * mm, "radius": 1.5 * mm});
            skCircle(sketch, "E44.24.0.56", {"center": v(-34, -4) * mm, "radius": 1.5 * mm});
            skCircle(sketch, "E44.24.0.57", {"center": v(-114, -4) * mm, "radius": 1.5 * mm});
            skCircle(sketch, "E44.24.0.58", {"center": v(121, -4) * mm, "radius": 1.5 * mm});
            skCircle(sketch, "E44.24.0.59", {"center": v(-74, -4) * mm, "radius": 1.5 * mm});
            skCircle(sketch, "E44.24.0.60", {"center": v(-154, -4) * mm, "radius": 1.5 * mm});
            skCircle(sketch, "E44.24.0.61", {"center": v(161, -4) * mm, "radius": 1.5 * mm});
            skCircle(sketch, "E44.24.0.62", {"center": v(81, -4) * mm, "radius": 1.5 * mm});
            skCircle(sketch, "E44.24.0.63", {"center": v(1, -4) * mm, "radius": 1.5 * mm});
            skCircle(sketch, "E44.24.0.64", {"center": v(46, -4) * mm, "radius": 1.5 * mm});
            skCircle(sketch, "E44.24.0.65", {"center": v(-29, -4) * mm, "radius": 1.5 * mm});
            skCircle(sketch, "E44.24.0.66", {"center": v(-109, -4) * mm, "radius": 1.5 * mm});
            skCircle(sketch, "E44.24.0.67", {"center": v(126, -4) * mm, "radius": 1.5 * mm});
            skLineSegment(sketch, "E44.24.0.68", {"start": v(-174, -4) * mm, "end": v(-169, -4) * mm, "construction": true});
            skCircle(sketch, "E44.24.0.69", {"center": v(-174, -4) * mm, "radius": 1.5 * mm});
            skCircle(sketch, "E44.24.0.70", {"center": v(-169, -4) * mm, "radius": 1.5 * mm});
            skCircle(sketch, "E44.25.0.0", {"center": v(166, -9) * mm, "radius": 1.5 * mm});
            skCircle(sketch, "E44.25.0.1", {"center": v(21, -9) * mm, "radius": 1.5 * mm});
            skCircle(sketch, "E44.25.0.2", {"center": v(-99, -9) * mm, "radius": 1.5 * mm});
            skCircle(sketch, "E44.25.0.3", {"center": v(6, -9) * mm, "radius": 1.5 * mm});
            skCircle(sketch, "E44.25.0.4", {"center": v(-54, -9) * mm, "radius": 1.5 * mm});
            skCircle(sketch, "E44.25.0.5", {"center": v(171, -9) * mm, "radius": 1.5 * mm});
            skCircle(sketch, "E44.25.0.6", {"center": v(-104, -9) * mm, "radius": 1.5 * mm});
            skCircle(sketch, "E44.25.0.7", {"center": v(11, -9) * mm, "radius": 1.5 * mm});
            skCircle(sketch, "E44.25.0.8", {"center": v(56, -9) * mm, "radius": 1.5 * mm});
            skCircle(sketch, "E44.25.0.9", {"center": v(-134, -9) * mm, "radius": 1.5 * mm});
            skCircle(sketch, "E44.25.0.10", {"center": v(51, -9) * mm, "radius": 1.5 * mm});
            skCircle(sketch, "E44.25.0.11", {"center": v(131, -9) * mm, "radius": 1.5 * mm});
            skCircle(sketch, "E44.25.0.12", {"center": v(151, -9) * mm, "radius": 1.5 * mm});
            skCircle(sketch, "E44.25.0.13", {"center": v(-24, -9) * mm, "radius": 1.5 * mm});
            skCircle(sketch, "E44.25.0.14", {"center": v(-64, -9) * mm, "radius": 1.5 * mm});
            skCircle(sketch, "E44.25.0.15", {"center": v(-9, -9) * mm, "radius": 1.5 * mm});
            skCircle(sketch, "E44.25.0.16", {"center": v(136, -9) * mm, "radius": 1.5 * mm});
            skCircle(sketch, "E44.25.0.17", {"center": v(91, -9) * mm, "radius": 1.5 * mm});
            skCircle(sketch, "E44.25.0.18", {"center": v(101, -9) * mm, "radius": 1.5 * mm});
            skCircle(sketch, "E44.25.0.19", {"center": v(-144, -9) * mm, "radius": 1.5 * mm});
            skCircle(sketch, "E44.25.0.20", {"center": v(71, -9) * mm, "radius": 1.5 * mm});
            skCircle(sketch, "E44.25.0.21", {"center": v(-69, -9) * mm, "radius": 1.5 * mm});
            skCircle(sketch, "E44.25.0.22", {"center": v(-84, -9) * mm, "radius": 1.5 * mm});
            skCircle(sketch, "E44.25.0.23", {"center": v(116, -9) * mm, "radius": 1.5 * mm});
            skCircle(sketch, "E44.25.0.24", {"center": v(-164, -9) * mm, "radius": 1.5 * mm});
            skCircle(sketch, "E44.25.0.25", {"center": v(86, -9) * mm, "radius": 1.5 * mm});
            skCircle(sketch, "E44.25.0.26", {"center": v(-149, -9) * mm, "radius": 1.5 * mm});
            skCircle(sketch, "E44.25.0.27", {"center": v(106, -9) * mm, "radius": 1.5 * mm});
            skCircle(sketch, "E44.25.0.28", {"center": v(-94, -9) * mm, "radius": 1.5 * mm});
            skCircle(sketch, "E44.25.0.29", {"center": v(-129, -9) * mm, "radius": 1.5 * mm});
            skCircle(sketch, "E44.25.0.30", {"center": v(-19, -9) * mm, "radius": 1.5 * mm});
            skCircle(sketch, "E44.25.0.31", {"center": v(-49, -9) * mm, "radius": 1.5 * mm});
            skCircle(sketch, "E44.25.0.32", {"center": v(26, -9) * mm, "radius": 1.5 * mm});
            skCircle(sketch, "E44.25.0.33", {"center": v(61, -9) * mm, "radius": 1.5 * mm});
            skCircle(sketch, "E44.25.0.34", {"center": v(16, -9) * mm, "radius": 1.5 * mm});
            skCircle(sketch, "E44.25.0.35", {"center": v(96, -9) * mm, "radius": 1.5 * mm});
            skCircle(sketch, "E44.25.0.36", {"center": v(-139, -9) * mm, "radius": 1.5 * mm});
            skCircle(sketch, "E44.25.0.37", {"center": v(-59, -9) * mm, "radius": 1.5 * mm});
            skCircle(sketch, "E44.25.0.38", {"center": v(111, -9) * mm, "radius": 1.5 * mm});
            skCircle(sketch, "E44.25.0.39", {"center": v(146, -9) * mm, "radius": 1.5 * mm});
            skCircle(sketch, "E44.25.0.40", {"center": v(-89, -9) * mm, "radius": 1.5 * mm});
            skCircle(sketch, "E44.25.0.41", {"center": v(-44, -9) * mm, "radius": 1.5 * mm});
            skCircle(sketch, "E44.25.0.42", {"center": v(-124, -9) * mm, "radius": 1.5 * mm});
            skCircle(sketch, "E44.25.0.43", {"center": v(-14, -9) * mm, "radius": 1.5 * mm});
            skCircle(sketch, "E44.25.0.44", {"center": v(31, -9) * mm, "radius": 1.5 * mm});
            skCircle(sketch, "E44.25.0.45", {"center": v(66, -9) * mm, "radius": 1.5 * mm});
            skCircle(sketch, "E44.25.0.46", {"center": v(141, -9) * mm, "radius": 1.5 * mm});
            skCircle(sketch, "E44.25.0.47", {"center": v(36, -9) * mm, "radius": 1.5 * mm});
            skCircle(sketch, "E44.25.0.48", {"center": v(-39, -9) * mm, "radius": 1.5 * mm});
            skCircle(sketch, "E44.25.0.49", {"center": v(-119, -9) * mm, "radius": 1.5 * mm});
            skCircle(sketch, "E44.25.0.50", {"center": v(-79, -9) * mm, "radius": 1.5 * mm});
            skCircle(sketch, "E44.25.0.51", {"center": v(-159, -9) * mm, "radius": 1.5 * mm});
            skCircle(sketch, "E44.25.0.52", {"center": v(156, -9) * mm, "radius": 1.5 * mm});
            skCircle(sketch, "E44.25.0.53", {"center": v(76, -9) * mm, "radius": 1.5 * mm});
            skCircle(sketch, "E44.25.0.54", {"center": v(-4, -9) * mm, "radius": 1.5 * mm});
            skCircle(sketch, "E44.25.0.55", {"center": v(41, -9) * mm, "radius": 1.5 * mm});
            skCircle(sketch, "E44.25.0.56", {"center": v(-34, -9) * mm, "radius": 1.5 * mm});
            skCircle(sketch, "E44.25.0.57", {"center": v(-114, -9) * mm, "radius": 1.5 * mm});
            skCircle(sketch, "E44.25.0.58", {"center": v(121, -9) * mm, "radius": 1.5 * mm});
            skCircle(sketch, "E44.25.0.59", {"center": v(-74, -9) * mm, "radius": 1.5 * mm});
            skCircle(sketch, "E44.25.0.60", {"center": v(-154, -9) * mm, "radius": 1.5 * mm});
            skCircle(sketch, "E44.25.0.61", {"center": v(161, -9) * mm, "radius": 1.5 * mm});
            skCircle(sketch, "E44.25.0.62", {"center": v(81, -9) * mm, "radius": 1.5 * mm});
            skCircle(sketch, "E44.25.0.63", {"center": v(1, -9) * mm, "radius": 1.5 * mm});
            skCircle(sketch, "E44.25.0.64", {"center": v(46, -9) * mm, "radius": 1.5 * mm});
            skCircle(sketch, "E44.25.0.65", {"center": v(-29, -9) * mm, "radius": 1.5 * mm});
            skCircle(sketch, "E44.25.0.66", {"center": v(-109, -9) * mm, "radius": 1.5 * mm});
            skCircle(sketch, "E44.25.0.67", {"center": v(126, -9) * mm, "radius": 1.5 * mm});
            skLineSegment(sketch, "E44.25.0.68", {"start": v(-174, -9) * mm, "end": v(-169, -9) * mm, "construction": true});
            skCircle(sketch, "E44.25.0.69", {"center": v(-174, -9) * mm, "radius": 1.5 * mm});
            skCircle(sketch, "E44.25.0.70", {"center": v(-169, -9) * mm, "radius": 1.5 * mm});
            skCircle(sketch, "E44.26.0.0", {"center": v(166, -14) * mm, "radius": 1.5 * mm});
            skCircle(sketch, "E44.26.0.1", {"center": v(21, -14) * mm, "radius": 1.5 * mm});
            skCircle(sketch, "E44.26.0.2", {"center": v(-99, -14) * mm, "radius": 1.5 * mm});
            skCircle(sketch, "E44.26.0.3", {"center": v(6, -14) * mm, "radius": 1.5 * mm});
            skCircle(sketch, "E44.26.0.4", {"center": v(-54, -14) * mm, "radius": 1.5 * mm});
            skCircle(sketch, "E44.26.0.5", {"center": v(171, -14) * mm, "radius": 1.5 * mm});
            skCircle(sketch, "E44.26.0.6", {"center": v(-104, -14) * mm, "radius": 1.5 * mm});
            skCircle(sketch, "E44.26.0.7", {"center": v(11, -14) * mm, "radius": 1.5 * mm});
            skCircle(sketch, "E44.26.0.8", {"center": v(56, -14) * mm, "radius": 1.5 * mm});
            skCircle(sketch, "E44.26.0.9", {"center": v(-134, -14) * mm, "radius": 1.5 * mm});
            skCircle(sketch, "E44.26.0.10", {"center": v(51, -14) * mm, "radius": 1.5 * mm});
            skCircle(sketch, "E44.26.0.11", {"center": v(131, -14) * mm, "radius": 1.5 * mm});
            skCircle(sketch, "E44.26.0.12", {"center": v(151, -14) * mm, "radius": 1.5 * mm});
            skCircle(sketch, "E44.26.0.13", {"center": v(-24, -14) * mm, "radius": 1.5 * mm});
            skCircle(sketch, "E44.26.0.14", {"center": v(-64, -14) * mm, "radius": 1.5 * mm});
            skCircle(sketch, "E44.26.0.15", {"center": v(-9, -14) * mm, "radius": 1.5 * mm});
            skCircle(sketch, "E44.26.0.16", {"center": v(136, -14) * mm, "radius": 1.5 * mm});
            skCircle(sketch, "E44.26.0.17", {"center": v(91, -14) * mm, "radius": 1.5 * mm});
            skCircle(sketch, "E44.26.0.18", {"center": v(101, -14) * mm, "radius": 1.5 * mm});
            skCircle(sketch, "E44.26.0.19", {"center": v(-144, -14) * mm, "radius": 1.5 * mm});
            skCircle(sketch, "E44.26.0.20", {"center": v(71, -14) * mm, "radius": 1.5 * mm});
            skCircle(sketch, "E44.26.0.21", {"center": v(-69, -14) * mm, "radius": 1.5 * mm});
            skCircle(sketch, "E44.26.0.22", {"center": v(-84, -14) * mm, "radius": 1.5 * mm});
            skCircle(sketch, "E44.26.0.23", {"center": v(116, -14) * mm, "radius": 1.5 * mm});
            skCircle(sketch, "E44.26.0.24", {"center": v(-164, -14) * mm, "radius": 1.5 * mm});
            skCircle(sketch, "E44.26.0.25", {"center": v(86, -14) * mm, "radius": 1.5 * mm});
            skCircle(sketch, "E44.26.0.26", {"center": v(-149, -14) * mm, "radius": 1.5 * mm});
            skCircle(sketch, "E44.26.0.27", {"center": v(106, -14) * mm, "radius": 1.5 * mm});
            skCircle(sketch, "E44.26.0.28", {"center": v(-94, -14) * mm, "radius": 1.5 * mm});
            skCircle(sketch, "E44.26.0.29", {"center": v(-129, -14) * mm, "radius": 1.5 * mm});
            skCircle(sketch, "E44.26.0.30", {"center": v(-19, -14) * mm, "radius": 1.5 * mm});
            skCircle(sketch, "E44.26.0.31", {"center": v(-49, -14) * mm, "radius": 1.5 * mm});
            skCircle(sketch, "E44.26.0.32", {"center": v(26, -14) * mm, "radius": 1.5 * mm});
            skCircle(sketch, "E44.26.0.33", {"center": v(61, -14) * mm, "radius": 1.5 * mm});
            skCircle(sketch, "E44.26.0.34", {"center": v(16, -14) * mm, "radius": 1.5 * mm});
            skCircle(sketch, "E44.26.0.35", {"center": v(96, -14) * mm, "radius": 1.5 * mm});
            skCircle(sketch, "E44.26.0.36", {"center": v(-139, -14) * mm, "radius": 1.5 * mm});
            skCircle(sketch, "E44.26.0.37", {"center": v(-59, -14) * mm, "radius": 1.5 * mm});
            skCircle(sketch, "E44.26.0.38", {"center": v(111, -14) * mm, "radius": 1.5 * mm});
            skCircle(sketch, "E44.26.0.39", {"center": v(146, -14) * mm, "radius": 1.5 * mm});
            skCircle(sketch, "E44.26.0.40", {"center": v(-89, -14) * mm, "radius": 1.5 * mm});
            skCircle(sketch, "E44.26.0.41", {"center": v(-44, -14) * mm, "radius": 1.5 * mm});
            skCircle(sketch, "E44.26.0.42", {"center": v(-124, -14) * mm, "radius": 1.5 * mm});
            skCircle(sketch, "E44.26.0.43", {"center": v(-14, -14) * mm, "radius": 1.5 * mm});
            skCircle(sketch, "E44.26.0.44", {"center": v(31, -14) * mm, "radius": 1.5 * mm});
            skCircle(sketch, "E44.26.0.45", {"center": v(66, -14) * mm, "radius": 1.5 * mm});
            skCircle(sketch, "E44.26.0.46", {"center": v(141, -14) * mm, "radius": 1.5 * mm});
            skCircle(sketch, "E44.26.0.47", {"center": v(36, -14) * mm, "radius": 1.5 * mm});
            skCircle(sketch, "E44.26.0.48", {"center": v(-39, -14) * mm, "radius": 1.5 * mm});
            skCircle(sketch, "E44.26.0.49", {"center": v(-119, -14) * mm, "radius": 1.5 * mm});
            skCircle(sketch, "E44.26.0.50", {"center": v(-79, -14) * mm, "radius": 1.5 * mm});
            skCircle(sketch, "E44.26.0.51", {"center": v(-159, -14) * mm, "radius": 1.5 * mm});
            skCircle(sketch, "E44.26.0.52", {"center": v(156, -14) * mm, "radius": 1.5 * mm});
            skCircle(sketch, "E44.26.0.53", {"center": v(76, -14) * mm, "radius": 1.5 * mm});
            skCircle(sketch, "E44.26.0.54", {"center": v(-4, -14) * mm, "radius": 1.5 * mm});
            skCircle(sketch, "E44.26.0.55", {"center": v(41, -14) * mm, "radius": 1.5 * mm});
            skCircle(sketch, "E44.26.0.56", {"center": v(-34, -14) * mm, "radius": 1.5 * mm});
            skCircle(sketch, "E44.26.0.57", {"center": v(-114, -14) * mm, "radius": 1.5 * mm});
            skCircle(sketch, "E44.26.0.58", {"center": v(121, -14) * mm, "radius": 1.5 * mm});
            skCircle(sketch, "E44.26.0.59", {"center": v(-74, -14) * mm, "radius": 1.5 * mm});
            skCircle(sketch, "E44.26.0.60", {"center": v(-154, -14) * mm, "radius": 1.5 * mm});
            skCircle(sketch, "E44.26.0.61", {"center": v(161, -14) * mm, "radius": 1.5 * mm});
            skCircle(sketch, "E44.26.0.62", {"center": v(81, -14) * mm, "radius": 1.5 * mm});
            skCircle(sketch, "E44.26.0.63", {"center": v(1, -14) * mm, "radius": 1.5 * mm});
            skCircle(sketch, "E44.26.0.64", {"center": v(46, -14) * mm, "radius": 1.5 * mm});
            skCircle(sketch, "E44.26.0.65", {"center": v(-29, -14) * mm, "radius": 1.5 * mm});
            skCircle(sketch, "E44.26.0.66", {"center": v(-109, -14) * mm, "radius": 1.5 * mm});
            skCircle(sketch, "E44.26.0.67", {"center": v(126, -14) * mm, "radius": 1.5 * mm});
            skLineSegment(sketch, "E44.26.0.68", {"start": v(-174, -14) * mm, "end": v(-169, -14) * mm, "construction": true});
            skCircle(sketch, "E44.26.0.69", {"center": v(-174, -14) * mm, "radius": 1.5 * mm});
            skCircle(sketch, "E44.26.0.70", {"center": v(-169, -14) * mm, "radius": 1.5 * mm});
            skCircle(sketch, "E44.27.0.0", {"center": v(166, -19) * mm, "radius": 1.5 * mm});
            skCircle(sketch, "E44.27.0.1", {"center": v(21, -19) * mm, "radius": 1.5 * mm});
            skCircle(sketch, "E44.27.0.2", {"center": v(-99, -19) * mm, "radius": 1.5 * mm});
            skCircle(sketch, "E44.27.0.3", {"center": v(6, -19) * mm, "radius": 1.5 * mm});
            skCircle(sketch, "E44.27.0.4", {"center": v(-54, -19) * mm, "radius": 1.5 * mm});
            skCircle(sketch, "E44.27.0.5", {"center": v(171, -19) * mm, "radius": 1.5 * mm});
            skCircle(sketch, "E44.27.0.6", {"center": v(-104, -19) * mm, "radius": 1.5 * mm});
            skCircle(sketch, "E44.27.0.7", {"center": v(11, -19) * mm, "radius": 1.5 * mm});
            skCircle(sketch, "E44.27.0.8", {"center": v(56, -19) * mm, "radius": 1.5 * mm});
            skCircle(sketch, "E44.27.0.9", {"center": v(-134, -19) * mm, "radius": 1.5 * mm});
            skCircle(sketch, "E44.27.0.10", {"center": v(51, -19) * mm, "radius": 1.5 * mm});
            skCircle(sketch, "E44.27.0.11", {"center": v(131, -19) * mm, "radius": 1.5 * mm});
            skCircle(sketch, "E44.27.0.12", {"center": v(151, -19) * mm, "radius": 1.5 * mm});
            skCircle(sketch, "E44.27.0.13", {"center": v(-24, -19) * mm, "radius": 1.5 * mm});
            skCircle(sketch, "E44.27.0.14", {"center": v(-64, -19) * mm, "radius": 1.5 * mm});
            skCircle(sketch, "E44.27.0.15", {"center": v(-9, -19) * mm, "radius": 1.5 * mm});
            skCircle(sketch, "E44.27.0.16", {"center": v(136, -19) * mm, "radius": 1.5 * mm});
            skCircle(sketch, "E44.27.0.17", {"center": v(91, -19) * mm, "radius": 1.5 * mm});
            skCircle(sketch, "E44.27.0.18", {"center": v(101, -19) * mm, "radius": 1.5 * mm});
            skCircle(sketch, "E44.27.0.19", {"center": v(-144, -19) * mm, "radius": 1.5 * mm});
            skCircle(sketch, "E44.27.0.20", {"center": v(71, -19) * mm, "radius": 1.5 * mm});
            skCircle(sketch, "E44.27.0.21", {"center": v(-69, -19) * mm, "radius": 1.5 * mm});
            skCircle(sketch, "E44.27.0.22", {"center": v(-84, -19) * mm, "radius": 1.5 * mm});
            skCircle(sketch, "E44.27.0.23", {"center": v(116, -19) * mm, "radius": 1.5 * mm});
            skCircle(sketch, "E44.27.0.24", {"center": v(-164, -19) * mm, "radius": 1.5 * mm});
            skCircle(sketch, "E44.27.0.25", {"center": v(86, -19) * mm, "radius": 1.5 * mm});
            skCircle(sketch, "E44.27.0.26", {"center": v(-149, -19) * mm, "radius": 1.5 * mm});
            skCircle(sketch, "E44.27.0.27", {"center": v(106, -19) * mm, "radius": 1.5 * mm});
            skCircle(sketch, "E44.27.0.28", {"center": v(-94, -19) * mm, "radius": 1.5 * mm});
            skCircle(sketch, "E44.27.0.29", {"center": v(-129, -19) * mm, "radius": 1.5 * mm});
            skCircle(sketch, "E44.27.0.30", {"center": v(-19, -19) * mm, "radius": 1.5 * mm});
            skCircle(sketch, "E44.27.0.31", {"center": v(-49, -19) * mm, "radius": 1.5 * mm});
            skCircle(sketch, "E44.27.0.32", {"center": v(26, -19) * mm, "radius": 1.5 * mm});
            skCircle(sketch, "E44.27.0.33", {"center": v(61, -19) * mm, "radius": 1.5 * mm});
            skCircle(sketch, "E44.27.0.34", {"center": v(16, -19) * mm, "radius": 1.5 * mm});
            skCircle(sketch, "E44.27.0.35", {"center": v(96, -19) * mm, "radius": 1.5 * mm});
            skCircle(sketch, "E44.27.0.36", {"center": v(-139, -19) * mm, "radius": 1.5 * mm});
            skCircle(sketch, "E44.27.0.37", {"center": v(-59, -19) * mm, "radius": 1.5 * mm});
            skCircle(sketch, "E44.27.0.38", {"center": v(111, -19) * mm, "radius": 1.5 * mm});
            skCircle(sketch, "E44.27.0.39", {"center": v(146, -19) * mm, "radius": 1.5 * mm});
            skCircle(sketch, "E44.27.0.40", {"center": v(-89, -19) * mm, "radius": 1.5 * mm});
            skCircle(sketch, "E44.27.0.41", {"center": v(-44, -19) * mm, "radius": 1.5 * mm});
            skCircle(sketch, "E44.27.0.42", {"center": v(-124, -19) * mm, "radius": 1.5 * mm});
            skCircle(sketch, "E44.27.0.43", {"center": v(-14, -19) * mm, "radius": 1.5 * mm});
            skCircle(sketch, "E44.27.0.44", {"center": v(31, -19) * mm, "radius": 1.5 * mm});
            skCircle(sketch, "E44.27.0.45", {"center": v(66, -19) * mm, "radius": 1.5 * mm});
            skCircle(sketch, "E44.27.0.46", {"center": v(141, -19) * mm, "radius": 1.5 * mm});
            skCircle(sketch, "E44.27.0.47", {"center": v(36, -19) * mm, "radius": 1.5 * mm});
            skCircle(sketch, "E44.27.0.48", {"center": v(-39, -19) * mm, "radius": 1.5 * mm});
            skCircle(sketch, "E44.27.0.49", {"center": v(-119, -19) * mm, "radius": 1.5 * mm});
            skCircle(sketch, "E44.27.0.50", {"center": v(-79, -19) * mm, "radius": 1.5 * mm});
            skCircle(sketch, "E44.27.0.51", {"center": v(-159, -19) * mm, "radius": 1.5 * mm});
            skCircle(sketch, "E44.27.0.52", {"center": v(156, -19) * mm, "radius": 1.5 * mm});
            skCircle(sketch, "E44.27.0.53", {"center": v(76, -19) * mm, "radius": 1.5 * mm});
            skCircle(sketch, "E44.27.0.54", {"center": v(-4, -19) * mm, "radius": 1.5 * mm});
            skCircle(sketch, "E44.27.0.55", {"center": v(41, -19) * mm, "radius": 1.5 * mm});
            skCircle(sketch, "E44.27.0.56", {"center": v(-34, -19) * mm, "radius": 1.5 * mm});
            skCircle(sketch, "E44.27.0.57", {"center": v(-114, -19) * mm, "radius": 1.5 * mm});
            skCircle(sketch, "E44.27.0.58", {"center": v(121, -19) * mm, "radius": 1.5 * mm});
            skCircle(sketch, "E44.27.0.59", {"center": v(-74, -19) * mm, "radius": 1.5 * mm});
            skCircle(sketch, "E44.27.0.60", {"center": v(-154, -19) * mm, "radius": 1.5 * mm});
            skCircle(sketch, "E44.27.0.61", {"center": v(161, -19) * mm, "radius": 1.5 * mm});
            skCircle(sketch, "E44.27.0.62", {"center": v(81, -19) * mm, "radius": 1.5 * mm});
            skCircle(sketch, "E44.27.0.63", {"center": v(1, -19) * mm, "radius": 1.5 * mm});
            skCircle(sketch, "E44.27.0.64", {"center": v(46, -19) * mm, "radius": 1.5 * mm});
            skCircle(sketch, "E44.27.0.65", {"center": v(-29, -19) * mm, "radius": 1.5 * mm});
            skCircle(sketch, "E44.27.0.66", {"center": v(-109, -19) * mm, "radius": 1.5 * mm});
            skCircle(sketch, "E44.27.0.67", {"center": v(126, -19) * mm, "radius": 1.5 * mm});
            skLineSegment(sketch, "E44.27.0.68", {"start": v(-174, -19) * mm, "end": v(-169, -19) * mm, "construction": true});
            skCircle(sketch, "E44.27.0.69", {"center": v(-174, -19) * mm, "radius": 1.5 * mm});
            skCircle(sketch, "E44.27.0.70", {"center": v(-169, -19) * mm, "radius": 1.5 * mm});
            skCircle(sketch, "E44.28.0.0", {"center": v(166, -24) * mm, "radius": 1.5 * mm});
            skCircle(sketch, "E44.28.0.1", {"center": v(21, -24) * mm, "radius": 1.5 * mm});
            skCircle(sketch, "E44.28.0.2", {"center": v(-99, -24) * mm, "radius": 1.5 * mm});
            skCircle(sketch, "E44.28.0.3", {"center": v(6, -24) * mm, "radius": 1.5 * mm});
            skCircle(sketch, "E44.28.0.4", {"center": v(-54, -24) * mm, "radius": 1.5 * mm});
            skCircle(sketch, "E44.28.0.5", {"center": v(171, -24) * mm, "radius": 1.5 * mm});
            skCircle(sketch, "E44.28.0.6", {"center": v(-104, -24) * mm, "radius": 1.5 * mm});
            skCircle(sketch, "E44.28.0.7", {"center": v(11, -24) * mm, "radius": 1.5 * mm});
            skCircle(sketch, "E44.28.0.8", {"center": v(56, -24) * mm, "radius": 1.5 * mm});
            skCircle(sketch, "E44.28.0.9", {"center": v(-134, -24) * mm, "radius": 1.5 * mm});
            skCircle(sketch, "E44.28.0.10", {"center": v(51, -24) * mm, "radius": 1.5 * mm});
            skCircle(sketch, "E44.28.0.11", {"center": v(131, -24) * mm, "radius": 1.5 * mm});
            skCircle(sketch, "E44.28.0.12", {"center": v(151, -24) * mm, "radius": 1.5 * mm});
            skCircle(sketch, "E44.28.0.13", {"center": v(-24, -24) * mm, "radius": 1.5 * mm});
            skCircle(sketch, "E44.28.0.14", {"center": v(-64, -24) * mm, "radius": 1.5 * mm});
            skCircle(sketch, "E44.28.0.15", {"center": v(-9, -24) * mm, "radius": 1.5 * mm});
            skCircle(sketch, "E44.28.0.16", {"center": v(136, -24) * mm, "radius": 1.5 * mm});
            skCircle(sketch, "E44.28.0.17", {"center": v(91, -24) * mm, "radius": 1.5 * mm});
            skCircle(sketch, "E44.28.0.18", {"center": v(101, -24) * mm, "radius": 1.5 * mm});
            skCircle(sketch, "E44.28.0.19", {"center": v(-144, -24) * mm, "radius": 1.5 * mm});
            skCircle(sketch, "E44.28.0.20", {"center": v(71, -24) * mm, "radius": 1.5 * mm});
            skCircle(sketch, "E44.28.0.21", {"center": v(-69, -24) * mm, "radius": 1.5 * mm});
            skCircle(sketch, "E44.28.0.22", {"center": v(-84, -24) * mm, "radius": 1.5 * mm});
            skCircle(sketch, "E44.28.0.23", {"center": v(116, -24) * mm, "radius": 1.5 * mm});
            skCircle(sketch, "E44.28.0.24", {"center": v(-164, -24) * mm, "radius": 1.5 * mm});
            skCircle(sketch, "E44.28.0.25", {"center": v(86, -24) * mm, "radius": 1.5 * mm});
            skCircle(sketch, "E44.28.0.26", {"center": v(-149, -24) * mm, "radius": 1.5 * mm});
            skCircle(sketch, "E44.28.0.27", {"center": v(106, -24) * mm, "radius": 1.5 * mm});
            skCircle(sketch, "E44.28.0.28", {"center": v(-94, -24) * mm, "radius": 1.5 * mm});
            skCircle(sketch, "E44.28.0.29", {"center": v(-129, -24) * mm, "radius": 1.5 * mm});
            skCircle(sketch, "E44.28.0.30", {"center": v(-19, -24) * mm, "radius": 1.5 * mm});
            skCircle(sketch, "E44.28.0.31", {"center": v(-49, -24) * mm, "radius": 1.5 * mm});
            skCircle(sketch, "E44.28.0.32", {"center": v(26, -24) * mm, "radius": 1.5 * mm});
            skCircle(sketch, "E44.28.0.33", {"center": v(61, -24) * mm, "radius": 1.5 * mm});
            skCircle(sketch, "E44.28.0.34", {"center": v(16, -24) * mm, "radius": 1.5 * mm});
            skCircle(sketch, "E44.28.0.35", {"center": v(96, -24) * mm, "radius": 1.5 * mm});
            skCircle(sketch, "E44.28.0.36", {"center": v(-139, -24) * mm, "radius": 1.5 * mm});
            skCircle(sketch, "E44.28.0.37", {"center": v(-59, -24) * mm, "radius": 1.5 * mm});
            skCircle(sketch, "E44.28.0.38", {"center": v(111, -24) * mm, "radius": 1.5 * mm});
            skCircle(sketch, "E44.28.0.39", {"center": v(146, -24) * mm, "radius": 1.5 * mm});
            skCircle(sketch, "E44.28.0.40", {"center": v(-89, -24) * mm, "radius": 1.5 * mm});
            skCircle(sketch, "E44.28.0.41", {"center": v(-44, -24) * mm, "radius": 1.5 * mm});
            skCircle(sketch, "E44.28.0.42", {"center": v(-124, -24) * mm, "radius": 1.5 * mm});
            skCircle(sketch, "E44.28.0.43", {"center": v(-14, -24) * mm, "radius": 1.5 * mm});
            skCircle(sketch, "E44.28.0.44", {"center": v(31, -24) * mm, "radius": 1.5 * mm});
            skCircle(sketch, "E44.28.0.45", {"center": v(66, -24) * mm, "radius": 1.5 * mm});
            skCircle(sketch, "E44.28.0.46", {"center": v(141, -24) * mm, "radius": 1.5 * mm});
            skCircle(sketch, "E44.28.0.47", {"center": v(36, -24) * mm, "radius": 1.5 * mm});
            skCircle(sketch, "E44.28.0.48", {"center": v(-39, -24) * mm, "radius": 1.5 * mm});
            skCircle(sketch, "E44.28.0.49", {"center": v(-119, -24) * mm, "radius": 1.5 * mm});
            skCircle(sketch, "E44.28.0.50", {"center": v(-79, -24) * mm, "radius": 1.5 * mm});
            skCircle(sketch, "E44.28.0.51", {"center": v(-159, -24) * mm, "radius": 1.5 * mm});
            skCircle(sketch, "E44.28.0.52", {"center": v(156, -24) * mm, "radius": 1.5 * mm});
            skCircle(sketch, "E44.28.0.53", {"center": v(76, -24) * mm, "radius": 1.5 * mm});
            skCircle(sketch, "E44.28.0.54", {"center": v(-4, -24) * mm, "radius": 1.5 * mm});
            skCircle(sketch, "E44.28.0.55", {"center": v(41, -24) * mm, "radius": 1.5 * mm});
            skCircle(sketch, "E44.28.0.56", {"center": v(-34, -24) * mm, "radius": 1.5 * mm});
            skCircle(sketch, "E44.28.0.57", {"center": v(-114, -24) * mm, "radius": 1.5 * mm});
            skCircle(sketch, "E44.28.0.58", {"center": v(121, -24) * mm, "radius": 1.5 * mm});
            skCircle(sketch, "E44.28.0.59", {"center": v(-74, -24) * mm, "radius": 1.5 * mm});
            skCircle(sketch, "E44.28.0.60", {"center": v(-154, -24) * mm, "radius": 1.5 * mm});
            skCircle(sketch, "E44.28.0.61", {"center": v(161, -24) * mm, "radius": 1.5 * mm});
            skCircle(sketch, "E44.28.0.62", {"center": v(81, -24) * mm, "radius": 1.5 * mm});
            skCircle(sketch, "E44.28.0.63", {"center": v(1, -24) * mm, "radius": 1.5 * mm});
            skCircle(sketch, "E44.28.0.64", {"center": v(46, -24) * mm, "radius": 1.5 * mm});
            skCircle(sketch, "E44.28.0.65", {"center": v(-29, -24) * mm, "radius": 1.5 * mm});
            skCircle(sketch, "E44.28.0.66", {"center": v(-109, -24) * mm, "radius": 1.5 * mm});
            skCircle(sketch, "E44.28.0.67", {"center": v(126, -24) * mm, "radius": 1.5 * mm});
            skLineSegment(sketch, "E44.28.0.68", {"start": v(-174, -24) * mm, "end": v(-169, -24) * mm, "construction": true});
            skCircle(sketch, "E44.28.0.69", {"center": v(-174, -24) * mm, "radius": 1.5 * mm});
            skCircle(sketch, "E44.28.0.70", {"center": v(-169, -24) * mm, "radius": 1.5 * mm});
            skCircle(sketch, "E44.29.0.0", {"center": v(166, -29) * mm, "radius": 1.5 * mm});
            skCircle(sketch, "E44.29.0.1", {"center": v(21, -29) * mm, "radius": 1.5 * mm});
            skCircle(sketch, "E44.29.0.2", {"center": v(-99, -29) * mm, "radius": 1.5 * mm});
            skCircle(sketch, "E44.29.0.3", {"center": v(6, -29) * mm, "radius": 1.5 * mm});
            skCircle(sketch, "E44.29.0.4", {"center": v(-54, -29) * mm, "radius": 1.5 * mm});
            skCircle(sketch, "E44.29.0.5", {"center": v(171, -29) * mm, "radius": 1.5 * mm});
            skCircle(sketch, "E44.29.0.6", {"center": v(-104, -29) * mm, "radius": 1.5 * mm});
            skCircle(sketch, "E44.29.0.7", {"center": v(11, -29) * mm, "radius": 1.5 * mm});
            skCircle(sketch, "E44.29.0.8", {"center": v(56, -29) * mm, "radius": 1.5 * mm});
            skCircle(sketch, "E44.29.0.9", {"center": v(-134, -29) * mm, "radius": 1.5 * mm});
            skCircle(sketch, "E44.29.0.10", {"center": v(51, -29) * mm, "radius": 1.5 * mm});
            skCircle(sketch, "E44.29.0.11", {"center": v(131, -29) * mm, "radius": 1.5 * mm});
            skCircle(sketch, "E44.29.0.12", {"center": v(151, -29) * mm, "radius": 1.5 * mm});
            skCircle(sketch, "E44.29.0.13", {"center": v(-24, -29) * mm, "radius": 1.5 * mm});
            skCircle(sketch, "E44.29.0.14", {"center": v(-64, -29) * mm, "radius": 1.5 * mm});
            skCircle(sketch, "E44.29.0.15", {"center": v(-9, -29) * mm, "radius": 1.5 * mm});
            skCircle(sketch, "E44.29.0.16", {"center": v(136, -29) * mm, "radius": 1.5 * mm});
            skCircle(sketch, "E44.29.0.17", {"center": v(91, -29) * mm, "radius": 1.5 * mm});
            skCircle(sketch, "E44.29.0.18", {"center": v(101, -29) * mm, "radius": 1.5 * mm});
            skCircle(sketch, "E44.29.0.19", {"center": v(-144, -29) * mm, "radius": 1.5 * mm});
            skCircle(sketch, "E44.29.0.20", {"center": v(71, -29) * mm, "radius": 1.5 * mm});
            skCircle(sketch, "E44.29.0.21", {"center": v(-69, -29) * mm, "radius": 1.5 * mm});
            skCircle(sketch, "E44.29.0.22", {"center": v(-84, -29) * mm, "radius": 1.5 * mm});
            skCircle(sketch, "E44.29.0.23", {"center": v(116, -29) * mm, "radius": 1.5 * mm});
            skCircle(sketch, "E44.29.0.24", {"center": v(-164, -29) * mm, "radius": 1.5 * mm});
            skCircle(sketch, "E44.29.0.25", {"center": v(86, -29) * mm, "radius": 1.5 * mm});
            skCircle(sketch, "E44.29.0.26", {"center": v(-149, -29) * mm, "radius": 1.5 * mm});
            skCircle(sketch, "E44.29.0.27", {"center": v(106, -29) * mm, "radius": 1.5 * mm});
            skCircle(sketch, "E44.29.0.28", {"center": v(-94, -29) * mm, "radius": 1.5 * mm});
            skCircle(sketch, "E44.29.0.29", {"center": v(-129, -29) * mm, "radius": 1.5 * mm});
            skCircle(sketch, "E44.29.0.30", {"center": v(-19, -29) * mm, "radius": 1.5 * mm});
            skCircle(sketch, "E44.29.0.31", {"center": v(-49, -29) * mm, "radius": 1.5 * mm});
            skCircle(sketch, "E44.29.0.32", {"center": v(26, -29) * mm, "radius": 1.5 * mm});
            skCircle(sketch, "E44.29.0.33", {"center": v(61, -29) * mm, "radius": 1.5 * mm});
            skCircle(sketch, "E44.29.0.34", {"center": v(16, -29) * mm, "radius": 1.5 * mm});
            skCircle(sketch, "E44.29.0.35", {"center": v(96, -29) * mm, "radius": 1.5 * mm});
            skCircle(sketch, "E44.29.0.36", {"center": v(-139, -29) * mm, "radius": 1.5 * mm});
            skCircle(sketch, "E44.29.0.37", {"center": v(-59, -29) * mm, "radius": 1.5 * mm});
            skCircle(sketch, "E44.29.0.38", {"center": v(111, -29) * mm, "radius": 1.5 * mm});
            skCircle(sketch, "E44.29.0.39", {"center": v(146, -29) * mm, "radius": 1.5 * mm});
            skCircle(sketch, "E44.29.0.40", {"center": v(-89, -29) * mm, "radius": 1.5 * mm});
            skCircle(sketch, "E44.29.0.41", {"center": v(-44, -29) * mm, "radius": 1.5 * mm});
            skCircle(sketch, "E44.29.0.42", {"center": v(-124, -29) * mm, "radius": 1.5 * mm});
            skCircle(sketch, "E44.29.0.43", {"center": v(-14, -29) * mm, "radius": 1.5 * mm});
            skCircle(sketch, "E44.29.0.44", {"center": v(31, -29) * mm, "radius": 1.5 * mm});
            skCircle(sketch, "E44.29.0.45", {"center": v(66, -29) * mm, "radius": 1.5 * mm});
            skCircle(sketch, "E44.29.0.46", {"center": v(141, -29) * mm, "radius": 1.5 * mm});
            skCircle(sketch, "E44.29.0.47", {"center": v(36, -29) * mm, "radius": 1.5 * mm});
            skCircle(sketch, "E44.29.0.48", {"center": v(-39, -29) * mm, "radius": 1.5 * mm});
            skCircle(sketch, "E44.29.0.49", {"center": v(-119, -29) * mm, "radius": 1.5 * mm});
            skCircle(sketch, "E44.29.0.50", {"center": v(-79, -29) * mm, "radius": 1.5 * mm});
            skCircle(sketch, "E44.29.0.51", {"center": v(-159, -29) * mm, "radius": 1.5 * mm});
            skCircle(sketch, "E44.29.0.52", {"center": v(156, -29) * mm, "radius": 1.5 * mm});
            skCircle(sketch, "E44.29.0.53", {"center": v(76, -29) * mm, "radius": 1.5 * mm});
            skCircle(sketch, "E44.29.0.54", {"center": v(-4, -29) * mm, "radius": 1.5 * mm});
            skCircle(sketch, "E44.29.0.55", {"center": v(41, -29) * mm, "radius": 1.5 * mm});
            skCircle(sketch, "E44.29.0.56", {"center": v(-34, -29) * mm, "radius": 1.5 * mm});
            skCircle(sketch, "E44.29.0.57", {"center": v(-114, -29) * mm, "radius": 1.5 * mm});
            skCircle(sketch, "E44.29.0.58", {"center": v(121, -29) * mm, "radius": 1.5 * mm});
            skCircle(sketch, "E44.29.0.59", {"center": v(-74, -29) * mm, "radius": 1.5 * mm});
            skCircle(sketch, "E44.29.0.60", {"center": v(-154, -29) * mm, "radius": 1.5 * mm});
            skCircle(sketch, "E44.29.0.61", {"center": v(161, -29) * mm, "radius": 1.5 * mm});
            skCircle(sketch, "E44.29.0.62", {"center": v(81, -29) * mm, "radius": 1.5 * mm});
            skCircle(sketch, "E44.29.0.63", {"center": v(1, -29) * mm, "radius": 1.5 * mm});
            skCircle(sketch, "E44.29.0.64", {"center": v(46, -29) * mm, "radius": 1.5 * mm});
            skCircle(sketch, "E44.29.0.65", {"center": v(-29, -29) * mm, "radius": 1.5 * mm});
            skCircle(sketch, "E44.29.0.66", {"center": v(-109, -29) * mm, "radius": 1.5 * mm});
            skCircle(sketch, "E44.29.0.67", {"center": v(126, -29) * mm, "radius": 1.5 * mm});
            skLineSegment(sketch, "E44.29.0.68", {"start": v(-174, -29) * mm, "end": v(-169, -29) * mm, "construction": true});
            skCircle(sketch, "E44.29.0.69", {"center": v(-174, -29) * mm, "radius": 1.5 * mm});
            skCircle(sketch, "E44.29.0.70", {"center": v(-169, -29) * mm, "radius": 1.5 * mm});
            skLineSegment(sketch, "E44.direction1", {"start": v(-174, 116) * mm, "end": v(-174, 111) * mm, "construction": true});
            skCircle(sketch, "E45.0.30.0", {"center": v(166, -34) * mm, "radius": 1.5 * mm});
            skCircle(sketch, "E45.2.30.0", {"center": v(21, -34) * mm, "radius": 1.5 * mm});
            skCircle(sketch, "E45.4.30.0", {"center": v(-99, -34) * mm, "radius": 1.5 * mm});
            skCircle(sketch, "E45.6.30.0", {"center": v(6, -34) * mm, "radius": 1.5 * mm});
            skCircle(sketch, "E45.8.30.0", {"center": v(-54, -34) * mm, "radius": 1.5 * mm});
            skCircle(sketch, "E45.10.30.0", {"center": v(171, -34) * mm, "radius": 1.5 * mm});
            skCircle(sketch, "E45.12.30.0", {"center": v(-104, -34) * mm, "radius": 1.5 * mm});
            skCircle(sketch, "E45.14.30.0", {"center": v(11, -34) * mm, "radius": 1.5 * mm});
            skCircle(sketch, "E45.16.30.0", {"center": v(56, -34) * mm, "radius": 1.5 * mm});
            skCircle(sketch, "E45.18.30.0", {"center": v(-134, -34) * mm, "radius": 1.5 * mm});
            skCircle(sketch, "E45.20.30.0", {"center": v(51, -34) * mm, "radius": 1.5 * mm});
            skCircle(sketch, "E45.22.30.0", {"center": v(131, -34) * mm, "radius": 1.5 * mm});
            skCircle(sketch, "E45.24.30.0", {"center": v(151, -34) * mm, "radius": 1.5 * mm});
            skCircle(sketch, "E45.26.30.0", {"center": v(-24, -34) * mm, "radius": 1.5 * mm});
            skCircle(sketch, "E45.28.30.0", {"center": v(-64, -34) * mm, "radius": 1.5 * mm});
            skCircle(sketch, "E45.30.30.0", {"center": v(-9, -34) * mm, "radius": 1.5 * mm});
            skCircle(sketch, "E45.32.30.0", {"center": v(136, -34) * mm, "radius": 1.5 * mm});
            skCircle(sketch, "E45.34.30.0", {"center": v(91, -34) * mm, "radius": 1.5 * mm});
            skCircle(sketch, "E45.36.30.0", {"center": v(101, -34) * mm, "radius": 1.5 * mm});
            skCircle(sketch, "E45.38.30.0", {"center": v(-144, -34) * mm, "radius": 1.5 * mm});
            skCircle(sketch, "E45.40.30.0", {"center": v(71, -34) * mm, "radius": 1.5 * mm});
            skCircle(sketch, "E45.42.30.0", {"center": v(-69, -34) * mm, "radius": 1.5 * mm});
            skCircle(sketch, "E45.44.30.0", {"center": v(-84, -34) * mm, "radius": 1.5 * mm});
            skCircle(sketch, "E45.46.30.0", {"center": v(116, -34) * mm, "radius": 1.5 * mm});
            skCircle(sketch, "E45.48.30.0", {"center": v(-164, -34) * mm, "radius": 1.5 * mm});
            skCircle(sketch, "E45.50.30.0", {"center": v(86, -34) * mm, "radius": 1.5 * mm});
            skCircle(sketch, "E45.52.30.0", {"center": v(-149, -34) * mm, "radius": 1.5 * mm});
            skCircle(sketch, "E45.54.30.0", {"center": v(106, -34) * mm, "radius": 1.5 * mm});
            skCircle(sketch, "E45.56.30.0", {"center": v(-94, -34) * mm, "radius": 1.5 * mm});
            skCircle(sketch, "E45.58.30.0", {"center": v(-129, -34) * mm, "radius": 1.5 * mm});
            skCircle(sketch, "E45.60.30.0", {"center": v(-19, -34) * mm, "radius": 1.5 * mm});
            skCircle(sketch, "E45.62.30.0", {"center": v(-49, -34) * mm, "radius": 1.5 * mm});
            skCircle(sketch, "E45.64.30.0", {"center": v(26, -34) * mm, "radius": 1.5 * mm});
            skCircle(sketch, "E45.66.30.0", {"center": v(61, -34) * mm, "radius": 1.5 * mm});
            skCircle(sketch, "E45.68.30.0", {"center": v(16, -34) * mm, "radius": 1.5 * mm});
            skCircle(sketch, "E45.70.30.0", {"center": v(96, -34) * mm, "radius": 1.5 * mm});
            skCircle(sketch, "E45.72.30.0", {"center": v(-139, -34) * mm, "radius": 1.5 * mm});
            skCircle(sketch, "E45.74.30.0", {"center": v(-59, -34) * mm, "radius": 1.5 * mm});
            skCircle(sketch, "E45.76.30.0", {"center": v(111, -34) * mm, "radius": 1.5 * mm});
            skCircle(sketch, "E45.78.30.0", {"center": v(146, -34) * mm, "radius": 1.5 * mm});
            skCircle(sketch, "E45.80.30.0", {"center": v(-89, -34) * mm, "radius": 1.5 * mm});
            skCircle(sketch, "E45.82.30.0", {"center": v(-44, -34) * mm, "radius": 1.5 * mm});
            skCircle(sketch, "E45.84.30.0", {"center": v(-124, -34) * mm, "radius": 1.5 * mm});
            skCircle(sketch, "E45.86.30.0", {"center": v(-14, -34) * mm, "radius": 1.5 * mm});
            skCircle(sketch, "E45.88.30.0", {"center": v(31, -34) * mm, "radius": 1.5 * mm});
            skCircle(sketch, "E45.90.30.0", {"center": v(66, -34) * mm, "radius": 1.5 * mm});
            skCircle(sketch, "E45.92.30.0", {"center": v(141, -34) * mm, "radius": 1.5 * mm});
            skCircle(sketch, "E45.94.30.0", {"center": v(36, -34) * mm, "radius": 1.5 * mm});
            skCircle(sketch, "E45.96.30.0", {"center": v(-39, -34) * mm, "radius": 1.5 * mm});
            skCircle(sketch, "E45.98.30.0", {"center": v(-119, -34) * mm, "radius": 1.5 * mm});
            skCircle(sketch, "E45.100.30.0", {"center": v(-79, -34) * mm, "radius": 1.5 * mm});
            skCircle(sketch, "E45.102.30.0", {"center": v(-159, -34) * mm, "radius": 1.5 * mm});
            skCircle(sketch, "E45.104.30.0", {"center": v(156, -34) * mm, "radius": 1.5 * mm});
            skCircle(sketch, "E45.106.30.0", {"center": v(76, -34) * mm, "radius": 1.5 * mm});
            skCircle(sketch, "E45.108.30.0", {"center": v(-4, -34) * mm, "radius": 1.5 * mm});
            skCircle(sketch, "E45.110.30.0", {"center": v(41, -34) * mm, "radius": 1.5 * mm});
            skCircle(sketch, "E45.112.30.0", {"center": v(-34, -34) * mm, "radius": 1.5 * mm});
            skCircle(sketch, "E45.114.30.0", {"center": v(-114, -34) * mm, "radius": 1.5 * mm});
            skCircle(sketch, "E45.116.30.0", {"center": v(121, -34) * mm, "radius": 1.5 * mm});
            skCircle(sketch, "E45.118.30.0", {"center": v(-74, -34) * mm, "radius": 1.5 * mm});
            skCircle(sketch, "E45.120.30.0", {"center": v(-154, -34) * mm, "radius": 1.5 * mm});
            skCircle(sketch, "E45.122.30.0", {"center": v(161, -34) * mm, "radius": 1.5 * mm});
            skCircle(sketch, "E45.124.30.0", {"center": v(81, -34) * mm, "radius": 1.5 * mm});
            skCircle(sketch, "E45.126.30.0", {"center": v(1, -34) * mm, "radius": 1.5 * mm});
            skCircle(sketch, "E45.128.30.0", {"center": v(46, -34) * mm, "radius": 1.5 * mm});
            skCircle(sketch, "E45.130.30.0", {"center": v(-29, -34) * mm, "radius": 1.5 * mm});
            skCircle(sketch, "E45.132.30.0", {"center": v(-109, -34) * mm, "radius": 1.5 * mm});
            skCircle(sketch, "E45.134.30.0", {"center": v(126, -34) * mm, "radius": 1.5 * mm});
            skLineSegment(sketch, "E45.136.30.0", {"start": v(-174, -34) * mm, "end": v(-169, -34) * mm, "construction": true});
            skCircle(sketch, "E45.139.30.0", {"center": v(-174, -34) * mm, "radius": 1.5 * mm});
            skCircle(sketch, "E45.141.30.0", {"center": v(-169, -34) * mm, "radius": 1.5 * mm});
            skCircle(sketch, "E45.0.31.0", {"center": v(166, -39) * mm, "radius": 1.5 * mm});
            skCircle(sketch, "E45.2.31.0", {"center": v(21, -39) * mm, "radius": 1.5 * mm});
            skCircle(sketch, "E45.4.31.0", {"center": v(-99, -39) * mm, "radius": 1.5 * mm});
            skCircle(sketch, "E45.6.31.0", {"center": v(6, -39) * mm, "radius": 1.5 * mm});
            skCircle(sketch, "E45.8.31.0", {"center": v(-54, -39) * mm, "radius": 1.5 * mm});
            skCircle(sketch, "E45.10.31.0", {"center": v(171, -39) * mm, "radius": 1.5 * mm});
            skCircle(sketch, "E45.12.31.0", {"center": v(-104, -39) * mm, "radius": 1.5 * mm});
            skCircle(sketch, "E45.14.31.0", {"center": v(11, -39) * mm, "radius": 1.5 * mm});
            skCircle(sketch, "E45.16.31.0", {"center": v(56, -39) * mm, "radius": 1.5 * mm});
            skCircle(sketch, "E45.18.31.0", {"center": v(-134, -39) * mm, "radius": 1.5 * mm});
            skCircle(sketch, "E45.20.31.0", {"center": v(51, -39) * mm, "radius": 1.5 * mm});
            skCircle(sketch, "E45.22.31.0", {"center": v(131, -39) * mm, "radius": 1.5 * mm});
            skCircle(sketch, "E45.24.31.0", {"center": v(151, -39) * mm, "radius": 1.5 * mm});
            skCircle(sketch, "E45.26.31.0", {"center": v(-24, -39) * mm, "radius": 1.5 * mm});
            skCircle(sketch, "E45.28.31.0", {"center": v(-64, -39) * mm, "radius": 1.5 * mm});
            skCircle(sketch, "E45.30.31.0", {"center": v(-9, -39) * mm, "radius": 1.5 * mm});
            skCircle(sketch, "E45.32.31.0", {"center": v(136, -39) * mm, "radius": 1.5 * mm});
            skCircle(sketch, "E45.34.31.0", {"center": v(91, -39) * mm, "radius": 1.5 * mm});
            skCircle(sketch, "E45.36.31.0", {"center": v(101, -39) * mm, "radius": 1.5 * mm});
            skCircle(sketch, "E45.38.31.0", {"center": v(-144, -39) * mm, "radius": 1.5 * mm});
            skCircle(sketch, "E45.40.31.0", {"center": v(71, -39) * mm, "radius": 1.5 * mm});
            skCircle(sketch, "E45.42.31.0", {"center": v(-69, -39) * mm, "radius": 1.5 * mm});
            skCircle(sketch, "E45.44.31.0", {"center": v(-84, -39) * mm, "radius": 1.5 * mm});
            skCircle(sketch, "E45.46.31.0", {"center": v(116, -39) * mm, "radius": 1.5 * mm});
            skCircle(sketch, "E45.48.31.0", {"center": v(-164, -39) * mm, "radius": 1.5 * mm});
            skCircle(sketch, "E45.50.31.0", {"center": v(86, -39) * mm, "radius": 1.5 * mm});
            skCircle(sketch, "E45.52.31.0", {"center": v(-149, -39) * mm, "radius": 1.5 * mm});
            skCircle(sketch, "E45.54.31.0", {"center": v(106, -39) * mm, "radius": 1.5 * mm});
            skCircle(sketch, "E45.56.31.0", {"center": v(-94, -39) * mm, "radius": 1.5 * mm});
            skCircle(sketch, "E45.58.31.0", {"center": v(-129, -39) * mm, "radius": 1.5 * mm});
            skCircle(sketch, "E45.60.31.0", {"center": v(-19, -39) * mm, "radius": 1.5 * mm});
            skCircle(sketch, "E45.62.31.0", {"center": v(-49, -39) * mm, "radius": 1.5 * mm});
            skCircle(sketch, "E45.64.31.0", {"center": v(26, -39) * mm, "radius": 1.5 * mm});
            skCircle(sketch, "E45.66.31.0", {"center": v(61, -39) * mm, "radius": 1.5 * mm});
            skCircle(sketch, "E45.68.31.0", {"center": v(16, -39) * mm, "radius": 1.5 * mm});
            skCircle(sketch, "E45.70.31.0", {"center": v(96, -39) * mm, "radius": 1.5 * mm});
            skCircle(sketch, "E45.72.31.0", {"center": v(-139, -39) * mm, "radius": 1.5 * mm});
            skCircle(sketch, "E45.74.31.0", {"center": v(-59, -39) * mm, "radius": 1.5 * mm});
            skCircle(sketch, "E45.76.31.0", {"center": v(111, -39) * mm, "radius": 1.5 * mm});
            skCircle(sketch, "E45.78.31.0", {"center": v(146, -39) * mm, "radius": 1.5 * mm});
            skCircle(sketch, "E45.80.31.0", {"center": v(-89, -39) * mm, "radius": 1.5 * mm});
            skCircle(sketch, "E45.82.31.0", {"center": v(-44, -39) * mm, "radius": 1.5 * mm});
            skCircle(sketch, "E45.84.31.0", {"center": v(-124, -39) * mm, "radius": 1.5 * mm});
            skCircle(sketch, "E45.86.31.0", {"center": v(-14, -39) * mm, "radius": 1.5 * mm});
            skCircle(sketch, "E45.88.31.0", {"center": v(31, -39) * mm, "radius": 1.5 * mm});
            skCircle(sketch, "E45.90.31.0", {"center": v(66, -39) * mm, "radius": 1.5 * mm});
            skCircle(sketch, "E45.92.31.0", {"center": v(141, -39) * mm, "radius": 1.5 * mm});
            skCircle(sketch, "E45.94.31.0", {"center": v(36, -39) * mm, "radius": 1.5 * mm});
            skCircle(sketch, "E45.96.31.0", {"center": v(-39, -39) * mm, "radius": 1.5 * mm});
            skCircle(sketch, "E45.98.31.0", {"center": v(-119, -39) * mm, "radius": 1.5 * mm});
            skCircle(sketch, "E45.100.31.0", {"center": v(-79, -39) * mm, "radius": 1.5 * mm});
            skCircle(sketch, "E45.102.31.0", {"center": v(-159, -39) * mm, "radius": 1.5 * mm});
            skCircle(sketch, "E45.104.31.0", {"center": v(156, -39) * mm, "radius": 1.5 * mm});
            skCircle(sketch, "E45.106.31.0", {"center": v(76, -39) * mm, "radius": 1.5 * mm});
            skCircle(sketch, "E45.108.31.0", {"center": v(-4, -39) * mm, "radius": 1.5 * mm});
            skCircle(sketch, "E45.110.31.0", {"center": v(41, -39) * mm, "radius": 1.5 * mm});
            skCircle(sketch, "E45.112.31.0", {"center": v(-34, -39) * mm, "radius": 1.5 * mm});
            skCircle(sketch, "E45.114.31.0", {"center": v(-114, -39) * mm, "radius": 1.5 * mm});
            skCircle(sketch, "E45.116.31.0", {"center": v(121, -39) * mm, "radius": 1.5 * mm});
            skCircle(sketch, "E45.118.31.0", {"center": v(-74, -39) * mm, "radius": 1.5 * mm});
            skCircle(sketch, "E45.120.31.0", {"center": v(-154, -39) * mm, "radius": 1.5 * mm});
            skCircle(sketch, "E45.122.31.0", {"center": v(161, -39) * mm, "radius": 1.5 * mm});
            skCircle(sketch, "E45.124.31.0", {"center": v(81, -39) * mm, "radius": 1.5 * mm});
            skCircle(sketch, "E45.126.31.0", {"center": v(1, -39) * mm, "radius": 1.5 * mm});
            skCircle(sketch, "E45.128.31.0", {"center": v(46, -39) * mm, "radius": 1.5 * mm});
            skCircle(sketch, "E45.130.31.0", {"center": v(-29, -39) * mm, "radius": 1.5 * mm});
            skCircle(sketch, "E45.132.31.0", {"center": v(-109, -39) * mm, "radius": 1.5 * mm});
            skCircle(sketch, "E45.134.31.0", {"center": v(126, -39) * mm, "radius": 1.5 * mm});
            skLineSegment(sketch, "E45.136.31.0", {"start": v(-174, -39) * mm, "end": v(-169, -39) * mm, "construction": true});
            skCircle(sketch, "E45.139.31.0", {"center": v(-174, -39) * mm, "radius": 1.5 * mm});
            skCircle(sketch, "E45.141.31.0", {"center": v(-169, -39) * mm, "radius": 1.5 * mm});
            skCircle(sketch, "E45.0.32.0", {"center": v(166, -44) * mm, "radius": 1.5 * mm});
            skCircle(sketch, "E45.2.32.0", {"center": v(21, -44) * mm, "radius": 1.5 * mm});
            skCircle(sketch, "E45.4.32.0", {"center": v(-99, -44) * mm, "radius": 1.5 * mm});
            skCircle(sketch, "E45.6.32.0", {"center": v(6, -44) * mm, "radius": 1.5 * mm});
            skCircle(sketch, "E45.8.32.0", {"center": v(-54, -44) * mm, "radius": 1.5 * mm});
            skCircle(sketch, "E45.10.32.0", {"center": v(171, -44) * mm, "radius": 1.5 * mm});
            skCircle(sketch, "E45.12.32.0", {"center": v(-104, -44) * mm, "radius": 1.5 * mm});
            skCircle(sketch, "E45.14.32.0", {"center": v(11, -44) * mm, "radius": 1.5 * mm});
            skCircle(sketch, "E45.16.32.0", {"center": v(56, -44) * mm, "radius": 1.5 * mm});
            skCircle(sketch, "E45.18.32.0", {"center": v(-134, -44) * mm, "radius": 1.5 * mm});
            skCircle(sketch, "E45.20.32.0", {"center": v(51, -44) * mm, "radius": 1.5 * mm});
            skCircle(sketch, "E45.22.32.0", {"center": v(131, -44) * mm, "radius": 1.5 * mm});
            skCircle(sketch, "E45.24.32.0", {"center": v(151, -44) * mm, "radius": 1.5 * mm});
            skCircle(sketch, "E45.26.32.0", {"center": v(-24, -44) * mm, "radius": 1.5 * mm});
            skCircle(sketch, "E45.28.32.0", {"center": v(-64, -44) * mm, "radius": 1.5 * mm});
            skCircle(sketch, "E45.30.32.0", {"center": v(-9, -44) * mm, "radius": 1.5 * mm});
            skCircle(sketch, "E45.32.32.0", {"center": v(136, -44) * mm, "radius": 1.5 * mm});
            skCircle(sketch, "E45.34.32.0", {"center": v(91, -44) * mm, "radius": 1.5 * mm});
            skCircle(sketch, "E45.36.32.0", {"center": v(101, -44) * mm, "radius": 1.5 * mm});
            skCircle(sketch, "E45.38.32.0", {"center": v(-144, -44) * mm, "radius": 1.5 * mm});
            skCircle(sketch, "E45.40.32.0", {"center": v(71, -44) * mm, "radius": 1.5 * mm});
            skCircle(sketch, "E45.42.32.0", {"center": v(-69, -44) * mm, "radius": 1.5 * mm});
            skCircle(sketch, "E45.44.32.0", {"center": v(-84, -44) * mm, "radius": 1.5 * mm});
            skCircle(sketch, "E45.46.32.0", {"center": v(116, -44) * mm, "radius": 1.5 * mm});
            skCircle(sketch, "E45.48.32.0", {"center": v(-164, -44) * mm, "radius": 1.5 * mm});
            skCircle(sketch, "E45.50.32.0", {"center": v(86, -44) * mm, "radius": 1.5 * mm});
            skCircle(sketch, "E45.52.32.0", {"center": v(-149, -44) * mm, "radius": 1.5 * mm});
            skCircle(sketch, "E45.54.32.0", {"center": v(106, -44) * mm, "radius": 1.5 * mm});
            skCircle(sketch, "E45.56.32.0", {"center": v(-94, -44) * mm, "radius": 1.5 * mm});
            skCircle(sketch, "E45.58.32.0", {"center": v(-129, -44) * mm, "radius": 1.5 * mm});
            skCircle(sketch, "E45.60.32.0", {"center": v(-19, -44) * mm, "radius": 1.5 * mm});
            skCircle(sketch, "E45.62.32.0", {"center": v(-49, -44) * mm, "radius": 1.5 * mm});
            skCircle(sketch, "E45.64.32.0", {"center": v(26, -44) * mm, "radius": 1.5 * mm});
            skCircle(sketch, "E45.66.32.0", {"center": v(61, -44) * mm, "radius": 1.5 * mm});
            skCircle(sketch, "E45.68.32.0", {"center": v(16, -44) * mm, "radius": 1.5 * mm});
            skCircle(sketch, "E45.70.32.0", {"center": v(96, -44) * mm, "radius": 1.5 * mm});
            skCircle(sketch, "E45.72.32.0", {"center": v(-139, -44) * mm, "radius": 1.5 * mm});
            skCircle(sketch, "E45.74.32.0", {"center": v(-59, -44) * mm, "radius": 1.5 * mm});
            skCircle(sketch, "E45.76.32.0", {"center": v(111, -44) * mm, "radius": 1.5 * mm});
            skCircle(sketch, "E45.78.32.0", {"center": v(146, -44) * mm, "radius": 1.5 * mm});
            skCircle(sketch, "E45.80.32.0", {"center": v(-89, -44) * mm, "radius": 1.5 * mm});
            skCircle(sketch, "E45.82.32.0", {"center": v(-44, -44) * mm, "radius": 1.5 * mm});
            skCircle(sketch, "E45.84.32.0", {"center": v(-124, -44) * mm, "radius": 1.5 * mm});
            skCircle(sketch, "E45.86.32.0", {"center": v(-14, -44) * mm, "radius": 1.5 * mm});
            skCircle(sketch, "E45.88.32.0", {"center": v(31, -44) * mm, "radius": 1.5 * mm});
            skCircle(sketch, "E45.90.32.0", {"center": v(66, -44) * mm, "radius": 1.5 * mm});
            skCircle(sketch, "E45.92.32.0", {"center": v(141, -44) * mm, "radius": 1.5 * mm});
            skCircle(sketch, "E45.94.32.0", {"center": v(36, -44) * mm, "radius": 1.5 * mm});
            skCircle(sketch, "E45.96.32.0", {"center": v(-39, -44) * mm, "radius": 1.5 * mm});
            skCircle(sketch, "E45.98.32.0", {"center": v(-119, -44) * mm, "radius": 1.5 * mm});
            skCircle(sketch, "E45.100.32.0", {"center": v(-79, -44) * mm, "radius": 1.5 * mm});
            skCircle(sketch, "E45.102.32.0", {"center": v(-159, -44) * mm, "radius": 1.5 * mm});
            skCircle(sketch, "E45.104.32.0", {"center": v(156, -44) * mm, "radius": 1.5 * mm});
            skCircle(sketch, "E45.106.32.0", {"center": v(76, -44) * mm, "radius": 1.5 * mm});
            skCircle(sketch, "E45.108.32.0", {"center": v(-4, -44) * mm, "radius": 1.5 * mm});
            skCircle(sketch, "E45.110.32.0", {"center": v(41, -44) * mm, "radius": 1.5 * mm});
            skCircle(sketch, "E45.112.32.0", {"center": v(-34, -44) * mm, "radius": 1.5 * mm});
            skCircle(sketch, "E45.114.32.0", {"center": v(-114, -44) * mm, "radius": 1.5 * mm});
            skCircle(sketch, "E45.116.32.0", {"center": v(121, -44) * mm, "radius": 1.5 * mm});
            skCircle(sketch, "E45.118.32.0", {"center": v(-74, -44) * mm, "radius": 1.5 * mm});
            skCircle(sketch, "E45.120.32.0", {"center": v(-154, -44) * mm, "radius": 1.5 * mm});
            skCircle(sketch, "E45.122.32.0", {"center": v(161, -44) * mm, "radius": 1.5 * mm});
            skCircle(sketch, "E45.124.32.0", {"center": v(81, -44) * mm, "radius": 1.5 * mm});
            skCircle(sketch, "E45.126.32.0", {"center": v(1, -44) * mm, "radius": 1.5 * mm});
            skCircle(sketch, "E45.128.32.0", {"center": v(46, -44) * mm, "radius": 1.5 * mm});
            skCircle(sketch, "E45.130.32.0", {"center": v(-29, -44) * mm, "radius": 1.5 * mm});
            skCircle(sketch, "E45.132.32.0", {"center": v(-109, -44) * mm, "radius": 1.5 * mm});
            skCircle(sketch, "E45.134.32.0", {"center": v(126, -44) * mm, "radius": 1.5 * mm});
            skLineSegment(sketch, "E45.136.32.0", {"start": v(-174, -44) * mm, "end": v(-169, -44) * mm, "construction": true});
            skCircle(sketch, "E45.139.32.0", {"center": v(-174, -44) * mm, "radius": 1.5 * mm});
            skCircle(sketch, "E45.141.32.0", {"center": v(-169, -44) * mm, "radius": 1.5 * mm});
            skCircle(sketch, "E45.0.33.0", {"center": v(166, -49) * mm, "radius": 1.5 * mm});
            skCircle(sketch, "E45.2.33.0", {"center": v(21, -49) * mm, "radius": 1.5 * mm});
            skCircle(sketch, "E45.4.33.0", {"center": v(-99, -49) * mm, "radius": 1.5 * mm});
            skCircle(sketch, "E45.6.33.0", {"center": v(6, -49) * mm, "radius": 1.5 * mm});
            skCircle(sketch, "E45.8.33.0", {"center": v(-54, -49) * mm, "radius": 1.5 * mm});
            skCircle(sketch, "E45.10.33.0", {"center": v(171, -49) * mm, "radius": 1.5 * mm});
            skCircle(sketch, "E45.12.33.0", {"center": v(-104, -49) * mm, "radius": 1.5 * mm});
            skCircle(sketch, "E45.14.33.0", {"center": v(11, -49) * mm, "radius": 1.5 * mm});
            skCircle(sketch, "E45.16.33.0", {"center": v(56, -49) * mm, "radius": 1.5 * mm});
            skCircle(sketch, "E45.18.33.0", {"center": v(-134, -49) * mm, "radius": 1.5 * mm});
            skCircle(sketch, "E45.20.33.0", {"center": v(51, -49) * mm, "radius": 1.5 * mm});
            skCircle(sketch, "E45.22.33.0", {"center": v(131, -49) * mm, "radius": 1.5 * mm});
            skCircle(sketch, "E45.24.33.0", {"center": v(151, -49) * mm, "radius": 1.5 * mm});
            skCircle(sketch, "E45.26.33.0", {"center": v(-24, -49) * mm, "radius": 1.5 * mm});
            skCircle(sketch, "E45.28.33.0", {"center": v(-64, -49) * mm, "radius": 1.5 * mm});
            skCircle(sketch, "E45.30.33.0", {"center": v(-9, -49) * mm, "radius": 1.5 * mm});
            skCircle(sketch, "E45.32.33.0", {"center": v(136, -49) * mm, "radius": 1.5 * mm});
            skCircle(sketch, "E45.34.33.0", {"center": v(91, -49) * mm, "radius": 1.5 * mm});
            skCircle(sketch, "E45.36.33.0", {"center": v(101, -49) * mm, "radius": 1.5 * mm});
            skCircle(sketch, "E45.38.33.0", {"center": v(-144, -49) * mm, "radius": 1.5 * mm});
            skCircle(sketch, "E45.40.33.0", {"center": v(71, -49) * mm, "radius": 1.5 * mm});
            skCircle(sketch, "E45.42.33.0", {"center": v(-69, -49) * mm, "radius": 1.5 * mm});
            skCircle(sketch, "E45.44.33.0", {"center": v(-84, -49) * mm, "radius": 1.5 * mm});
            skCircle(sketch, "E45.46.33.0", {"center": v(116, -49) * mm, "radius": 1.5 * mm});
            skCircle(sketch, "E45.48.33.0", {"center": v(-164, -49) * mm, "radius": 1.5 * mm});
            skCircle(sketch, "E45.50.33.0", {"center": v(86, -49) * mm, "radius": 1.5 * mm});
            skCircle(sketch, "E45.52.33.0", {"center": v(-149, -49) * mm, "radius": 1.5 * mm});
            skCircle(sketch, "E45.54.33.0", {"center": v(106, -49) * mm, "radius": 1.5 * mm});
            skCircle(sketch, "E45.56.33.0", {"center": v(-94, -49) * mm, "radius": 1.5 * mm});
            skCircle(sketch, "E45.58.33.0", {"center": v(-129, -49) * mm, "radius": 1.5 * mm});
            skCircle(sketch, "E45.60.33.0", {"center": v(-19, -49) * mm, "radius": 1.5 * mm});
            skCircle(sketch, "E45.62.33.0", {"center": v(-49, -49) * mm, "radius": 1.5 * mm});
            skCircle(sketch, "E45.64.33.0", {"center": v(26, -49) * mm, "radius": 1.5 * mm});
            skCircle(sketch, "E45.66.33.0", {"center": v(61, -49) * mm, "radius": 1.5 * mm});
            skCircle(sketch, "E45.68.33.0", {"center": v(16, -49) * mm, "radius": 1.5 * mm});
            skCircle(sketch, "E45.70.33.0", {"center": v(96, -49) * mm, "radius": 1.5 * mm});
            skCircle(sketch, "E45.72.33.0", {"center": v(-139, -49) * mm, "radius": 1.5 * mm});
            skCircle(sketch, "E45.74.33.0", {"center": v(-59, -49) * mm, "radius": 1.5 * mm});
            skCircle(sketch, "E45.76.33.0", {"center": v(111, -49) * mm, "radius": 1.5 * mm});
            skCircle(sketch, "E45.78.33.0", {"center": v(146, -49) * mm, "radius": 1.5 * mm});
            skCircle(sketch, "E45.80.33.0", {"center": v(-89, -49) * mm, "radius": 1.5 * mm});
            skCircle(sketch, "E45.82.33.0", {"center": v(-44, -49) * mm, "radius": 1.5 * mm});
            skCircle(sketch, "E45.84.33.0", {"center": v(-124, -49) * mm, "radius": 1.5 * mm});
            skCircle(sketch, "E45.86.33.0", {"center": v(-14, -49) * mm, "radius": 1.5 * mm});
            skCircle(sketch, "E45.88.33.0", {"center": v(31, -49) * mm, "radius": 1.5 * mm});
            skCircle(sketch, "E45.90.33.0", {"center": v(66, -49) * mm, "radius": 1.5 * mm});
            skCircle(sketch, "E45.92.33.0", {"center": v(141, -49) * mm, "radius": 1.5 * mm});
            skCircle(sketch, "E45.94.33.0", {"center": v(36, -49) * mm, "radius": 1.5 * mm});
            skCircle(sketch, "E45.96.33.0", {"center": v(-39, -49) * mm, "radius": 1.5 * mm});
            skCircle(sketch, "E45.98.33.0", {"center": v(-119, -49) * mm, "radius": 1.5 * mm});
            skCircle(sketch, "E45.100.33.0", {"center": v(-79, -49) * mm, "radius": 1.5 * mm});
            skCircle(sketch, "E45.102.33.0", {"center": v(-159, -49) * mm, "radius": 1.5 * mm});
            skCircle(sketch, "E45.104.33.0", {"center": v(156, -49) * mm, "radius": 1.5 * mm});
            skCircle(sketch, "E45.106.33.0", {"center": v(76, -49) * mm, "radius": 1.5 * mm});
            skCircle(sketch, "E45.108.33.0", {"center": v(-4, -49) * mm, "radius": 1.5 * mm});
            skCircle(sketch, "E45.110.33.0", {"center": v(41, -49) * mm, "radius": 1.5 * mm});
            skCircle(sketch, "E45.112.33.0", {"center": v(-34, -49) * mm, "radius": 1.5 * mm});
            skCircle(sketch, "E45.114.33.0", {"center": v(-114, -49) * mm, "radius": 1.5 * mm});
            skCircle(sketch, "E45.116.33.0", {"center": v(121, -49) * mm, "radius": 1.5 * mm});
            skCircle(sketch, "E45.118.33.0", {"center": v(-74, -49) * mm, "radius": 1.5 * mm});
            skCircle(sketch, "E45.120.33.0", {"center": v(-154, -49) * mm, "radius": 1.5 * mm});
            skCircle(sketch, "E45.122.33.0", {"center": v(161, -49) * mm, "radius": 1.5 * mm});
            skCircle(sketch, "E45.124.33.0", {"center": v(81, -49) * mm, "radius": 1.5 * mm});
            skCircle(sketch, "E45.126.33.0", {"center": v(1, -49) * mm, "radius": 1.5 * mm});
            skCircle(sketch, "E45.128.33.0", {"center": v(46, -49) * mm, "radius": 1.5 * mm});
            skCircle(sketch, "E45.130.33.0", {"center": v(-29, -49) * mm, "radius": 1.5 * mm});
            skCircle(sketch, "E45.132.33.0", {"center": v(-109, -49) * mm, "radius": 1.5 * mm});
            skCircle(sketch, "E45.134.33.0", {"center": v(126, -49) * mm, "radius": 1.5 * mm});
            skLineSegment(sketch, "E45.136.33.0", {"start": v(-174, -49) * mm, "end": v(-169, -49) * mm, "construction": true});
            skCircle(sketch, "E45.139.33.0", {"center": v(-174, -49) * mm, "radius": 1.5 * mm});
            skCircle(sketch, "E45.141.33.0", {"center": v(-169, -49) * mm, "radius": 1.5 * mm});
            skCircle(sketch, "E45.0.34.0", {"center": v(166, -54) * mm, "radius": 1.5 * mm});
            skCircle(sketch, "E45.2.34.0", {"center": v(21, -54) * mm, "radius": 1.5 * mm});
            skCircle(sketch, "E45.4.34.0", {"center": v(-99, -54) * mm, "radius": 1.5 * mm});
            skCircle(sketch, "E45.6.34.0", {"center": v(6, -54) * mm, "radius": 1.5 * mm});
            skCircle(sketch, "E45.8.34.0", {"center": v(-54, -54) * mm, "radius": 1.5 * mm});
            skCircle(sketch, "E45.10.34.0", {"center": v(171, -54) * mm, "radius": 1.5 * mm});
            skCircle(sketch, "E45.12.34.0", {"center": v(-104, -54) * mm, "radius": 1.5 * mm});
            skCircle(sketch, "E45.14.34.0", {"center": v(11, -54) * mm, "radius": 1.5 * mm});
            skCircle(sketch, "E45.16.34.0", {"center": v(56, -54) * mm, "radius": 1.5 * mm});
            skCircle(sketch, "E45.18.34.0", {"center": v(-134, -54) * mm, "radius": 1.5 * mm});
            skCircle(sketch, "E45.20.34.0", {"center": v(51, -54) * mm, "radius": 1.5 * mm});
            skCircle(sketch, "E45.22.34.0", {"center": v(131, -54) * mm, "radius": 1.5 * mm});
            skCircle(sketch, "E45.24.34.0", {"center": v(151, -54) * mm, "radius": 1.5 * mm});
            skCircle(sketch, "E45.26.34.0", {"center": v(-24, -54) * mm, "radius": 1.5 * mm});
            skCircle(sketch, "E45.28.34.0", {"center": v(-64, -54) * mm, "radius": 1.5 * mm});
            skCircle(sketch, "E45.30.34.0", {"center": v(-9, -54) * mm, "radius": 1.5 * mm});
            skCircle(sketch, "E45.32.34.0", {"center": v(136, -54) * mm, "radius": 1.5 * mm});
            skCircle(sketch, "E45.34.34.0", {"center": v(91, -54) * mm, "radius": 1.5 * mm});
            skCircle(sketch, "E45.36.34.0", {"center": v(101, -54) * mm, "radius": 1.5 * mm});
            skCircle(sketch, "E45.38.34.0", {"center": v(-144, -54) * mm, "radius": 1.5 * mm});
            skCircle(sketch, "E45.40.34.0", {"center": v(71, -54) * mm, "radius": 1.5 * mm});
            skCircle(sketch, "E45.42.34.0", {"center": v(-69, -54) * mm, "radius": 1.5 * mm});
            skCircle(sketch, "E45.44.34.0", {"center": v(-84, -54) * mm, "radius": 1.5 * mm});
            skCircle(sketch, "E45.46.34.0", {"center": v(116, -54) * mm, "radius": 1.5 * mm});
            skCircle(sketch, "E45.48.34.0", {"center": v(-164, -54) * mm, "radius": 1.5 * mm});
            skCircle(sketch, "E45.50.34.0", {"center": v(86, -54) * mm, "radius": 1.5 * mm});
            skCircle(sketch, "E45.52.34.0", {"center": v(-149, -54) * mm, "radius": 1.5 * mm});
            skCircle(sketch, "E45.54.34.0", {"center": v(106, -54) * mm, "radius": 1.5 * mm});
            skCircle(sketch, "E45.56.34.0", {"center": v(-94, -54) * mm, "radius": 1.5 * mm});
            skCircle(sketch, "E45.58.34.0", {"center": v(-129, -54) * mm, "radius": 1.5 * mm});
            skCircle(sketch, "E45.60.34.0", {"center": v(-19, -54) * mm, "radius": 1.5 * mm});
            skCircle(sketch, "E45.62.34.0", {"center": v(-49, -54) * mm, "radius": 1.5 * mm});
            skCircle(sketch, "E45.64.34.0", {"center": v(26, -54) * mm, "radius": 1.5 * mm});
            skCircle(sketch, "E45.66.34.0", {"center": v(61, -54) * mm, "radius": 1.5 * mm});
            skCircle(sketch, "E45.68.34.0", {"center": v(16, -54) * mm, "radius": 1.5 * mm});
            skCircle(sketch, "E45.70.34.0", {"center": v(96, -54) * mm, "radius": 1.5 * mm});
            skCircle(sketch, "E45.72.34.0", {"center": v(-139, -54) * mm, "radius": 1.5 * mm});
            skCircle(sketch, "E45.74.34.0", {"center": v(-59, -54) * mm, "radius": 1.5 * mm});
            skCircle(sketch, "E45.76.34.0", {"center": v(111, -54) * mm, "radius": 1.5 * mm});
            skCircle(sketch, "E45.78.34.0", {"center": v(146, -54) * mm, "radius": 1.5 * mm});
            skCircle(sketch, "E45.80.34.0", {"center": v(-89, -54) * mm, "radius": 1.5 * mm});
            skCircle(sketch, "E45.82.34.0", {"center": v(-44, -54) * mm, "radius": 1.5 * mm});
            skCircle(sketch, "E45.84.34.0", {"center": v(-124, -54) * mm, "radius": 1.5 * mm});
            skCircle(sketch, "E45.86.34.0", {"center": v(-14, -54) * mm, "radius": 1.5 * mm});
            skCircle(sketch, "E45.88.34.0", {"center": v(31, -54) * mm, "radius": 1.5 * mm});
            skCircle(sketch, "E45.90.34.0", {"center": v(66, -54) * mm, "radius": 1.5 * mm});
            skCircle(sketch, "E45.92.34.0", {"center": v(141, -54) * mm, "radius": 1.5 * mm});
            skCircle(sketch, "E45.94.34.0", {"center": v(36, -54) * mm, "radius": 1.5 * mm});
            skCircle(sketch, "E45.96.34.0", {"center": v(-39, -54) * mm, "radius": 1.5 * mm});
            skCircle(sketch, "E45.98.34.0", {"center": v(-119, -54) * mm, "radius": 1.5 * mm});
            skCircle(sketch, "E45.100.34.0", {"center": v(-79, -54) * mm, "radius": 1.5 * mm});
            skCircle(sketch, "E45.102.34.0", {"center": v(-159, -54) * mm, "radius": 1.5 * mm});
            skCircle(sketch, "E45.104.34.0", {"center": v(156, -54) * mm, "radius": 1.5 * mm});
            skCircle(sketch, "E45.106.34.0", {"center": v(76, -54) * mm, "radius": 1.5 * mm});
            skCircle(sketch, "E45.108.34.0", {"center": v(-4, -54) * mm, "radius": 1.5 * mm});
            skCircle(sketch, "E45.110.34.0", {"center": v(41, -54) * mm, "radius": 1.5 * mm});
            skCircle(sketch, "E45.112.34.0", {"center": v(-34, -54) * mm, "radius": 1.5 * mm});
            skCircle(sketch, "E45.114.34.0", {"center": v(-114, -54) * mm, "radius": 1.5 * mm});
            skCircle(sketch, "E45.116.34.0", {"center": v(121, -54) * mm, "radius": 1.5 * mm});
            skCircle(sketch, "E45.118.34.0", {"center": v(-74, -54) * mm, "radius": 1.5 * mm});
            skCircle(sketch, "E45.120.34.0", {"center": v(-154, -54) * mm, "radius": 1.5 * mm});
            skCircle(sketch, "E45.122.34.0", {"center": v(161, -54) * mm, "radius": 1.5 * mm});
            skCircle(sketch, "E45.124.34.0", {"center": v(81, -54) * mm, "radius": 1.5 * mm});
            skCircle(sketch, "E45.126.34.0", {"center": v(1, -54) * mm, "radius": 1.5 * mm});
            skCircle(sketch, "E45.128.34.0", {"center": v(46, -54) * mm, "radius": 1.5 * mm});
            skCircle(sketch, "E45.130.34.0", {"center": v(-29, -54) * mm, "radius": 1.5 * mm});
            skCircle(sketch, "E45.132.34.0", {"center": v(-109, -54) * mm, "radius": 1.5 * mm});
            skCircle(sketch, "E45.134.34.0", {"center": v(126, -54) * mm, "radius": 1.5 * mm});
            skLineSegment(sketch, "E45.136.34.0", {"start": v(-174, -54) * mm, "end": v(-169, -54) * mm, "construction": true});
            skCircle(sketch, "E45.139.34.0", {"center": v(-174, -54) * mm, "radius": 1.5 * mm});
            skCircle(sketch, "E45.141.34.0", {"center": v(-169, -54) * mm, "radius": 1.5 * mm});
            skCircle(sketch, "E45.0.35.0", {"center": v(166, -59) * mm, "radius": 1.5 * mm});
            skCircle(sketch, "E45.2.35.0", {"center": v(21, -59) * mm, "radius": 1.5 * mm});
            skCircle(sketch, "E45.4.35.0", {"center": v(-99, -59) * mm, "radius": 1.5 * mm});
            skCircle(sketch, "E45.6.35.0", {"center": v(6, -59) * mm, "radius": 1.5 * mm});
            skCircle(sketch, "E45.8.35.0", {"center": v(-54, -59) * mm, "radius": 1.5 * mm});
            skCircle(sketch, "E45.10.35.0", {"center": v(171, -59) * mm, "radius": 1.5 * mm});
            skCircle(sketch, "E45.12.35.0", {"center": v(-104, -59) * mm, "radius": 1.5 * mm});
            skCircle(sketch, "E45.14.35.0", {"center": v(11, -59) * mm, "radius": 1.5 * mm});
            skCircle(sketch, "E45.16.35.0", {"center": v(56, -59) * mm, "radius": 1.5 * mm});
            skCircle(sketch, "E45.18.35.0", {"center": v(-134, -59) * mm, "radius": 1.5 * mm});
            skCircle(sketch, "E45.20.35.0", {"center": v(51, -59) * mm, "radius": 1.5 * mm});
            skCircle(sketch, "E45.22.35.0", {"center": v(131, -59) * mm, "radius": 1.5 * mm});
            skCircle(sketch, "E45.24.35.0", {"center": v(151, -59) * mm, "radius": 1.5 * mm});
            skCircle(sketch, "E45.26.35.0", {"center": v(-24, -59) * mm, "radius": 1.5 * mm});
            skCircle(sketch, "E45.28.35.0", {"center": v(-64, -59) * mm, "radius": 1.5 * mm});
            skCircle(sketch, "E45.30.35.0", {"center": v(-9, -59) * mm, "radius": 1.5 * mm});
            skCircle(sketch, "E45.32.35.0", {"center": v(136, -59) * mm, "radius": 1.5 * mm});
            skCircle(sketch, "E45.34.35.0", {"center": v(91, -59) * mm, "radius": 1.5 * mm});
            skCircle(sketch, "E45.36.35.0", {"center": v(101, -59) * mm, "radius": 1.5 * mm});
            skCircle(sketch, "E45.38.35.0", {"center": v(-144, -59) * mm, "radius": 1.5 * mm});
            skCircle(sketch, "E45.40.35.0", {"center": v(71, -59) * mm, "radius": 1.5 * mm});
            skCircle(sketch, "E45.42.35.0", {"center": v(-69, -59) * mm, "radius": 1.5 * mm});
            skCircle(sketch, "E45.44.35.0", {"center": v(-84, -59) * mm, "radius": 1.5 * mm});
            skCircle(sketch, "E45.46.35.0", {"center": v(116, -59) * mm, "radius": 1.5 * mm});
            skCircle(sketch, "E45.48.35.0", {"center": v(-164, -59) * mm, "radius": 1.5 * mm});
            skCircle(sketch, "E45.50.35.0", {"center": v(86, -59) * mm, "radius": 1.5 * mm});
            skCircle(sketch, "E45.52.35.0", {"center": v(-149, -59) * mm, "radius": 1.5 * mm});
            skCircle(sketch, "E45.54.35.0", {"center": v(106, -59) * mm, "radius": 1.5 * mm});
            skCircle(sketch, "E45.56.35.0", {"center": v(-94, -59) * mm, "radius": 1.5 * mm});
            skCircle(sketch, "E45.58.35.0", {"center": v(-129, -59) * mm, "radius": 1.5 * mm});
            skCircle(sketch, "E45.60.35.0", {"center": v(-19, -59) * mm, "radius": 1.5 * mm});
            skCircle(sketch, "E45.62.35.0", {"center": v(-49, -59) * mm, "radius": 1.5 * mm});
            skCircle(sketch, "E45.64.35.0", {"center": v(26, -59) * mm, "radius": 1.5 * mm});
            skCircle(sketch, "E45.66.35.0", {"center": v(61, -59) * mm, "radius": 1.5 * mm});
            skCircle(sketch, "E45.68.35.0", {"center": v(16, -59) * mm, "radius": 1.5 * mm});
            skCircle(sketch, "E45.70.35.0", {"center": v(96, -59) * mm, "radius": 1.5 * mm});
            skCircle(sketch, "E45.72.35.0", {"center": v(-139, -59) * mm, "radius": 1.5 * mm});
            skCircle(sketch, "E45.74.35.0", {"center": v(-59, -59) * mm, "radius": 1.5 * mm});
            skCircle(sketch, "E45.76.35.0", {"center": v(111, -59) * mm, "radius": 1.5 * mm});
            skCircle(sketch, "E45.78.35.0", {"center": v(146, -59) * mm, "radius": 1.5 * mm});
            skCircle(sketch, "E45.80.35.0", {"center": v(-89, -59) * mm, "radius": 1.5 * mm});
            skCircle(sketch, "E45.82.35.0", {"center": v(-44, -59) * mm, "radius": 1.5 * mm});
            skCircle(sketch, "E45.84.35.0", {"center": v(-124, -59) * mm, "radius": 1.5 * mm});
            skCircle(sketch, "E45.86.35.0", {"center": v(-14, -59) * mm, "radius": 1.5 * mm});
            skCircle(sketch, "E45.88.35.0", {"center": v(31, -59) * mm, "radius": 1.5 * mm});
            skCircle(sketch, "E45.90.35.0", {"center": v(66, -59) * mm, "radius": 1.5 * mm});
            skCircle(sketch, "E45.92.35.0", {"center": v(141, -59) * mm, "radius": 1.5 * mm});
            skCircle(sketch, "E45.94.35.0", {"center": v(36, -59) * mm, "radius": 1.5 * mm});
            skCircle(sketch, "E45.96.35.0", {"center": v(-39, -59) * mm, "radius": 1.5 * mm});
            skCircle(sketch, "E45.98.35.0", {"center": v(-119, -59) * mm, "radius": 1.5 * mm});
            skCircle(sketch, "E45.100.35.0", {"center": v(-79, -59) * mm, "radius": 1.5 * mm});
            skCircle(sketch, "E45.102.35.0", {"center": v(-159, -59) * mm, "radius": 1.5 * mm});
            skCircle(sketch, "E45.104.35.0", {"center": v(156, -59) * mm, "radius": 1.5 * mm});
            skCircle(sketch, "E45.106.35.0", {"center": v(76, -59) * mm, "radius": 1.5 * mm});
            skCircle(sketch, "E45.108.35.0", {"center": v(-4, -59) * mm, "radius": 1.5 * mm});
            skCircle(sketch, "E45.110.35.0", {"center": v(41, -59) * mm, "radius": 1.5 * mm});
            skCircle(sketch, "E45.112.35.0", {"center": v(-34, -59) * mm, "radius": 1.5 * mm});
            skCircle(sketch, "E45.114.35.0", {"center": v(-114, -59) * mm, "radius": 1.5 * mm});
            skCircle(sketch, "E45.116.35.0", {"center": v(121, -59) * mm, "radius": 1.5 * mm});
            skCircle(sketch, "E45.118.35.0", {"center": v(-74, -59) * mm, "radius": 1.5 * mm});
            skCircle(sketch, "E45.120.35.0", {"center": v(-154, -59) * mm, "radius": 1.5 * mm});
            skCircle(sketch, "E45.122.35.0", {"center": v(161, -59) * mm, "radius": 1.5 * mm});
            skCircle(sketch, "E45.124.35.0", {"center": v(81, -59) * mm, "radius": 1.5 * mm});
            skCircle(sketch, "E45.126.35.0", {"center": v(1, -59) * mm, "radius": 1.5 * mm});
            skCircle(sketch, "E45.128.35.0", {"center": v(46, -59) * mm, "radius": 1.5 * mm});
            skCircle(sketch, "E45.130.35.0", {"center": v(-29, -59) * mm, "radius": 1.5 * mm});
            skCircle(sketch, "E45.132.35.0", {"center": v(-109, -59) * mm, "radius": 1.5 * mm});
            skCircle(sketch, "E45.134.35.0", {"center": v(126, -59) * mm, "radius": 1.5 * mm});
            skLineSegment(sketch, "E45.136.35.0", {"start": v(-174, -59) * mm, "end": v(-169, -59) * mm, "construction": true});
            skCircle(sketch, "E45.139.35.0", {"center": v(-174, -59) * mm, "radius": 1.5 * mm});
            skCircle(sketch, "E45.141.35.0", {"center": v(-169, -59) * mm, "radius": 1.5 * mm});
            skCircle(sketch, "E45.0.36.0", {"center": v(166, -64) * mm, "radius": 1.5 * mm});
            skCircle(sketch, "E45.2.36.0", {"center": v(21, -64) * mm, "radius": 1.5 * mm});
            skCircle(sketch, "E45.4.36.0", {"center": v(-99, -64) * mm, "radius": 1.5 * mm});
            skCircle(sketch, "E45.6.36.0", {"center": v(6, -64) * mm, "radius": 1.5 * mm});
            skCircle(sketch, "E45.8.36.0", {"center": v(-54, -64) * mm, "radius": 1.5 * mm});
            skCircle(sketch, "E45.10.36.0", {"center": v(171, -64) * mm, "radius": 1.5 * mm});
            skCircle(sketch, "E45.12.36.0", {"center": v(-104, -64) * mm, "radius": 1.5 * mm});
            skCircle(sketch, "E45.14.36.0", {"center": v(11, -64) * mm, "radius": 1.5 * mm});
            skCircle(sketch, "E45.16.36.0", {"center": v(56, -64) * mm, "radius": 1.5 * mm});
            skCircle(sketch, "E45.18.36.0", {"center": v(-134, -64) * mm, "radius": 1.5 * mm});
            skCircle(sketch, "E45.20.36.0", {"center": v(51, -64) * mm, "radius": 1.5 * mm});
            skCircle(sketch, "E45.22.36.0", {"center": v(131, -64) * mm, "radius": 1.5 * mm});
            skCircle(sketch, "E45.24.36.0", {"center": v(151, -64) * mm, "radius": 1.5 * mm});
            skCircle(sketch, "E45.26.36.0", {"center": v(-24, -64) * mm, "radius": 1.5 * mm});
            skCircle(sketch, "E45.28.36.0", {"center": v(-64, -64) * mm, "radius": 1.5 * mm});
            skCircle(sketch, "E45.30.36.0", {"center": v(-9, -64) * mm, "radius": 1.5 * mm});
            skCircle(sketch, "E45.32.36.0", {"center": v(136, -64) * mm, "radius": 1.5 * mm});
            skCircle(sketch, "E45.34.36.0", {"center": v(91, -64) * mm, "radius": 1.5 * mm});
            skCircle(sketch, "E45.36.36.0", {"center": v(101, -64) * mm, "radius": 1.5 * mm});
            skCircle(sketch, "E45.38.36.0", {"center": v(-144, -64) * mm, "radius": 1.5 * mm});
            skCircle(sketch, "E45.40.36.0", {"center": v(71, -64) * mm, "radius": 1.5 * mm});
            skCircle(sketch, "E45.42.36.0", {"center": v(-69, -64) * mm, "radius": 1.5 * mm});
            skCircle(sketch, "E45.44.36.0", {"center": v(-84, -64) * mm, "radius": 1.5 * mm});
            skCircle(sketch, "E45.46.36.0", {"center": v(116, -64) * mm, "radius": 1.5 * mm});
            skCircle(sketch, "E45.48.36.0", {"center": v(-164, -64) * mm, "radius": 1.5 * mm});
            skCircle(sketch, "E45.50.36.0", {"center": v(86, -64) * mm, "radius": 1.5 * mm});
            skCircle(sketch, "E45.52.36.0", {"center": v(-149, -64) * mm, "radius": 1.5 * mm});
            skCircle(sketch, "E45.54.36.0", {"center": v(106, -64) * mm, "radius": 1.5 * mm});
            skCircle(sketch, "E45.56.36.0", {"center": v(-94, -64) * mm, "radius": 1.5 * mm});
            skCircle(sketch, "E45.58.36.0", {"center": v(-129, -64) * mm, "radius": 1.5 * mm});
            skCircle(sketch, "E45.60.36.0", {"center": v(-19, -64) * mm, "radius": 1.5 * mm});
            skCircle(sketch, "E45.62.36.0", {"center": v(-49, -64) * mm, "radius": 1.5 * mm});
            skCircle(sketch, "E45.64.36.0", {"center": v(26, -64) * mm, "radius": 1.5 * mm});
            skCircle(sketch, "E45.66.36.0", {"center": v(61, -64) * mm, "radius": 1.5 * mm});
            skCircle(sketch, "E45.68.36.0", {"center": v(16, -64) * mm, "radius": 1.5 * mm});
            skCircle(sketch, "E45.70.36.0", {"center": v(96, -64) * mm, "radius": 1.5 * mm});
            skCircle(sketch, "E45.72.36.0", {"center": v(-139, -64) * mm, "radius": 1.5 * mm});
            skCircle(sketch, "E45.74.36.0", {"center": v(-59, -64) * mm, "radius": 1.5 * mm});
            skCircle(sketch, "E45.76.36.0", {"center": v(111, -64) * mm, "radius": 1.5 * mm});
            skCircle(sketch, "E45.78.36.0", {"center": v(146, -64) * mm, "radius": 1.5 * mm});
            skCircle(sketch, "E45.80.36.0", {"center": v(-89, -64) * mm, "radius": 1.5 * mm});
            skCircle(sketch, "E45.82.36.0", {"center": v(-44, -64) * mm, "radius": 1.5 * mm});
            skCircle(sketch, "E45.84.36.0", {"center": v(-124, -64) * mm, "radius": 1.5 * mm});
            skCircle(sketch, "E45.86.36.0", {"center": v(-14, -64) * mm, "radius": 1.5 * mm});
            skCircle(sketch, "E45.88.36.0", {"center": v(31, -64) * mm, "radius": 1.5 * mm});
            skCircle(sketch, "E45.90.36.0", {"center": v(66, -64) * mm, "radius": 1.5 * mm});
            skCircle(sketch, "E45.92.36.0", {"center": v(141, -64) * mm, "radius": 1.5 * mm});
            skCircle(sketch, "E45.94.36.0", {"center": v(36, -64) * mm, "radius": 1.5 * mm});
            skCircle(sketch, "E45.96.36.0", {"center": v(-39, -64) * mm, "radius": 1.5 * mm});
            skCircle(sketch, "E45.98.36.0", {"center": v(-119, -64) * mm, "radius": 1.5 * mm});
            skCircle(sketch, "E45.100.36.0", {"center": v(-79, -64) * mm, "radius": 1.5 * mm});
            skCircle(sketch, "E45.102.36.0", {"center": v(-159, -64) * mm, "radius": 1.5 * mm});
            skCircle(sketch, "E45.104.36.0", {"center": v(156, -64) * mm, "radius": 1.5 * mm});
            skCircle(sketch, "E45.106.36.0", {"center": v(76, -64) * mm, "radius": 1.5 * mm});
            skCircle(sketch, "E45.108.36.0", {"center": v(-4, -64) * mm, "radius": 1.5 * mm});
            skCircle(sketch, "E45.110.36.0", {"center": v(41, -64) * mm, "radius": 1.5 * mm});
            skCircle(sketch, "E45.112.36.0", {"center": v(-34, -64) * mm, "radius": 1.5 * mm});
            skCircle(sketch, "E45.114.36.0", {"center": v(-114, -64) * mm, "radius": 1.5 * mm});
            skCircle(sketch, "E45.116.36.0", {"center": v(121, -64) * mm, "radius": 1.5 * mm});
            skCircle(sketch, "E45.118.36.0", {"center": v(-74, -64) * mm, "radius": 1.5 * mm});
            skCircle(sketch, "E45.120.36.0", {"center": v(-154, -64) * mm, "radius": 1.5 * mm});
            skCircle(sketch, "E45.122.36.0", {"center": v(161, -64) * mm, "radius": 1.5 * mm});
            skCircle(sketch, "E45.124.36.0", {"center": v(81, -64) * mm, "radius": 1.5 * mm});
            skCircle(sketch, "E45.126.36.0", {"center": v(1, -64) * mm, "radius": 1.5 * mm});
            skCircle(sketch, "E45.128.36.0", {"center": v(46, -64) * mm, "radius": 1.5 * mm});
            skCircle(sketch, "E45.130.36.0", {"center": v(-29, -64) * mm, "radius": 1.5 * mm});
            skCircle(sketch, "E45.132.36.0", {"center": v(-109, -64) * mm, "radius": 1.5 * mm});
            skCircle(sketch, "E45.134.36.0", {"center": v(126, -64) * mm, "radius": 1.5 * mm});
            skLineSegment(sketch, "E45.136.36.0", {"start": v(-174, -64) * mm, "end": v(-169, -64) * mm, "construction": true});
            skCircle(sketch, "E45.139.36.0", {"center": v(-174, -64) * mm, "radius": 1.5 * mm});
            skCircle(sketch, "E45.141.36.0", {"center": v(-169, -64) * mm, "radius": 1.5 * mm});
            skCircle(sketch, "E45.0.37.0", {"center": v(166, -69) * mm, "radius": 1.5 * mm});
            skCircle(sketch, "E45.2.37.0", {"center": v(21, -69) * mm, "radius": 1.5 * mm});
            skCircle(sketch, "E45.4.37.0", {"center": v(-99, -69) * mm, "radius": 1.5 * mm});
            skCircle(sketch, "E45.6.37.0", {"center": v(6, -69) * mm, "radius": 1.5 * mm});
            skCircle(sketch, "E45.8.37.0", {"center": v(-54, -69) * mm, "radius": 1.5 * mm});
            skCircle(sketch, "E45.10.37.0", {"center": v(171, -69) * mm, "radius": 1.5 * mm});
            skCircle(sketch, "E45.12.37.0", {"center": v(-104, -69) * mm, "radius": 1.5 * mm});
            skCircle(sketch, "E45.14.37.0", {"center": v(11, -69) * mm, "radius": 1.5 * mm});
            skCircle(sketch, "E45.16.37.0", {"center": v(56, -69) * mm, "radius": 1.5 * mm});
            skCircle(sketch, "E45.18.37.0", {"center": v(-134, -69) * mm, "radius": 1.5 * mm});
            skCircle(sketch, "E45.20.37.0", {"center": v(51, -69) * mm, "radius": 1.5 * mm});
            skCircle(sketch, "E45.22.37.0", {"center": v(131, -69) * mm, "radius": 1.5 * mm});
            skCircle(sketch, "E45.24.37.0", {"center": v(151, -69) * mm, "radius": 1.5 * mm});
            skCircle(sketch, "E45.26.37.0", {"center": v(-24, -69) * mm, "radius": 1.5 * mm});
            skCircle(sketch, "E45.28.37.0", {"center": v(-64, -69) * mm, "radius": 1.5 * mm});
            skCircle(sketch, "E45.30.37.0", {"center": v(-9, -69) * mm, "radius": 1.5 * mm});
            skCircle(sketch, "E45.32.37.0", {"center": v(136, -69) * mm, "radius": 1.5 * mm});
            skCircle(sketch, "E45.34.37.0", {"center": v(91, -69) * mm, "radius": 1.5 * mm});
            skCircle(sketch, "E45.36.37.0", {"center": v(101, -69) * mm, "radius": 1.5 * mm});
            skCircle(sketch, "E45.38.37.0", {"center": v(-144, -69) * mm, "radius": 1.5 * mm});
            skCircle(sketch, "E45.40.37.0", {"center": v(71, -69) * mm, "radius": 1.5 * mm});
            skCircle(sketch, "E45.42.37.0", {"center": v(-69, -69) * mm, "radius": 1.5 * mm});
            skCircle(sketch, "E45.44.37.0", {"center": v(-84, -69) * mm, "radius": 1.5 * mm});
            skCircle(sketch, "E45.46.37.0", {"center": v(116, -69) * mm, "radius": 1.5 * mm});
            skCircle(sketch, "E45.48.37.0", {"center": v(-164, -69) * mm, "radius": 1.5 * mm});
            skCircle(sketch, "E45.50.37.0", {"center": v(86, -69) * mm, "radius": 1.5 * mm});
            skCircle(sketch, "E45.52.37.0", {"center": v(-149, -69) * mm, "radius": 1.5 * mm});
            skCircle(sketch, "E45.54.37.0", {"center": v(106, -69) * mm, "radius": 1.5 * mm});
            skCircle(sketch, "E45.56.37.0", {"center": v(-94, -69) * mm, "radius": 1.5 * mm});
            skCircle(sketch, "E45.58.37.0", {"center": v(-129, -69) * mm, "radius": 1.5 * mm});
            skCircle(sketch, "E45.60.37.0", {"center": v(-19, -69) * mm, "radius": 1.5 * mm});
            skCircle(sketch, "E45.62.37.0", {"center": v(-49, -69) * mm, "radius": 1.5 * mm});
            skCircle(sketch, "E45.64.37.0", {"center": v(26, -69) * mm, "radius": 1.5 * mm});
            skCircle(sketch, "E45.66.37.0", {"center": v(61, -69) * mm, "radius": 1.5 * mm});
            skCircle(sketch, "E45.68.37.0", {"center": v(16, -69) * mm, "radius": 1.5 * mm});
            skCircle(sketch, "E45.70.37.0", {"center": v(96, -69) * mm, "radius": 1.5 * mm});
            skCircle(sketch, "E45.72.37.0", {"center": v(-139, -69) * mm, "radius": 1.5 * mm});
            skCircle(sketch, "E45.74.37.0", {"center": v(-59, -69) * mm, "radius": 1.5 * mm});
            skCircle(sketch, "E45.76.37.0", {"center": v(111, -69) * mm, "radius": 1.5 * mm});
            skCircle(sketch, "E45.78.37.0", {"center": v(146, -69) * mm, "radius": 1.5 * mm});
            skCircle(sketch, "E45.80.37.0", {"center": v(-89, -69) * mm, "radius": 1.5 * mm});
            skCircle(sketch, "E45.82.37.0", {"center": v(-44, -69) * mm, "radius": 1.5 * mm});
            skCircle(sketch, "E45.84.37.0", {"center": v(-124, -69) * mm, "radius": 1.5 * mm});
            skCircle(sketch, "E45.86.37.0", {"center": v(-14, -69) * mm, "radius": 1.5 * mm});
            skCircle(sketch, "E45.88.37.0", {"center": v(31, -69) * mm, "radius": 1.5 * mm});
            skCircle(sketch, "E45.90.37.0", {"center": v(66, -69) * mm, "radius": 1.5 * mm});
            skCircle(sketch, "E45.92.37.0", {"center": v(141, -69) * mm, "radius": 1.5 * mm});
            skCircle(sketch, "E45.94.37.0", {"center": v(36, -69) * mm, "radius": 1.5 * mm});
            skCircle(sketch, "E45.96.37.0", {"center": v(-39, -69) * mm, "radius": 1.5 * mm});
            skCircle(sketch, "E45.98.37.0", {"center": v(-119, -69) * mm, "radius": 1.5 * mm});
            skCircle(sketch, "E45.100.37.0", {"center": v(-79, -69) * mm, "radius": 1.5 * mm});
            skCircle(sketch, "E45.102.37.0", {"center": v(-159, -69) * mm, "radius": 1.5 * mm});
            skCircle(sketch, "E45.104.37.0", {"center": v(156, -69) * mm, "radius": 1.5 * mm});
            skCircle(sketch, "E45.106.37.0", {"center": v(76, -69) * mm, "radius": 1.5 * mm});
            skCircle(sketch, "E45.108.37.0", {"center": v(-4, -69) * mm, "radius": 1.5 * mm});
            skCircle(sketch, "E45.110.37.0", {"center": v(41, -69) * mm, "radius": 1.5 * mm});
            skCircle(sketch, "E45.112.37.0", {"center": v(-34, -69) * mm, "radius": 1.5 * mm});
            skCircle(sketch, "E45.114.37.0", {"center": v(-114, -69) * mm, "radius": 1.5 * mm});
            skCircle(sketch, "E45.116.37.0", {"center": v(121, -69) * mm, "radius": 1.5 * mm});
            skCircle(sketch, "E45.118.37.0", {"center": v(-74, -69) * mm, "radius": 1.5 * mm});
            skCircle(sketch, "E45.120.37.0", {"center": v(-154, -69) * mm, "radius": 1.5 * mm});
            skCircle(sketch, "E45.122.37.0", {"center": v(161, -69) * mm, "radius": 1.5 * mm});
            skCircle(sketch, "E45.124.37.0", {"center": v(81, -69) * mm, "radius": 1.5 * mm});
            skCircle(sketch, "E45.126.37.0", {"center": v(1, -69) * mm, "radius": 1.5 * mm});
            skCircle(sketch, "E45.128.37.0", {"center": v(46, -69) * mm, "radius": 1.5 * mm});
            skCircle(sketch, "E45.130.37.0", {"center": v(-29, -69) * mm, "radius": 1.5 * mm});
            skCircle(sketch, "E45.132.37.0", {"center": v(-109, -69) * mm, "radius": 1.5 * mm});
            skCircle(sketch, "E45.134.37.0", {"center": v(126, -69) * mm, "radius": 1.5 * mm});
            skLineSegment(sketch, "E45.136.37.0", {"start": v(-174, -69) * mm, "end": v(-169, -69) * mm, "construction": true});
            skCircle(sketch, "E45.139.37.0", {"center": v(-174, -69) * mm, "radius": 1.5 * mm});
            skCircle(sketch, "E45.141.37.0", {"center": v(-169, -69) * mm, "radius": 1.5 * mm});
            skCircle(sketch, "E45.0.38.0", {"center": v(166, -74) * mm, "radius": 1.5 * mm});
            skCircle(sketch, "E45.2.38.0", {"center": v(21, -74) * mm, "radius": 1.5 * mm});
            skCircle(sketch, "E45.4.38.0", {"center": v(-99, -74) * mm, "radius": 1.5 * mm});
            skCircle(sketch, "E45.6.38.0", {"center": v(6, -74) * mm, "radius": 1.5 * mm});
            skCircle(sketch, "E45.8.38.0", {"center": v(-54, -74) * mm, "radius": 1.5 * mm});
            skCircle(sketch, "E45.10.38.0", {"center": v(171, -74) * mm, "radius": 1.5 * mm});
            skCircle(sketch, "E45.12.38.0", {"center": v(-104, -74) * mm, "radius": 1.5 * mm});
            skCircle(sketch, "E45.14.38.0", {"center": v(11, -74) * mm, "radius": 1.5 * mm});
            skCircle(sketch, "E45.16.38.0", {"center": v(56, -74) * mm, "radius": 1.5 * mm});
            skCircle(sketch, "E45.18.38.0", {"center": v(-134, -74) * mm, "radius": 1.5 * mm});
            skCircle(sketch, "E45.20.38.0", {"center": v(51, -74) * mm, "radius": 1.5 * mm});
            skCircle(sketch, "E45.22.38.0", {"center": v(131, -74) * mm, "radius": 1.5 * mm});
            skCircle(sketch, "E45.24.38.0", {"center": v(151, -74) * mm, "radius": 1.5 * mm});
            skCircle(sketch, "E45.26.38.0", {"center": v(-24, -74) * mm, "radius": 1.5 * mm});
            skCircle(sketch, "E45.28.38.0", {"center": v(-64, -74) * mm, "radius": 1.5 * mm});
            skCircle(sketch, "E45.30.38.0", {"center": v(-9, -74) * mm, "radius": 1.5 * mm});
            skCircle(sketch, "E45.32.38.0", {"center": v(136, -74) * mm, "radius": 1.5 * mm});
            skCircle(sketch, "E45.34.38.0", {"center": v(91, -74) * mm, "radius": 1.5 * mm});
            skCircle(sketch, "E45.36.38.0", {"center": v(101, -74) * mm, "radius": 1.5 * mm});
            skCircle(sketch, "E45.38.38.0", {"center": v(-144, -74) * mm, "radius": 1.5 * mm});
            skCircle(sketch, "E45.40.38.0", {"center": v(71, -74) * mm, "radius": 1.5 * mm});
            skCircle(sketch, "E45.42.38.0", {"center": v(-69, -74) * mm, "radius": 1.5 * mm});
            skCircle(sketch, "E45.44.38.0", {"center": v(-84, -74) * mm, "radius": 1.5 * mm});
            skCircle(sketch, "E45.46.38.0", {"center": v(116, -74) * mm, "radius": 1.5 * mm});
            skCircle(sketch, "E45.48.38.0", {"center": v(-164, -74) * mm, "radius": 1.5 * mm});
            skCircle(sketch, "E45.50.38.0", {"center": v(86, -74) * mm, "radius": 1.5 * mm});
            skCircle(sketch, "E45.52.38.0", {"center": v(-149, -74) * mm, "radius": 1.5 * mm});
            skCircle(sketch, "E45.54.38.0", {"center": v(106, -74) * mm, "radius": 1.5 * mm});
            skCircle(sketch, "E45.56.38.0", {"center": v(-94, -74) * mm, "radius": 1.5 * mm});
            skCircle(sketch, "E45.58.38.0", {"center": v(-129, -74) * mm, "radius": 1.5 * mm});
            skCircle(sketch, "E45.60.38.0", {"center": v(-19, -74) * mm, "radius": 1.5 * mm});
            skCircle(sketch, "E45.62.38.0", {"center": v(-49, -74) * mm, "radius": 1.5 * mm});
            skCircle(sketch, "E45.64.38.0", {"center": v(26, -74) * mm, "radius": 1.5 * mm});
            skCircle(sketch, "E45.66.38.0", {"center": v(61, -74) * mm, "radius": 1.5 * mm});
            skCircle(sketch, "E45.68.38.0", {"center": v(16, -74) * mm, "radius": 1.5 * mm});
            skCircle(sketch, "E45.70.38.0", {"center": v(96, -74) * mm, "radius": 1.5 * mm});
            skCircle(sketch, "E45.72.38.0", {"center": v(-139, -74) * mm, "radius": 1.5 * mm});
            skCircle(sketch, "E45.74.38.0", {"center": v(-59, -74) * mm, "radius": 1.5 * mm});
            skCircle(sketch, "E45.76.38.0", {"center": v(111, -74) * mm, "radius": 1.5 * mm});
            skCircle(sketch, "E45.78.38.0", {"center": v(146, -74) * mm, "radius": 1.5 * mm});
            skCircle(sketch, "E45.80.38.0", {"center": v(-89, -74) * mm, "radius": 1.5 * mm});
            skCircle(sketch, "E45.82.38.0", {"center": v(-44, -74) * mm, "radius": 1.5 * mm});
            skCircle(sketch, "E45.84.38.0", {"center": v(-124, -74) * mm, "radius": 1.5 * mm});
            skCircle(sketch, "E45.86.38.0", {"center": v(-14, -74) * mm, "radius": 1.5 * mm});
            skCircle(sketch, "E45.88.38.0", {"center": v(31, -74) * mm, "radius": 1.5 * mm});
            skCircle(sketch, "E45.90.38.0", {"center": v(66, -74) * mm, "radius": 1.5 * mm});
            skCircle(sketch, "E45.92.38.0", {"center": v(141, -74) * mm, "radius": 1.5 * mm});
            skCircle(sketch, "E45.94.38.0", {"center": v(36, -74) * mm, "radius": 1.5 * mm});
            skCircle(sketch, "E45.96.38.0", {"center": v(-39, -74) * mm, "radius": 1.5 * mm});
            skCircle(sketch, "E45.98.38.0", {"center": v(-119, -74) * mm, "radius": 1.5 * mm});
            skCircle(sketch, "E45.100.38.0", {"center": v(-79, -74) * mm, "radius": 1.5 * mm});
            skCircle(sketch, "E45.102.38.0", {"center": v(-159, -74) * mm, "radius": 1.5 * mm});
            skCircle(sketch, "E45.104.38.0", {"center": v(156, -74) * mm, "radius": 1.5 * mm});
            skCircle(sketch, "E45.106.38.0", {"center": v(76, -74) * mm, "radius": 1.5 * mm});
            skCircle(sketch, "E45.108.38.0", {"center": v(-4, -74) * mm, "radius": 1.5 * mm});
            skCircle(sketch, "E45.110.38.0", {"center": v(41, -74) * mm, "radius": 1.5 * mm});
            skCircle(sketch, "E45.112.38.0", {"center": v(-34, -74) * mm, "radius": 1.5 * mm});
            skCircle(sketch, "E45.114.38.0", {"center": v(-114, -74) * mm, "radius": 1.5 * mm});
            skCircle(sketch, "E45.116.38.0", {"center": v(121, -74) * mm, "radius": 1.5 * mm});
            skCircle(sketch, "E45.118.38.0", {"center": v(-74, -74) * mm, "radius": 1.5 * mm});
            skCircle(sketch, "E45.120.38.0", {"center": v(-154, -74) * mm, "radius": 1.5 * mm});
            skCircle(sketch, "E45.122.38.0", {"center": v(161, -74) * mm, "radius": 1.5 * mm});
            skCircle(sketch, "E45.124.38.0", {"center": v(81, -74) * mm, "radius": 1.5 * mm});
            skCircle(sketch, "E45.126.38.0", {"center": v(1, -74) * mm, "radius": 1.5 * mm});
            skCircle(sketch, "E45.128.38.0", {"center": v(46, -74) * mm, "radius": 1.5 * mm});
            skCircle(sketch, "E45.130.38.0", {"center": v(-29, -74) * mm, "radius": 1.5 * mm});
            skCircle(sketch, "E45.132.38.0", {"center": v(-109, -74) * mm, "radius": 1.5 * mm});
            skCircle(sketch, "E45.134.38.0", {"center": v(126, -74) * mm, "radius": 1.5 * mm});
            skLineSegment(sketch, "E45.136.38.0", {"start": v(-174, -74) * mm, "end": v(-169, -74) * mm, "construction": true});
            skCircle(sketch, "E45.139.38.0", {"center": v(-174, -74) * mm, "radius": 1.5 * mm});
            skCircle(sketch, "E45.141.38.0", {"center": v(-169, -74) * mm, "radius": 1.5 * mm});
            skCircle(sketch, "E45.0.39.0", {"center": v(166, -79) * mm, "radius": 1.5 * mm});
            skCircle(sketch, "E45.2.39.0", {"center": v(21, -79) * mm, "radius": 1.5 * mm});
            skCircle(sketch, "E45.4.39.0", {"center": v(-99, -79) * mm, "radius": 1.5 * mm});
            skCircle(sketch, "E45.6.39.0", {"center": v(6, -79) * mm, "radius": 1.5 * mm});
            skCircle(sketch, "E45.8.39.0", {"center": v(-54, -79) * mm, "radius": 1.5 * mm});
            skCircle(sketch, "E45.10.39.0", {"center": v(171, -79) * mm, "radius": 1.5 * mm});
            skCircle(sketch, "E45.12.39.0", {"center": v(-104, -79) * mm, "radius": 1.5 * mm});
            skCircle(sketch, "E45.14.39.0", {"center": v(11, -79) * mm, "radius": 1.5 * mm});
            skCircle(sketch, "E45.16.39.0", {"center": v(56, -79) * mm, "radius": 1.5 * mm});
            skCircle(sketch, "E45.18.39.0", {"center": v(-134, -79) * mm, "radius": 1.5 * mm});
            skCircle(sketch, "E45.20.39.0", {"center": v(51, -79) * mm, "radius": 1.5 * mm});
            skCircle(sketch, "E45.22.39.0", {"center": v(131, -79) * mm, "radius": 1.5 * mm});
            skCircle(sketch, "E45.24.39.0", {"center": v(151, -79) * mm, "radius": 1.5 * mm});
            skCircle(sketch, "E45.26.39.0", {"center": v(-24, -79) * mm, "radius": 1.5 * mm});
            skCircle(sketch, "E45.28.39.0", {"center": v(-64, -79) * mm, "radius": 1.5 * mm});
            skCircle(sketch, "E45.30.39.0", {"center": v(-9, -79) * mm, "radius": 1.5 * mm});
            skCircle(sketch, "E45.32.39.0", {"center": v(136, -79) * mm, "radius": 1.5 * mm});
            skCircle(sketch, "E45.34.39.0", {"center": v(91, -79) * mm, "radius": 1.5 * mm});
            skCircle(sketch, "E45.36.39.0", {"center": v(101, -79) * mm, "radius": 1.5 * mm});
            skCircle(sketch, "E45.38.39.0", {"center": v(-144, -79) * mm, "radius": 1.5 * mm});
            skCircle(sketch, "E45.40.39.0", {"center": v(71, -79) * mm, "radius": 1.5 * mm});
            skCircle(sketch, "E45.42.39.0", {"center": v(-69, -79) * mm, "radius": 1.5 * mm});
            skCircle(sketch, "E45.44.39.0", {"center": v(-84, -79) * mm, "radius": 1.5 * mm});
            skCircle(sketch, "E45.46.39.0", {"center": v(116, -79) * mm, "radius": 1.5 * mm});
            skCircle(sketch, "E45.50.39.0", {"center": v(86, -79) * mm, "radius": 1.5 * mm});
            skCircle(sketch, "E45.52.39.0", {"center": v(-149, -79) * mm, "radius": 1.5 * mm});
            skCircle(sketch, "E45.54.39.0", {"center": v(106, -79) * mm, "radius": 1.5 * mm});
            skCircle(sketch, "E45.56.39.0", {"center": v(-94, -79) * mm, "radius": 1.5 * mm});
            skCircle(sketch, "E45.58.39.0", {"center": v(-129, -79) * mm, "radius": 1.5 * mm});
            skCircle(sketch, "E45.60.39.0", {"center": v(-19, -79) * mm, "radius": 1.5 * mm});
            skCircle(sketch, "E45.62.39.0", {"center": v(-49, -79) * mm, "radius": 1.5 * mm});
            skCircle(sketch, "E45.64.39.0", {"center": v(26, -79) * mm, "radius": 1.5 * mm});
            skCircle(sketch, "E45.66.39.0", {"center": v(61, -79) * mm, "radius": 1.5 * mm});
            skCircle(sketch, "E45.68.39.0", {"center": v(16, -79) * mm, "radius": 1.5 * mm});
            skCircle(sketch, "E45.70.39.0", {"center": v(96, -79) * mm, "radius": 1.5 * mm});
            skCircle(sketch, "E45.72.39.0", {"center": v(-139, -79) * mm, "radius": 1.5 * mm});
            skCircle(sketch, "E45.74.39.0", {"center": v(-59, -79) * mm, "radius": 1.5 * mm});
            skCircle(sketch, "E45.76.39.0", {"center": v(111, -79) * mm, "radius": 1.5 * mm});
            skCircle(sketch, "E45.78.39.0", {"center": v(146, -79) * mm, "radius": 1.5 * mm});
            skCircle(sketch, "E45.80.39.0", {"center": v(-89, -79) * mm, "radius": 1.5 * mm});
            skCircle(sketch, "E45.82.39.0", {"center": v(-44, -79) * mm, "radius": 1.5 * mm});
            skCircle(sketch, "E45.84.39.0", {"center": v(-124, -79) * mm, "radius": 1.5 * mm});
            skCircle(sketch, "E45.86.39.0", {"center": v(-14, -79) * mm, "radius": 1.5 * mm});
            skCircle(sketch, "E45.88.39.0", {"center": v(31, -79) * mm, "radius": 1.5 * mm});
            skCircle(sketch, "E45.90.39.0", {"center": v(66, -79) * mm, "radius": 1.5 * mm});
            skCircle(sketch, "E45.92.39.0", {"center": v(141, -79) * mm, "radius": 1.5 * mm});
            skCircle(sketch, "E45.94.39.0", {"center": v(36, -79) * mm, "radius": 1.5 * mm});
            skCircle(sketch, "E45.96.39.0", {"center": v(-39, -79) * mm, "radius": 1.5 * mm});
            skCircle(sketch, "E45.98.39.0", {"center": v(-119, -79) * mm, "radius": 1.5 * mm});
            skCircle(sketch, "E45.100.39.0", {"center": v(-79, -79) * mm, "radius": 1.5 * mm});
            skCircle(sketch, "E45.104.39.0", {"center": v(156, -79) * mm, "radius": 1.5 * mm});
            skCircle(sketch, "E45.106.39.0", {"center": v(76, -79) * mm, "radius": 1.5 * mm});
            skCircle(sketch, "E45.108.39.0", {"center": v(-4, -79) * mm, "radius": 1.5 * mm});
            skCircle(sketch, "E45.110.39.0", {"center": v(41, -79) * mm, "radius": 1.5 * mm});
            skCircle(sketch, "E45.112.39.0", {"center": v(-34, -79) * mm, "radius": 1.5 * mm});
            skCircle(sketch, "E45.114.39.0", {"center": v(-114, -79) * mm, "radius": 1.5 * mm});
            skCircle(sketch, "E45.116.39.0", {"center": v(121, -79) * mm, "radius": 1.5 * mm});
            skCircle(sketch, "E45.118.39.0", {"center": v(-74, -79) * mm, "radius": 1.5 * mm});
            skCircle(sketch, "E45.120.39.0", {"center": v(-154, -79) * mm, "radius": 1.5 * mm});
            skCircle(sketch, "E45.122.39.0", {"center": v(161, -79) * mm, "radius": 1.5 * mm});
            skCircle(sketch, "E45.124.39.0", {"center": v(81, -79) * mm, "radius": 1.5 * mm});
            skCircle(sketch, "E45.126.39.0", {"center": v(1, -79) * mm, "radius": 1.5 * mm});
            skCircle(sketch, "E45.128.39.0", {"center": v(46, -79) * mm, "radius": 1.5 * mm});
            skCircle(sketch, "E45.130.39.0", {"center": v(-29, -79) * mm, "radius": 1.5 * mm});
            skCircle(sketch, "E45.132.39.0", {"center": v(-109, -79) * mm, "radius": 1.5 * mm});
            skCircle(sketch, "E45.134.39.0", {"center": v(126, -79) * mm, "radius": 1.5 * mm});
            skCircle(sketch, "E45.0.40.0", {"center": v(166, -84) * mm, "radius": 1.5 * mm});
            skCircle(sketch, "E45.2.40.0", {"center": v(21, -84) * mm, "radius": 1.5 * mm});
            skCircle(sketch, "E45.4.40.0", {"center": v(-99, -84) * mm, "radius": 1.5 * mm});
            skCircle(sketch, "E45.6.40.0", {"center": v(6, -84) * mm, "radius": 1.5 * mm});
            skCircle(sketch, "E45.8.40.0", {"center": v(-54, -84) * mm, "radius": 1.5 * mm});
            skCircle(sketch, "E45.10.40.0", {"center": v(171, -84) * mm, "radius": 1.5 * mm});
            skCircle(sketch, "E45.12.40.0", {"center": v(-104, -84) * mm, "radius": 1.5 * mm});
            skCircle(sketch, "E45.14.40.0", {"center": v(11, -84) * mm, "radius": 1.5 * mm});
            skCircle(sketch, "E45.16.40.0", {"center": v(56, -84) * mm, "radius": 1.5 * mm});
            skCircle(sketch, "E45.18.40.0", {"center": v(-134, -84) * mm, "radius": 1.5 * mm});
            skCircle(sketch, "E45.20.40.0", {"center": v(51, -84) * mm, "radius": 1.5 * mm});
            skCircle(sketch, "E45.22.40.0", {"center": v(131, -84) * mm, "radius": 1.5 * mm});
            skCircle(sketch, "E45.24.40.0", {"center": v(151, -84) * mm, "radius": 1.5 * mm});
            skCircle(sketch, "E45.26.40.0", {"center": v(-24, -84) * mm, "radius": 1.5 * mm});
            skCircle(sketch, "E45.28.40.0", {"center": v(-64, -84) * mm, "radius": 1.5 * mm});
            skCircle(sketch, "E45.30.40.0", {"center": v(-9, -84) * mm, "radius": 1.5 * mm});
            skCircle(sketch, "E45.32.40.0", {"center": v(136, -84) * mm, "radius": 1.5 * mm});
            skCircle(sketch, "E45.34.40.0", {"center": v(91, -84) * mm, "radius": 1.5 * mm});
            skCircle(sketch, "E45.36.40.0", {"center": v(101, -84) * mm, "radius": 1.5 * mm});
            skCircle(sketch, "E45.38.40.0", {"center": v(-144, -84) * mm, "radius": 1.5 * mm});
            skCircle(sketch, "E45.40.40.0", {"center": v(71, -84) * mm, "radius": 1.5 * mm});
            skCircle(sketch, "E45.42.40.0", {"center": v(-69, -84) * mm, "radius": 1.5 * mm});
            skCircle(sketch, "E45.44.40.0", {"center": v(-84, -84) * mm, "radius": 1.5 * mm});
            skCircle(sketch, "E45.46.40.0", {"center": v(116, -84) * mm, "radius": 1.5 * mm});
            skCircle(sketch, "E45.50.40.0", {"center": v(86, -84) * mm, "radius": 1.5 * mm});
            skCircle(sketch, "E45.52.40.0", {"center": v(-149, -84) * mm, "radius": 1.5 * mm});
            skCircle(sketch, "E45.54.40.0", {"center": v(106, -84) * mm, "radius": 1.5 * mm});
            skCircle(sketch, "E45.56.40.0", {"center": v(-94, -84) * mm, "radius": 1.5 * mm});
            skCircle(sketch, "E45.58.40.0", {"center": v(-129, -84) * mm, "radius": 1.5 * mm});
            skCircle(sketch, "E45.60.40.0", {"center": v(-19, -84) * mm, "radius": 1.5 * mm});
            skCircle(sketch, "E45.62.40.0", {"center": v(-49, -84) * mm, "radius": 1.5 * mm});
            skCircle(sketch, "E45.64.40.0", {"center": v(26, -84) * mm, "radius": 1.5 * mm});
            skCircle(sketch, "E45.66.40.0", {"center": v(61, -84) * mm, "radius": 1.5 * mm});
            skCircle(sketch, "E45.68.40.0", {"center": v(16, -84) * mm, "radius": 1.5 * mm});
            skCircle(sketch, "E45.70.40.0", {"center": v(96, -84) * mm, "radius": 1.5 * mm});
            skCircle(sketch, "E45.72.40.0", {"center": v(-139, -84) * mm, "radius": 1.5 * mm});
            skCircle(sketch, "E45.74.40.0", {"center": v(-59, -84) * mm, "radius": 1.5 * mm});
            skCircle(sketch, "E45.76.40.0", {"center": v(111, -84) * mm, "radius": 1.5 * mm});
            skCircle(sketch, "E45.78.40.0", {"center": v(146, -84) * mm, "radius": 1.5 * mm});
            skCircle(sketch, "E45.80.40.0", {"center": v(-89, -84) * mm, "radius": 1.5 * mm});
            skCircle(sketch, "E45.82.40.0", {"center": v(-44, -84) * mm, "radius": 1.5 * mm});
            skCircle(sketch, "E45.84.40.0", {"center": v(-124, -84) * mm, "radius": 1.5 * mm});
            skCircle(sketch, "E45.86.40.0", {"center": v(-14, -84) * mm, "radius": 1.5 * mm});
            skCircle(sketch, "E45.88.40.0", {"center": v(31, -84) * mm, "radius": 1.5 * mm});
            skCircle(sketch, "E45.90.40.0", {"center": v(66, -84) * mm, "radius": 1.5 * mm});
            skCircle(sketch, "E45.92.40.0", {"center": v(141, -84) * mm, "radius": 1.5 * mm});
            skCircle(sketch, "E45.94.40.0", {"center": v(36, -84) * mm, "radius": 1.5 * mm});
            skCircle(sketch, "E45.96.40.0", {"center": v(-39, -84) * mm, "radius": 1.5 * mm});
            skCircle(sketch, "E45.98.40.0", {"center": v(-119, -84) * mm, "radius": 1.5 * mm});
            skCircle(sketch, "E45.100.40.0", {"center": v(-79, -84) * mm, "radius": 1.5 * mm});
            skCircle(sketch, "E45.104.40.0", {"center": v(156, -84) * mm, "radius": 1.5 * mm});
            skCircle(sketch, "E45.106.40.0", {"center": v(76, -84) * mm, "radius": 1.5 * mm});
            skCircle(sketch, "E45.108.40.0", {"center": v(-4, -84) * mm, "radius": 1.5 * mm});
            skCircle(sketch, "E45.110.40.0", {"center": v(41, -84) * mm, "radius": 1.5 * mm});
            skCircle(sketch, "E45.112.40.0", {"center": v(-34, -84) * mm, "radius": 1.5 * mm});
            skCircle(sketch, "E45.114.40.0", {"center": v(-114, -84) * mm, "radius": 1.5 * mm});
            skCircle(sketch, "E45.116.40.0", {"center": v(121, -84) * mm, "radius": 1.5 * mm});
            skCircle(sketch, "E45.118.40.0", {"center": v(-74, -84) * mm, "radius": 1.5 * mm});
            skCircle(sketch, "E45.120.40.0", {"center": v(-154, -84) * mm, "radius": 1.5 * mm});
            skCircle(sketch, "E45.122.40.0", {"center": v(161, -84) * mm, "radius": 1.5 * mm});
            skCircle(sketch, "E45.124.40.0", {"center": v(81, -84) * mm, "radius": 1.5 * mm});
            skCircle(sketch, "E45.126.40.0", {"center": v(1, -84) * mm, "radius": 1.5 * mm});
            skCircle(sketch, "E45.128.40.0", {"center": v(46, -84) * mm, "radius": 1.5 * mm});
            skCircle(sketch, "E45.130.40.0", {"center": v(-29, -84) * mm, "radius": 1.5 * mm});
            skCircle(sketch, "E45.132.40.0", {"center": v(-109, -84) * mm, "radius": 1.5 * mm});
            skCircle(sketch, "E45.134.40.0", {"center": v(126, -84) * mm, "radius": 1.5 * mm});
            skCircle(sketch, "E45.0.41.0", {"center": v(166, -89) * mm, "radius": 1.5 * mm});
            skCircle(sketch, "E45.2.41.0", {"center": v(21, -89) * mm, "radius": 1.5 * mm});
            skCircle(sketch, "E45.4.41.0", {"center": v(-99, -89) * mm, "radius": 1.5 * mm});
            skCircle(sketch, "E45.6.41.0", {"center": v(6, -89) * mm, "radius": 1.5 * mm});
            skCircle(sketch, "E45.8.41.0", {"center": v(-54, -89) * mm, "radius": 1.5 * mm});
            skCircle(sketch, "E45.10.41.0", {"center": v(171, -89) * mm, "radius": 1.5 * mm});
            skCircle(sketch, "E45.12.41.0", {"center": v(-104, -89) * mm, "radius": 1.5 * mm});
            skCircle(sketch, "E45.14.41.0", {"center": v(11, -89) * mm, "radius": 1.5 * mm});
            skCircle(sketch, "E45.16.41.0", {"center": v(56, -89) * mm, "radius": 1.5 * mm});
            skCircle(sketch, "E45.18.41.0", {"center": v(-134, -89) * mm, "radius": 1.5 * mm});
            skCircle(sketch, "E45.20.41.0", {"center": v(51, -89) * mm, "radius": 1.5 * mm});
            skCircle(sketch, "E45.22.41.0", {"center": v(131, -89) * mm, "radius": 1.5 * mm});
            skCircle(sketch, "E45.24.41.0", {"center": v(151, -89) * mm, "radius": 1.5 * mm});
            skCircle(sketch, "E45.26.41.0", {"center": v(-24, -89) * mm, "radius": 1.5 * mm});
            skCircle(sketch, "E45.28.41.0", {"center": v(-64, -89) * mm, "radius": 1.5 * mm});
            skCircle(sketch, "E45.30.41.0", {"center": v(-9, -89) * mm, "radius": 1.5 * mm});
            skCircle(sketch, "E45.32.41.0", {"center": v(136, -89) * mm, "radius": 1.5 * mm});
            skCircle(sketch, "E45.34.41.0", {"center": v(91, -89) * mm, "radius": 1.5 * mm});
            skCircle(sketch, "E45.36.41.0", {"center": v(101, -89) * mm, "radius": 1.5 * mm});
            skCircle(sketch, "E45.38.41.0", {"center": v(-144, -89) * mm, "radius": 1.5 * mm});
            skCircle(sketch, "E45.40.41.0", {"center": v(71, -89) * mm, "radius": 1.5 * mm});
            skCircle(sketch, "E45.42.41.0", {"center": v(-69, -89) * mm, "radius": 1.5 * mm});
            skCircle(sketch, "E45.44.41.0", {"center": v(-84, -89) * mm, "radius": 1.5 * mm});
            skCircle(sketch, "E45.46.41.0", {"center": v(116, -89) * mm, "radius": 1.5 * mm});
            skCircle(sketch, "E45.50.41.0", {"center": v(86, -89) * mm, "radius": 1.5 * mm});
            skCircle(sketch, "E45.52.41.0", {"center": v(-149, -89) * mm, "radius": 1.5 * mm});
            skCircle(sketch, "E45.54.41.0", {"center": v(106, -89) * mm, "radius": 1.5 * mm});
            skCircle(sketch, "E45.56.41.0", {"center": v(-94, -89) * mm, "radius": 1.5 * mm});
            skCircle(sketch, "E45.58.41.0", {"center": v(-129, -89) * mm, "radius": 1.5 * mm});
            skCircle(sketch, "E45.60.41.0", {"center": v(-19, -89) * mm, "radius": 1.5 * mm});
            skCircle(sketch, "E45.62.41.0", {"center": v(-49, -89) * mm, "radius": 1.5 * mm});
            skCircle(sketch, "E45.64.41.0", {"center": v(26, -89) * mm, "radius": 1.5 * mm});
            skCircle(sketch, "E45.66.41.0", {"center": v(61, -89) * mm, "radius": 1.5 * mm});
            skCircle(sketch, "E45.68.41.0", {"center": v(16, -89) * mm, "radius": 1.5 * mm});
            skCircle(sketch, "E45.70.41.0", {"center": v(96, -89) * mm, "radius": 1.5 * mm});
            skCircle(sketch, "E45.72.41.0", {"center": v(-139, -89) * mm, "radius": 1.5 * mm});
            skCircle(sketch, "E45.74.41.0", {"center": v(-59, -89) * mm, "radius": 1.5 * mm});
            skCircle(sketch, "E45.76.41.0", {"center": v(111, -89) * mm, "radius": 1.5 * mm});
            skCircle(sketch, "E45.78.41.0", {"center": v(146, -89) * mm, "radius": 1.5 * mm});
            skCircle(sketch, "E45.80.41.0", {"center": v(-89, -89) * mm, "radius": 1.5 * mm});
            skCircle(sketch, "E45.82.41.0", {"center": v(-44, -89) * mm, "radius": 1.5 * mm});
            skCircle(sketch, "E45.84.41.0", {"center": v(-124, -89) * mm, "radius": 1.5 * mm});
            skCircle(sketch, "E45.86.41.0", {"center": v(-14, -89) * mm, "radius": 1.5 * mm});
            skCircle(sketch, "E45.88.41.0", {"center": v(31, -89) * mm, "radius": 1.5 * mm});
            skCircle(sketch, "E45.90.41.0", {"center": v(66, -89) * mm, "radius": 1.5 * mm});
            skCircle(sketch, "E45.92.41.0", {"center": v(141, -89) * mm, "radius": 1.5 * mm});
            skCircle(sketch, "E45.94.41.0", {"center": v(36, -89) * mm, "radius": 1.5 * mm});
            skCircle(sketch, "E45.96.41.0", {"center": v(-39, -89) * mm, "radius": 1.5 * mm});
            skCircle(sketch, "E45.98.41.0", {"center": v(-119, -89) * mm, "radius": 1.5 * mm});
            skCircle(sketch, "E45.100.41.0", {"center": v(-79, -89) * mm, "radius": 1.5 * mm});
            skCircle(sketch, "E45.104.41.0", {"center": v(156, -89) * mm, "radius": 1.5 * mm});
            skCircle(sketch, "E45.106.41.0", {"center": v(76, -89) * mm, "radius": 1.5 * mm});
            skCircle(sketch, "E45.108.41.0", {"center": v(-4, -89) * mm, "radius": 1.5 * mm});
            skCircle(sketch, "E45.110.41.0", {"center": v(41, -89) * mm, "radius": 1.5 * mm});
            skCircle(sketch, "E45.112.41.0", {"center": v(-34, -89) * mm, "radius": 1.5 * mm});
            skCircle(sketch, "E45.114.41.0", {"center": v(-114, -89) * mm, "radius": 1.5 * mm});
            skCircle(sketch, "E45.116.41.0", {"center": v(121, -89) * mm, "radius": 1.5 * mm});
            skCircle(sketch, "E45.118.41.0", {"center": v(-74, -89) * mm, "radius": 1.5 * mm});
            skCircle(sketch, "E45.120.41.0", {"center": v(-154, -89) * mm, "radius": 1.5 * mm});
            skCircle(sketch, "E45.122.41.0", {"center": v(161, -89) * mm, "radius": 1.5 * mm});
            skCircle(sketch, "E45.124.41.0", {"center": v(81, -89) * mm, "radius": 1.5 * mm});
            skCircle(sketch, "E45.126.41.0", {"center": v(1, -89) * mm, "radius": 1.5 * mm});
            skCircle(sketch, "E45.128.41.0", {"center": v(46, -89) * mm, "radius": 1.5 * mm});
            skCircle(sketch, "E45.130.41.0", {"center": v(-29, -89) * mm, "radius": 1.5 * mm});
            skCircle(sketch, "E45.132.41.0", {"center": v(-109, -89) * mm, "radius": 1.5 * mm});
            skCircle(sketch, "E45.134.41.0", {"center": v(126, -89) * mm, "radius": 1.5 * mm});
            skCircle(sketch, "E45.0.42.0", {"center": v(166, -94) * mm, "radius": 1.5 * mm});
            skCircle(sketch, "E45.2.42.0", {"center": v(21, -94) * mm, "radius": 1.5 * mm});
            skCircle(sketch, "E45.4.42.0", {"center": v(-99, -94) * mm, "radius": 1.5 * mm});
            skCircle(sketch, "E45.6.42.0", {"center": v(6, -94) * mm, "radius": 1.5 * mm});
            skCircle(sketch, "E45.8.42.0", {"center": v(-54, -94) * mm, "radius": 1.5 * mm});
            skCircle(sketch, "E45.10.42.0", {"center": v(171, -94) * mm, "radius": 1.5 * mm});
            skCircle(sketch, "E45.12.42.0", {"center": v(-104, -94) * mm, "radius": 1.5 * mm});
            skCircle(sketch, "E45.14.42.0", {"center": v(11, -94) * mm, "radius": 1.5 * mm});
            skCircle(sketch, "E45.16.42.0", {"center": v(56, -94) * mm, "radius": 1.5 * mm});
            skCircle(sketch, "E45.18.42.0", {"center": v(-134, -94) * mm, "radius": 1.5 * mm});
            skCircle(sketch, "E45.20.42.0", {"center": v(51, -94) * mm, "radius": 1.5 * mm});
            skCircle(sketch, "E45.22.42.0", {"center": v(131, -94) * mm, "radius": 1.5 * mm});
            skCircle(sketch, "E45.24.42.0", {"center": v(151, -94) * mm, "radius": 1.5 * mm});
            skCircle(sketch, "E45.26.42.0", {"center": v(-24, -94) * mm, "radius": 1.5 * mm});
            skCircle(sketch, "E45.28.42.0", {"center": v(-64, -94) * mm, "radius": 1.5 * mm});
            skCircle(sketch, "E45.30.42.0", {"center": v(-9, -94) * mm, "radius": 1.5 * mm});
            skCircle(sketch, "E45.32.42.0", {"center": v(136, -94) * mm, "radius": 1.5 * mm});
            skCircle(sketch, "E45.34.42.0", {"center": v(91, -94) * mm, "radius": 1.5 * mm});
            skCircle(sketch, "E45.36.42.0", {"center": v(101, -94) * mm, "radius": 1.5 * mm});
            skCircle(sketch, "E45.38.42.0", {"center": v(-144, -94) * mm, "radius": 1.5 * mm});
            skCircle(sketch, "E45.40.42.0", {"center": v(71, -94) * mm, "radius": 1.5 * mm});
            skCircle(sketch, "E45.42.42.0", {"center": v(-69, -94) * mm, "radius": 1.5 * mm});
            skCircle(sketch, "E45.44.42.0", {"center": v(-84, -94) * mm, "radius": 1.5 * mm});
            skCircle(sketch, "E45.46.42.0", {"center": v(116, -94) * mm, "radius": 1.5 * mm});
            skCircle(sketch, "E45.50.42.0", {"center": v(86, -94) * mm, "radius": 1.5 * mm});
            skCircle(sketch, "E45.52.42.0", {"center": v(-149, -94) * mm, "radius": 1.5 * mm});
            skCircle(sketch, "E45.54.42.0", {"center": v(106, -94) * mm, "radius": 1.5 * mm});
            skCircle(sketch, "E45.56.42.0", {"center": v(-94, -94) * mm, "radius": 1.5 * mm});
            skCircle(sketch, "E45.58.42.0", {"center": v(-129, -94) * mm, "radius": 1.5 * mm});
            skCircle(sketch, "E45.60.42.0", {"center": v(-19, -94) * mm, "radius": 1.5 * mm});
            skCircle(sketch, "E45.62.42.0", {"center": v(-49, -94) * mm, "radius": 1.5 * mm});
            skCircle(sketch, "E45.64.42.0", {"center": v(26, -94) * mm, "radius": 1.5 * mm});
            skCircle(sketch, "E45.66.42.0", {"center": v(61, -94) * mm, "radius": 1.5 * mm});
            skCircle(sketch, "E45.68.42.0", {"center": v(16, -94) * mm, "radius": 1.5 * mm});
            skCircle(sketch, "E45.70.42.0", {"center": v(96, -94) * mm, "radius": 1.5 * mm});
            skCircle(sketch, "E45.72.42.0", {"center": v(-139, -94) * mm, "radius": 1.5 * mm});
            skCircle(sketch, "E45.74.42.0", {"center": v(-59, -94) * mm, "radius": 1.5 * mm});
            skCircle(sketch, "E45.76.42.0", {"center": v(111, -94) * mm, "radius": 1.5 * mm});
            skCircle(sketch, "E45.78.42.0", {"center": v(146, -94) * mm, "radius": 1.5 * mm});
            skCircle(sketch, "E45.80.42.0", {"center": v(-89, -94) * mm, "radius": 1.5 * mm});
            skCircle(sketch, "E45.82.42.0", {"center": v(-44, -94) * mm, "radius": 1.5 * mm});
            skCircle(sketch, "E45.84.42.0", {"center": v(-124, -94) * mm, "radius": 1.5 * mm});
            skCircle(sketch, "E45.86.42.0", {"center": v(-14, -94) * mm, "radius": 1.5 * mm});
            skCircle(sketch, "E45.88.42.0", {"center": v(31, -94) * mm, "radius": 1.5 * mm});
            skCircle(sketch, "E45.90.42.0", {"center": v(66, -94) * mm, "radius": 1.5 * mm});
            skCircle(sketch, "E45.92.42.0", {"center": v(141, -94) * mm, "radius": 1.5 * mm});
            skCircle(sketch, "E45.94.42.0", {"center": v(36, -94) * mm, "radius": 1.5 * mm});
            skCircle(sketch, "E45.96.42.0", {"center": v(-39, -94) * mm, "radius": 1.5 * mm});
            skCircle(sketch, "E45.98.42.0", {"center": v(-119, -94) * mm, "radius": 1.5 * mm});
            skCircle(sketch, "E45.100.42.0", {"center": v(-79, -94) * mm, "radius": 1.5 * mm});
            skCircle(sketch, "E45.104.42.0", {"center": v(156, -94) * mm, "radius": 1.5 * mm});
            skCircle(sketch, "E45.106.42.0", {"center": v(76, -94) * mm, "radius": 1.5 * mm});
            skCircle(sketch, "E45.108.42.0", {"center": v(-4, -94) * mm, "radius": 1.5 * mm});
            skCircle(sketch, "E45.110.42.0", {"center": v(41, -94) * mm, "radius": 1.5 * mm});
            skCircle(sketch, "E45.112.42.0", {"center": v(-34, -94) * mm, "radius": 1.5 * mm});
            skCircle(sketch, "E45.114.42.0", {"center": v(-114, -94) * mm, "radius": 1.5 * mm});
            skCircle(sketch, "E45.116.42.0", {"center": v(121, -94) * mm, "radius": 1.5 * mm});
            skCircle(sketch, "E45.118.42.0", {"center": v(-74, -94) * mm, "radius": 1.5 * mm});
            skCircle(sketch, "E45.122.42.0", {"center": v(161, -94) * mm, "radius": 1.5 * mm});
            skCircle(sketch, "E45.124.42.0", {"center": v(81, -94) * mm, "radius": 1.5 * mm});
            skCircle(sketch, "E45.126.42.0", {"center": v(1, -94) * mm, "radius": 1.5 * mm});
            skCircle(sketch, "E45.128.42.0", {"center": v(46, -94) * mm, "radius": 1.5 * mm});
            skCircle(sketch, "E45.130.42.0", {"center": v(-29, -94) * mm, "radius": 1.5 * mm});
            skCircle(sketch, "E45.132.42.0", {"center": v(-109, -94) * mm, "radius": 1.5 * mm});
            skCircle(sketch, "E45.134.42.0", {"center": v(126, -94) * mm, "radius": 1.5 * mm});
            skCircle(sketch, "E45.0.43.0", {"center": v(166, -99) * mm, "radius": 1.5 * mm});
            skCircle(sketch, "E45.2.43.0", {"center": v(21, -99) * mm, "radius": 1.5 * mm});
            skCircle(sketch, "E45.4.43.0", {"center": v(-99, -99) * mm, "radius": 1.5 * mm});
            skCircle(sketch, "E45.6.43.0", {"center": v(6, -99) * mm, "radius": 1.5 * mm});
            skCircle(sketch, "E45.8.43.0", {"center": v(-54, -99) * mm, "radius": 1.5 * mm});
            skCircle(sketch, "E45.10.43.0", {"center": v(171, -99) * mm, "radius": 1.5 * mm});
            skCircle(sketch, "E45.12.43.0", {"center": v(-104, -99) * mm, "radius": 1.5 * mm});
            skCircle(sketch, "E45.14.43.0", {"center": v(11, -99) * mm, "radius": 1.5 * mm});
            skCircle(sketch, "E45.16.43.0", {"center": v(56, -99) * mm, "radius": 1.5 * mm});
            skCircle(sketch, "E45.18.43.0", {"center": v(-134, -99) * mm, "radius": 1.5 * mm});
            skCircle(sketch, "E45.20.43.0", {"center": v(51, -99) * mm, "radius": 1.5 * mm});
            skCircle(sketch, "E45.22.43.0", {"center": v(131, -99) * mm, "radius": 1.5 * mm});
            skCircle(sketch, "E45.24.43.0", {"center": v(151, -99) * mm, "radius": 1.5 * mm});
            skCircle(sketch, "E45.26.43.0", {"center": v(-24, -99) * mm, "radius": 1.5 * mm});
            skCircle(sketch, "E45.28.43.0", {"center": v(-64, -99) * mm, "radius": 1.5 * mm});
            skCircle(sketch, "E45.30.43.0", {"center": v(-9, -99) * mm, "radius": 1.5 * mm});
            skCircle(sketch, "E45.32.43.0", {"center": v(136, -99) * mm, "radius": 1.5 * mm});
            skCircle(sketch, "E45.34.43.0", {"center": v(91, -99) * mm, "radius": 1.5 * mm});
            skCircle(sketch, "E45.36.43.0", {"center": v(101, -99) * mm, "radius": 1.5 * mm});
            skCircle(sketch, "E45.38.43.0", {"center": v(-144, -99) * mm, "radius": 1.5 * mm});
            skCircle(sketch, "E45.40.43.0", {"center": v(71, -99) * mm, "radius": 1.5 * mm});
            skCircle(sketch, "E45.42.43.0", {"center": v(-69, -99) * mm, "radius": 1.5 * mm});
            skCircle(sketch, "E45.44.43.0", {"center": v(-84, -99) * mm, "radius": 1.5 * mm});
            skCircle(sketch, "E45.46.43.0", {"center": v(116, -99) * mm, "radius": 1.5 * mm});
            skCircle(sketch, "E45.50.43.0", {"center": v(86, -99) * mm, "radius": 1.5 * mm});
            skCircle(sketch, "E45.52.43.0", {"center": v(-149, -99) * mm, "radius": 1.5 * mm});
            skCircle(sketch, "E45.54.43.0", {"center": v(106, -99) * mm, "radius": 1.5 * mm});
            skCircle(sketch, "E45.56.43.0", {"center": v(-94, -99) * mm, "radius": 1.5 * mm});
            skCircle(sketch, "E45.58.43.0", {"center": v(-129, -99) * mm, "radius": 1.5 * mm});
            skCircle(sketch, "E45.60.43.0", {"center": v(-19, -99) * mm, "radius": 1.5 * mm});
            skCircle(sketch, "E45.62.43.0", {"center": v(-49, -99) * mm, "radius": 1.5 * mm});
            skCircle(sketch, "E45.64.43.0", {"center": v(26, -99) * mm, "radius": 1.5 * mm});
            skCircle(sketch, "E45.66.43.0", {"center": v(61, -99) * mm, "radius": 1.5 * mm});
            skCircle(sketch, "E45.68.43.0", {"center": v(16, -99) * mm, "radius": 1.5 * mm});
            skCircle(sketch, "E45.70.43.0", {"center": v(96, -99) * mm, "radius": 1.5 * mm});
            skCircle(sketch, "E45.72.43.0", {"center": v(-139, -99) * mm, "radius": 1.5 * mm});
            skCircle(sketch, "E45.74.43.0", {"center": v(-59, -99) * mm, "radius": 1.5 * mm});
            skCircle(sketch, "E45.76.43.0", {"center": v(111, -99) * mm, "radius": 1.5 * mm});
            skCircle(sketch, "E45.78.43.0", {"center": v(146, -99) * mm, "radius": 1.5 * mm});
            skCircle(sketch, "E45.80.43.0", {"center": v(-89, -99) * mm, "radius": 1.5 * mm});
            skCircle(sketch, "E45.82.43.0", {"center": v(-44, -99) * mm, "radius": 1.5 * mm});
            skCircle(sketch, "E45.84.43.0", {"center": v(-124, -99) * mm, "radius": 1.5 * mm});
            skCircle(sketch, "E45.86.43.0", {"center": v(-14, -99) * mm, "radius": 1.5 * mm});
            skCircle(sketch, "E45.88.43.0", {"center": v(31, -99) * mm, "radius": 1.5 * mm});
            skCircle(sketch, "E45.90.43.0", {"center": v(66, -99) * mm, "radius": 1.5 * mm});
            skCircle(sketch, "E45.92.43.0", {"center": v(141, -99) * mm, "radius": 1.5 * mm});
            skCircle(sketch, "E45.94.43.0", {"center": v(36, -99) * mm, "radius": 1.5 * mm});
            skCircle(sketch, "E45.96.43.0", {"center": v(-39, -99) * mm, "radius": 1.5 * mm});
            skCircle(sketch, "E45.98.43.0", {"center": v(-119, -99) * mm, "radius": 1.5 * mm});
            skCircle(sketch, "E45.100.43.0", {"center": v(-79, -99) * mm, "radius": 1.5 * mm});
            skCircle(sketch, "E45.104.43.0", {"center": v(156, -99) * mm, "radius": 1.5 * mm});
            skCircle(sketch, "E45.106.43.0", {"center": v(76, -99) * mm, "radius": 1.5 * mm});
            skCircle(sketch, "E45.108.43.0", {"center": v(-4, -99) * mm, "radius": 1.5 * mm});
            skCircle(sketch, "E45.110.43.0", {"center": v(41, -99) * mm, "radius": 1.5 * mm});
            skCircle(sketch, "E45.112.43.0", {"center": v(-34, -99) * mm, "radius": 1.5 * mm});
            skCircle(sketch, "E45.114.43.0", {"center": v(-114, -99) * mm, "radius": 1.5 * mm});
            skCircle(sketch, "E45.116.43.0", {"center": v(121, -99) * mm, "radius": 1.5 * mm});
            skCircle(sketch, "E45.118.43.0", {"center": v(-74, -99) * mm, "radius": 1.5 * mm});
            skCircle(sketch, "E45.122.43.0", {"center": v(161, -99) * mm, "radius": 1.5 * mm});
            skCircle(sketch, "E45.124.43.0", {"center": v(81, -99) * mm, "radius": 1.5 * mm});
            skCircle(sketch, "E45.126.43.0", {"center": v(1, -99) * mm, "radius": 1.5 * mm});
            skCircle(sketch, "E45.128.43.0", {"center": v(46, -99) * mm, "radius": 1.5 * mm});
            skCircle(sketch, "E45.130.43.0", {"center": v(-29, -99) * mm, "radius": 1.5 * mm});
            skCircle(sketch, "E45.132.43.0", {"center": v(-109, -99) * mm, "radius": 1.5 * mm});
            skCircle(sketch, "E45.134.43.0", {"center": v(126, -99) * mm, "radius": 1.5 * mm});
            skCircle(sketch, "E45.0.44.0", {"center": v(166, -104) * mm, "radius": 1.5 * mm});
            skCircle(sketch, "E45.2.44.0", {"center": v(21, -104) * mm, "radius": 1.5 * mm});
            skCircle(sketch, "E45.4.44.0", {"center": v(-99, -104) * mm, "radius": 1.5 * mm});
            skCircle(sketch, "E45.6.44.0", {"center": v(6, -104) * mm, "radius": 1.5 * mm});
            skCircle(sketch, "E45.8.44.0", {"center": v(-54, -104) * mm, "radius": 1.5 * mm});
            skCircle(sketch, "E45.10.44.0", {"center": v(171, -104) * mm, "radius": 1.5 * mm});
            skCircle(sketch, "E45.12.44.0", {"center": v(-104, -104) * mm, "radius": 1.5 * mm});
            skCircle(sketch, "E45.14.44.0", {"center": v(11, -104) * mm, "radius": 1.5 * mm});
            skCircle(sketch, "E45.16.44.0", {"center": v(56, -104) * mm, "radius": 1.5 * mm});
            skCircle(sketch, "E45.18.44.0", {"center": v(-134, -104) * mm, "radius": 1.5 * mm});
            skCircle(sketch, "E45.20.44.0", {"center": v(51, -104) * mm, "radius": 1.5 * mm});
            skCircle(sketch, "E45.22.44.0", {"center": v(131, -104) * mm, "radius": 1.5 * mm});
            skCircle(sketch, "E45.24.44.0", {"center": v(151, -104) * mm, "radius": 1.5 * mm});
            skCircle(sketch, "E45.26.44.0", {"center": v(-24, -104) * mm, "radius": 1.5 * mm});
            skCircle(sketch, "E45.28.44.0", {"center": v(-64, -104) * mm, "radius": 1.5 * mm});
            skCircle(sketch, "E45.30.44.0", {"center": v(-9, -104) * mm, "radius": 1.5 * mm});
            skCircle(sketch, "E45.32.44.0", {"center": v(136, -104) * mm, "radius": 1.5 * mm});
            skCircle(sketch, "E45.34.44.0", {"center": v(91, -104) * mm, "radius": 1.5 * mm});
            skCircle(sketch, "E45.36.44.0", {"center": v(101, -104) * mm, "radius": 1.5 * mm});
            skCircle(sketch, "E45.38.44.0", {"center": v(-144, -104) * mm, "radius": 1.5 * mm});
            skCircle(sketch, "E45.40.44.0", {"center": v(71, -104) * mm, "radius": 1.5 * mm});
            skCircle(sketch, "E45.42.44.0", {"center": v(-69, -104) * mm, "radius": 1.5 * mm});
            skCircle(sketch, "E45.44.44.0", {"center": v(-84, -104) * mm, "radius": 1.5 * mm});
            skCircle(sketch, "E45.46.44.0", {"center": v(116, -104) * mm, "radius": 1.5 * mm});
            skCircle(sketch, "E45.50.44.0", {"center": v(86, -104) * mm, "radius": 1.5 * mm});
            skCircle(sketch, "E45.52.44.0", {"center": v(-149, -104) * mm, "radius": 1.5 * mm});
            skCircle(sketch, "E45.54.44.0", {"center": v(106, -104) * mm, "radius": 1.5 * mm});
            skCircle(sketch, "E45.56.44.0", {"center": v(-94, -104) * mm, "radius": 1.5 * mm});
            skCircle(sketch, "E45.58.44.0", {"center": v(-129, -104) * mm, "radius": 1.5 * mm});
            skCircle(sketch, "E45.60.44.0", {"center": v(-19, -104) * mm, "radius": 1.5 * mm});
            skCircle(sketch, "E45.62.44.0", {"center": v(-49, -104) * mm, "radius": 1.5 * mm});
            skCircle(sketch, "E45.64.44.0", {"center": v(26, -104) * mm, "radius": 1.5 * mm});
            skCircle(sketch, "E45.66.44.0", {"center": v(61, -104) * mm, "radius": 1.5 * mm});
            skCircle(sketch, "E45.68.44.0", {"center": v(16, -104) * mm, "radius": 1.5 * mm});
            skCircle(sketch, "E45.70.44.0", {"center": v(96, -104) * mm, "radius": 1.5 * mm});
            skCircle(sketch, "E45.72.44.0", {"center": v(-139, -104) * mm, "radius": 1.5 * mm});
            skCircle(sketch, "E45.74.44.0", {"center": v(-59, -104) * mm, "radius": 1.5 * mm});
            skCircle(sketch, "E45.76.44.0", {"center": v(111, -104) * mm, "radius": 1.5 * mm});
            skCircle(sketch, "E45.78.44.0", {"center": v(146, -104) * mm, "radius": 1.5 * mm});
            skCircle(sketch, "E45.80.44.0", {"center": v(-89, -104) * mm, "radius": 1.5 * mm});
            skCircle(sketch, "E45.82.44.0", {"center": v(-44, -104) * mm, "radius": 1.5 * mm});
            skCircle(sketch, "E45.84.44.0", {"center": v(-124, -104) * mm, "radius": 1.5 * mm});
            skCircle(sketch, "E45.86.44.0", {"center": v(-14, -104) * mm, "radius": 1.5 * mm});
            skCircle(sketch, "E45.88.44.0", {"center": v(31, -104) * mm, "radius": 1.5 * mm});
            skCircle(sketch, "E45.90.44.0", {"center": v(66, -104) * mm, "radius": 1.5 * mm});
            skCircle(sketch, "E45.92.44.0", {"center": v(141, -104) * mm, "radius": 1.5 * mm});
            skCircle(sketch, "E45.94.44.0", {"center": v(36, -104) * mm, "radius": 1.5 * mm});
            skCircle(sketch, "E45.96.44.0", {"center": v(-39, -104) * mm, "radius": 1.5 * mm});
            skCircle(sketch, "E45.98.44.0", {"center": v(-119, -104) * mm, "radius": 1.5 * mm});
            skCircle(sketch, "E45.100.44.0", {"center": v(-79, -104) * mm, "radius": 1.5 * mm});
            skCircle(sketch, "E45.104.44.0", {"center": v(156, -104) * mm, "radius": 1.5 * mm});
            skCircle(sketch, "E45.106.44.0", {"center": v(76, -104) * mm, "radius": 1.5 * mm});
            skCircle(sketch, "E45.108.44.0", {"center": v(-4, -104) * mm, "radius": 1.5 * mm});
            skCircle(sketch, "E45.110.44.0", {"center": v(41, -104) * mm, "radius": 1.5 * mm});
            skCircle(sketch, "E45.112.44.0", {"center": v(-34, -104) * mm, "radius": 1.5 * mm});
            skCircle(sketch, "E45.114.44.0", {"center": v(-114, -104) * mm, "radius": 1.5 * mm});
            skCircle(sketch, "E45.116.44.0", {"center": v(121, -104) * mm, "radius": 1.5 * mm});
            skCircle(sketch, "E45.118.44.0", {"center": v(-74, -104) * mm, "radius": 1.5 * mm});
            skCircle(sketch, "E45.122.44.0", {"center": v(161, -104) * mm, "radius": 1.5 * mm});
            skCircle(sketch, "E45.124.44.0", {"center": v(81, -104) * mm, "radius": 1.5 * mm});
            skCircle(sketch, "E45.126.44.0", {"center": v(1, -104) * mm, "radius": 1.5 * mm});
            skCircle(sketch, "E45.128.44.0", {"center": v(46, -104) * mm, "radius": 1.5 * mm});
            skCircle(sketch, "E45.130.44.0", {"center": v(-29, -104) * mm, "radius": 1.5 * mm});
            skCircle(sketch, "E45.132.44.0", {"center": v(-109, -104) * mm, "radius": 1.5 * mm});
            skCircle(sketch, "E45.134.44.0", {"center": v(126, -104) * mm, "radius": 1.5 * mm});
            skCircle(sketch, "E45.0.45.0", {"center": v(166, -109) * mm, "radius": 1.5 * mm});
            skCircle(sketch, "E45.2.45.0", {"center": v(21, -109) * mm, "radius": 1.5 * mm});
            skCircle(sketch, "E45.4.45.0", {"center": v(-99, -109) * mm, "radius": 1.5 * mm});
            skCircle(sketch, "E45.6.45.0", {"center": v(6, -109) * mm, "radius": 1.5 * mm});
            skCircle(sketch, "E45.8.45.0", {"center": v(-54, -109) * mm, "radius": 1.5 * mm});
            skCircle(sketch, "E45.10.45.0", {"center": v(171, -109) * mm, "radius": 1.5 * mm});
            skCircle(sketch, "E45.12.45.0", {"center": v(-104, -109) * mm, "radius": 1.5 * mm});
            skCircle(sketch, "E45.14.45.0", {"center": v(11, -109) * mm, "radius": 1.5 * mm});
            skCircle(sketch, "E45.16.45.0", {"center": v(56, -109) * mm, "radius": 1.5 * mm});
            skCircle(sketch, "E45.18.45.0", {"center": v(-134, -109) * mm, "radius": 1.5 * mm});
            skCircle(sketch, "E45.20.45.0", {"center": v(51, -109) * mm, "radius": 1.5 * mm});
            skCircle(sketch, "E45.22.45.0", {"center": v(131, -109) * mm, "radius": 1.5 * mm});
            skCircle(sketch, "E45.24.45.0", {"center": v(151, -109) * mm, "radius": 1.5 * mm});
            skCircle(sketch, "E45.26.45.0", {"center": v(-24, -109) * mm, "radius": 1.5 * mm});
            skCircle(sketch, "E45.28.45.0", {"center": v(-64, -109) * mm, "radius": 1.5 * mm});
            skCircle(sketch, "E45.30.45.0", {"center": v(-9, -109) * mm, "radius": 1.5 * mm});
            skCircle(sketch, "E45.32.45.0", {"center": v(136, -109) * mm, "radius": 1.5 * mm});
            skCircle(sketch, "E45.34.45.0", {"center": v(91, -109) * mm, "radius": 1.5 * mm});
            skCircle(sketch, "E45.36.45.0", {"center": v(101, -109) * mm, "radius": 1.5 * mm});
            skCircle(sketch, "E45.38.45.0", {"center": v(-144, -109) * mm, "radius": 1.5 * mm});
            skCircle(sketch, "E45.40.45.0", {"center": v(71, -109) * mm, "radius": 1.5 * mm});
            skCircle(sketch, "E45.42.45.0", {"center": v(-69, -109) * mm, "radius": 1.5 * mm});
            skCircle(sketch, "E45.44.45.0", {"center": v(-84, -109) * mm, "radius": 1.5 * mm});
            skCircle(sketch, "E45.46.45.0", {"center": v(116, -109) * mm, "radius": 1.5 * mm});
            skCircle(sketch, "E45.50.45.0", {"center": v(86, -109) * mm, "radius": 1.5 * mm});
            skCircle(sketch, "E45.52.45.0", {"center": v(-149, -109) * mm, "radius": 1.5 * mm});
            skCircle(sketch, "E45.54.45.0", {"center": v(106, -109) * mm, "radius": 1.5 * mm});
            skCircle(sketch, "E45.56.45.0", {"center": v(-94, -109) * mm, "radius": 1.5 * mm});
            skCircle(sketch, "E45.58.45.0", {"center": v(-129, -109) * mm, "radius": 1.5 * mm});
            skCircle(sketch, "E45.60.45.0", {"center": v(-19, -109) * mm, "radius": 1.5 * mm});
            skCircle(sketch, "E45.62.45.0", {"center": v(-49, -109) * mm, "radius": 1.5 * mm});
            skCircle(sketch, "E45.64.45.0", {"center": v(26, -109) * mm, "radius": 1.5 * mm});
            skCircle(sketch, "E45.66.45.0", {"center": v(61, -109) * mm, "radius": 1.5 * mm});
            skCircle(sketch, "E45.68.45.0", {"center": v(16, -109) * mm, "radius": 1.5 * mm});
            skCircle(sketch, "E45.70.45.0", {"center": v(96, -109) * mm, "radius": 1.5 * mm});
            skCircle(sketch, "E45.72.45.0", {"center": v(-139, -109) * mm, "radius": 1.5 * mm});
            skCircle(sketch, "E45.74.45.0", {"center": v(-59, -109) * mm, "radius": 1.5 * mm});
            skCircle(sketch, "E45.76.45.0", {"center": v(111, -109) * mm, "radius": 1.5 * mm});
            skCircle(sketch, "E45.78.45.0", {"center": v(146, -109) * mm, "radius": 1.5 * mm});
            skCircle(sketch, "E45.80.45.0", {"center": v(-89, -109) * mm, "radius": 1.5 * mm});
            skCircle(sketch, "E45.82.45.0", {"center": v(-44, -109) * mm, "radius": 1.5 * mm});
            skCircle(sketch, "E45.84.45.0", {"center": v(-124, -109) * mm, "radius": 1.5 * mm});
            skCircle(sketch, "E45.86.45.0", {"center": v(-14, -109) * mm, "radius": 1.5 * mm});
            skCircle(sketch, "E45.88.45.0", {"center": v(31, -109) * mm, "radius": 1.5 * mm});
            skCircle(sketch, "E45.90.45.0", {"center": v(66, -109) * mm, "radius": 1.5 * mm});
            skCircle(sketch, "E45.92.45.0", {"center": v(141, -109) * mm, "radius": 1.5 * mm});
            skCircle(sketch, "E45.94.45.0", {"center": v(36, -109) * mm, "radius": 1.5 * mm});
            skCircle(sketch, "E45.96.45.0", {"center": v(-39, -109) * mm, "radius": 1.5 * mm});
            skCircle(sketch, "E45.98.45.0", {"center": v(-119, -109) * mm, "radius": 1.5 * mm});
            skCircle(sketch, "E45.100.45.0", {"center": v(-79, -109) * mm, "radius": 1.5 * mm});
            skCircle(sketch, "E45.104.45.0", {"center": v(156, -109) * mm, "radius": 1.5 * mm});
            skCircle(sketch, "E45.106.45.0", {"center": v(76, -109) * mm, "radius": 1.5 * mm});
            skCircle(sketch, "E45.108.45.0", {"center": v(-4, -109) * mm, "radius": 1.5 * mm});
            skCircle(sketch, "E45.110.45.0", {"center": v(41, -109) * mm, "radius": 1.5 * mm});
            skCircle(sketch, "E45.112.45.0", {"center": v(-34, -109) * mm, "radius": 1.5 * mm});
            skCircle(sketch, "E45.114.45.0", {"center": v(-114, -109) * mm, "radius": 1.5 * mm});
            skCircle(sketch, "E45.116.45.0", {"center": v(121, -109) * mm, "radius": 1.5 * mm});
            skCircle(sketch, "E45.118.45.0", {"center": v(-74, -109) * mm, "radius": 1.5 * mm});
            skCircle(sketch, "E45.122.45.0", {"center": v(161, -109) * mm, "radius": 1.5 * mm});
            skCircle(sketch, "E45.124.45.0", {"center": v(81, -109) * mm, "radius": 1.5 * mm});
            skCircle(sketch, "E45.126.45.0", {"center": v(1, -109) * mm, "radius": 1.5 * mm});
            skCircle(sketch, "E45.128.45.0", {"center": v(46, -109) * mm, "radius": 1.5 * mm});
            skCircle(sketch, "E45.130.45.0", {"center": v(-29, -109) * mm, "radius": 1.5 * mm});
            skCircle(sketch, "E45.132.45.0", {"center": v(-109, -109) * mm, "radius": 1.5 * mm});
            skCircle(sketch, "E45.134.45.0", {"center": v(126, -109) * mm, "radius": 1.5 * mm});
            skCircle(sketch, "E45.0.46.0", {"center": v(166, -114) * mm, "radius": 1.5 * mm});
            skCircle(sketch, "E45.2.46.0", {"center": v(21, -114) * mm, "radius": 1.5 * mm});
            skCircle(sketch, "E45.4.46.0", {"center": v(-99, -114) * mm, "radius": 1.5 * mm});
            skCircle(sketch, "E45.6.46.0", {"center": v(6, -114) * mm, "radius": 1.5 * mm});
            skCircle(sketch, "E45.8.46.0", {"center": v(-54, -114) * mm, "radius": 1.5 * mm});
            skCircle(sketch, "E45.10.46.0", {"center": v(171, -114) * mm, "radius": 1.5 * mm});
            skCircle(sketch, "E45.12.46.0", {"center": v(-104, -114) * mm, "radius": 1.5 * mm});
            skCircle(sketch, "E45.14.46.0", {"center": v(11, -114) * mm, "radius": 1.5 * mm});
            skCircle(sketch, "E45.16.46.0", {"center": v(56, -114) * mm, "radius": 1.5 * mm});
            skCircle(sketch, "E45.18.46.0", {"center": v(-134, -114) * mm, "radius": 1.5 * mm});
            skCircle(sketch, "E45.20.46.0", {"center": v(51, -114) * mm, "radius": 1.5 * mm});
            skCircle(sketch, "E45.22.46.0", {"center": v(131, -114) * mm, "radius": 1.5 * mm});
            skCircle(sketch, "E45.24.46.0", {"center": v(151, -114) * mm, "radius": 1.5 * mm});
            skCircle(sketch, "E45.26.46.0", {"center": v(-24, -114) * mm, "radius": 1.5 * mm});
            skCircle(sketch, "E45.28.46.0", {"center": v(-64, -114) * mm, "radius": 1.5 * mm});
            skCircle(sketch, "E45.30.46.0", {"center": v(-9, -114) * mm, "radius": 1.5 * mm});
            skCircle(sketch, "E45.32.46.0", {"center": v(136, -114) * mm, "radius": 1.5 * mm});
            skCircle(sketch, "E45.34.46.0", {"center": v(91, -114) * mm, "radius": 1.5 * mm});
            skCircle(sketch, "E45.36.46.0", {"center": v(101, -114) * mm, "radius": 1.5 * mm});
            skCircle(sketch, "E45.38.46.0", {"center": v(-144, -114) * mm, "radius": 1.5 * mm});
            skCircle(sketch, "E45.40.46.0", {"center": v(71, -114) * mm, "radius": 1.5 * mm});
            skCircle(sketch, "E45.42.46.0", {"center": v(-69, -114) * mm, "radius": 1.5 * mm});
            skCircle(sketch, "E45.44.46.0", {"center": v(-84, -114) * mm, "radius": 1.5 * mm});
            skCircle(sketch, "E45.46.46.0", {"center": v(116, -114) * mm, "radius": 1.5 * mm});
            skCircle(sketch, "E45.50.46.0", {"center": v(86, -114) * mm, "radius": 1.5 * mm});
            skCircle(sketch, "E45.52.46.0", {"center": v(-149, -114) * mm, "radius": 1.5 * mm});
            skCircle(sketch, "E45.54.46.0", {"center": v(106, -114) * mm, "radius": 1.5 * mm});
            skCircle(sketch, "E45.56.46.0", {"center": v(-94, -114) * mm, "radius": 1.5 * mm});
            skCircle(sketch, "E45.58.46.0", {"center": v(-129, -114) * mm, "radius": 1.5 * mm});
            skCircle(sketch, "E45.60.46.0", {"center": v(-19, -114) * mm, "radius": 1.5 * mm});
            skCircle(sketch, "E45.62.46.0", {"center": v(-49, -114) * mm, "radius": 1.5 * mm});
            skCircle(sketch, "E45.64.46.0", {"center": v(26, -114) * mm, "radius": 1.5 * mm});
            skCircle(sketch, "E45.66.46.0", {"center": v(61, -114) * mm, "radius": 1.5 * mm});
            skCircle(sketch, "E45.68.46.0", {"center": v(16, -114) * mm, "radius": 1.5 * mm});
            skCircle(sketch, "E45.70.46.0", {"center": v(96, -114) * mm, "radius": 1.5 * mm});
            skCircle(sketch, "E45.72.46.0", {"center": v(-139, -114) * mm, "radius": 1.5 * mm});
            skCircle(sketch, "E45.74.46.0", {"center": v(-59, -114) * mm, "radius": 1.5 * mm});
            skCircle(sketch, "E45.76.46.0", {"center": v(111, -114) * mm, "radius": 1.5 * mm});
            skCircle(sketch, "E45.78.46.0", {"center": v(146, -114) * mm, "radius": 1.5 * mm});
            skCircle(sketch, "E45.80.46.0", {"center": v(-89, -114) * mm, "radius": 1.5 * mm});
            skCircle(sketch, "E45.82.46.0", {"center": v(-44, -114) * mm, "radius": 1.5 * mm});
            skCircle(sketch, "E45.84.46.0", {"center": v(-124, -114) * mm, "radius": 1.5 * mm});
            skCircle(sketch, "E45.86.46.0", {"center": v(-14, -114) * mm, "radius": 1.5 * mm});
            skCircle(sketch, "E45.88.46.0", {"center": v(31, -114) * mm, "radius": 1.5 * mm});
            skCircle(sketch, "E45.90.46.0", {"center": v(66, -114) * mm, "radius": 1.5 * mm});
            skCircle(sketch, "E45.92.46.0", {"center": v(141, -114) * mm, "radius": 1.5 * mm});
            skCircle(sketch, "E45.94.46.0", {"center": v(36, -114) * mm, "radius": 1.5 * mm});
            skCircle(sketch, "E45.96.46.0", {"center": v(-39, -114) * mm, "radius": 1.5 * mm});
            skCircle(sketch, "E45.98.46.0", {"center": v(-119, -114) * mm, "radius": 1.5 * mm});
            skCircle(sketch, "E45.100.46.0", {"center": v(-79, -114) * mm, "radius": 1.5 * mm});
            skCircle(sketch, "E45.104.46.0", {"center": v(156, -114) * mm, "radius": 1.5 * mm});
            skCircle(sketch, "E45.106.46.0", {"center": v(76, -114) * mm, "radius": 1.5 * mm});
            skCircle(sketch, "E45.108.46.0", {"center": v(-4, -114) * mm, "radius": 1.5 * mm});
            skCircle(sketch, "E45.110.46.0", {"center": v(41, -114) * mm, "radius": 1.5 * mm});
            skCircle(sketch, "E45.112.46.0", {"center": v(-34, -114) * mm, "radius": 1.5 * mm});
            skCircle(sketch, "E45.114.46.0", {"center": v(-114, -114) * mm, "radius": 1.5 * mm});
            skCircle(sketch, "E45.116.46.0", {"center": v(121, -114) * mm, "radius": 1.5 * mm});
            skCircle(sketch, "E45.118.46.0", {"center": v(-74, -114) * mm, "radius": 1.5 * mm});
            skCircle(sketch, "E45.122.46.0", {"center": v(161, -114) * mm, "radius": 1.5 * mm});
            skCircle(sketch, "E45.124.46.0", {"center": v(81, -114) * mm, "radius": 1.5 * mm});
            skCircle(sketch, "E45.126.46.0", {"center": v(1, -114) * mm, "radius": 1.5 * mm});
            skCircle(sketch, "E45.128.46.0", {"center": v(46, -114) * mm, "radius": 1.5 * mm});
            skCircle(sketch, "E45.130.46.0", {"center": v(-29, -114) * mm, "radius": 1.5 * mm});
            skCircle(sketch, "E45.132.46.0", {"center": v(-109, -114) * mm, "radius": 1.5 * mm});
            skCircle(sketch, "E45.134.46.0", {"center": v(126, -114) * mm, "radius": 1.5 * mm});
            skSolve(sketch);
        }
        {
            var Q0;
            Q0=makeQuery(id+"F0.imprint","IMPRINT",FACE,{"disambiguationData":[TD([[makeQuery(id+"F0.imprint","IMPRINT",EDGE,{"derivedFrom":sQuery(id+"F0.wireOp",EDGE,"E0")}),-1.0]])]});
            extrude(context, id + "F1", {"entities" : qUnion([Q0]), "depth" : 2 * mm});
        }
    });
